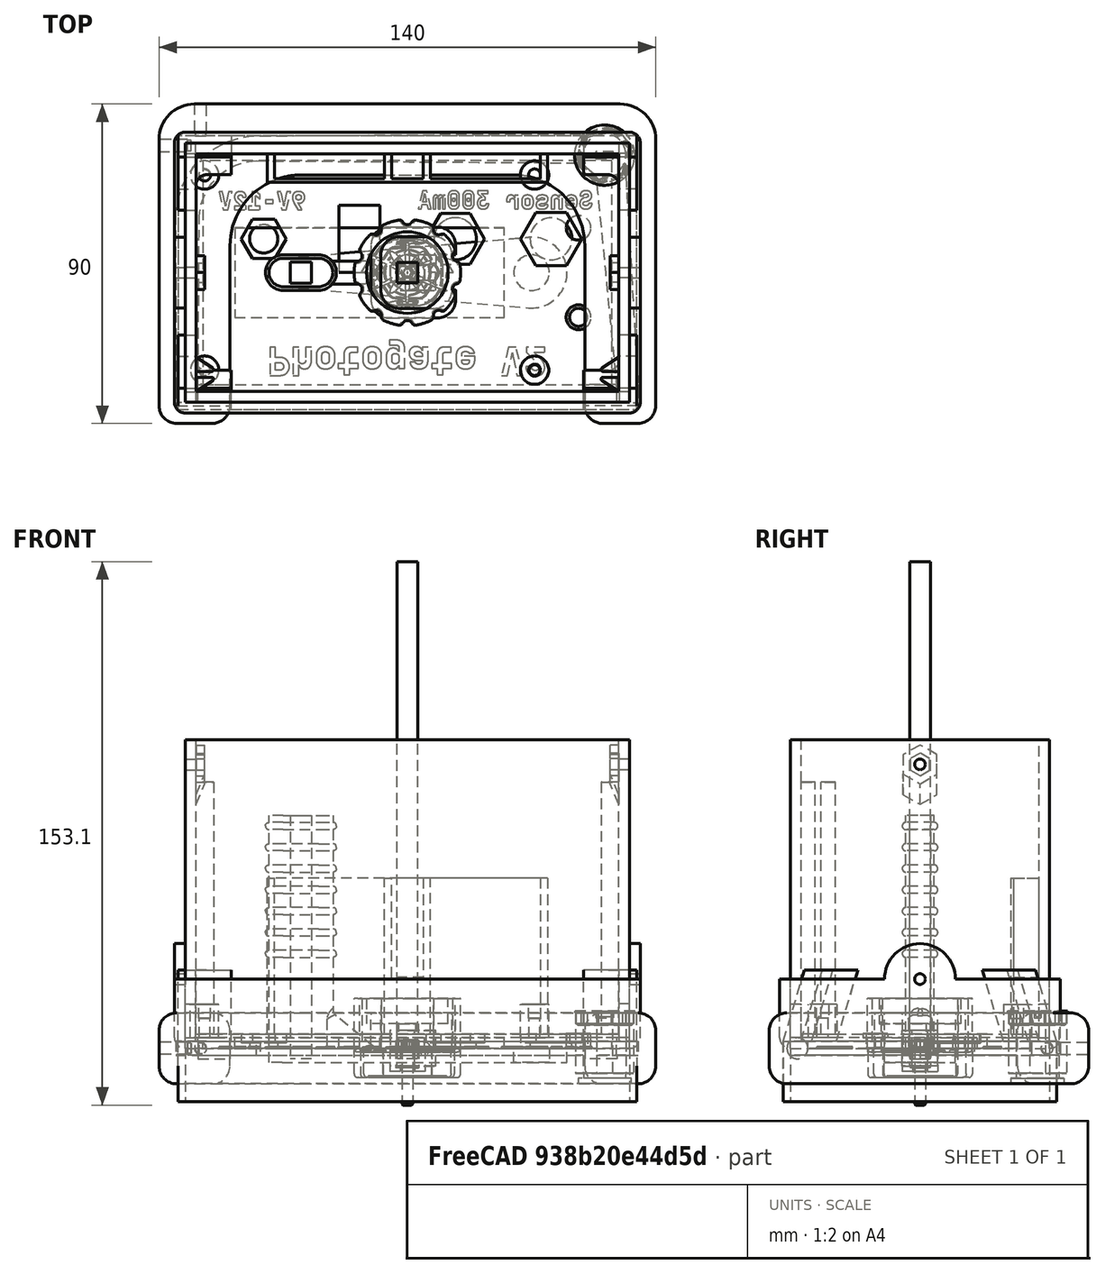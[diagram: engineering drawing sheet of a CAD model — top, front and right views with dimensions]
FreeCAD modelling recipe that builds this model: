
FCSTD DOCUMENT  (FreeCAD 1.1R44795 (Git))
Label: All_Models
License: All rights reserved
LicenseURL: https://en.wikipedia.org/wiki/All_rights_reserved
objects: Sketcher::SketchObject×46, PartDesign::Pad×32, PartDesign::Pocket×28, App::Link×21, App::FeaturePython×21, App::Point×14, PartDesign::Body×12, PartDesign::Mirrored×8, PartDesign::Fillet×7, Part::Part2DObjectPython×4, PartDesign::MultiTransform×3, PartDesign::Chamfer×2, PartDesign::PolarPattern×2, PartDesign::SubtractivePipe×2, PartDesign::SubShapeBinder×2, Assembly::JointGroup×2, Assembly::AssemblyObject×2, Part::FeaturePython×2, App::DocumentObjectGroup×2, PartDesign::LinearPattern×1, +1 more types
note: 354 computed .brp shape members not serialized (recipe doc carries the construction recipe); baked Part::Feature solids carry a one-line shape summary decoded from their .brp

FEATURE [Sketcher::SketchObject] Sketch
  ArcFitTolerance = 1e-06
  AttachmentSupport = -> [XY_Plane]
  ExternalTypes = [0]
  FullyConstrained = true
  MakeInternals = false
  MapMode = 5
  _ExternalGeoVersion = 0
  expr: Constraints[22] = Sketch001.Constraints.display_inner_width - 0.1 mm
  expr: Constraints[23] = Sketch001.Constraints.display_inner_length - 0.1 mm
  sketch-geometry (10):
    g0: LineSegment StartX=-59.6 StartY=-33.5 StartZ=0 EndX=59.6 EndY=-33.5 EndZ=0
    g1: LineSegment StartX=59.6 StartY=-33.5 StartZ=0 EndX=59.6 EndY=33.5 EndZ=0
    g2: LineSegment StartX=59.6 StartY=33.5 StartZ=0 EndX=-59.6 EndY=33.5 EndZ=0
    g3: LineSegment StartX=-59.6 StartY=33.5 StartZ=0 EndX=-59.6 EndY=-33.5 EndZ=0
    g4: GeomPoint [constr] X=0 Y=0 Z=0
    g5: LineSegment StartX=-62.6 StartY=-36.5 StartZ=0 EndX=62.6 EndY=-36.5 EndZ=0
    g6: LineSegment StartX=62.6 StartY=-36.5 StartZ=0 EndX=62.6 EndY=36.5 EndZ=0
    g7: LineSegment StartX=62.6 StartY=36.5 StartZ=0 EndX=-62.6 EndY=36.5 EndZ=0
    g8: LineSegment StartX=-62.6 StartY=36.5 StartZ=0 EndX=-62.6 EndY=-36.5 EndZ=0
    g9: GeomPoint [constr] X=0 Y=0 Z=0
  constraints (24):
    c: Coincident(g0,g1)
    c: Coincident(g1,g2)
    c: Coincident(g2,g3)
    c: Coincident(g3,g0)
    c: Horizontal(g0)
    c: Horizontal(g2)
    c: Vertical(g1)
    c: Vertical(g3)
    c: Symmetric(g2,g0,g4)
    c: Coincident(g4,g-1)
    c: Coincident(g5,g6)
    c: Coincident(g6,g7)
    c: Coincident(g7,g8)
    c: Coincident(g8,g5)
    c: Horizontal(g5)
    c: Horizontal(g7)
    c: Vertical(g6)
    c: Vertical(g8)
    c: Symmetric(g7,g5,g9)
    c: Coincident(g9,g4)
    c: DistanceY(g1,g6) = 3
    c: DistanceX(g1,g6) = 3
    c: DistanceY(g8,g8) = 73
    c: DistanceX(g5,g5) = 125.2
FEATURE [PartDesign::Pad] Pad005
  Direction = (0,0,1)
  Length = 4
  Length2 = 10
  Profile = -> Sketch [Edge6,Edge5,Edge7,Edge8]
  ReferenceAxis = -> Sketch [N_Axis]
  Refine = true
  SideType = 0
  Suppressed = false
  Type = 0
  Type2 = 0
FEATURE [PartDesign::Pad] Pad006
  BaseFeature = -> Pad005
  Direction = (0,0,1)
  Length = 87
  Length2 = 10
  Profile = -> Sketch
  ReferenceAxis = -> Sketch [N_Axis]
  Refine = true
  SideType = 0
  Suppressed = false
  Type = 0
  Type2 = 0
FEATURE [Sketcher::SketchObject] Sketch007
  ArcFitTolerance = 1e-06
  AttachmentSupport = -> [Pad006]
  ExternalGeometry = -> [Pad006]
  ExternalTypes = [0]
  FullyConstrained = true
  MakeInternals = false
  MapMode = 5
  Placement = pos=(-59.6,0,0) rot=(0.57735,0.57735,0.57735;2.0944rad)
  _ExternalGeoVersion = 0
  sketch-geometry (15):
    g0: LineSegment StartX=2.75 StartY=81.5877 StartZ=0 EndX=1.24e-14 EndY=83.1754 EndZ=0
    g1: LineSegment StartX=1.24e-14 StartY=83.1754 StartZ=0 EndX=-2.75 EndY=81.5877 EndZ=0
    g2: LineSegment StartX=-2.75 StartY=81.5877 StartZ=0 EndX=-2.75 EndY=78.4123 EndZ=0
    g3: LineSegment StartX=-2.75 StartY=78.4123 StartZ=0 EndX=-2.895e-13 EndY=76.8246 EndZ=0
    g4: LineSegment StartX=-2.895e-13 StartY=76.8246 StartZ=0 EndX=2.75 EndY=78.4123 EndZ=0
    g5: LineSegment StartX=2.75 StartY=78.4123 StartZ=0 EndX=2.75 EndY=81.5877 EndZ=0
    g6: Circle [constr] CenterX=0 CenterY=80 CenterZ=0 NormalX=0 NormalY=0 NormalZ=1 AngleXU=0 Radius=3.17543
    g7: Circle CenterX=0 CenterY=80 CenterZ=0 NormalX=0 NormalY=0 NormalZ=1 AngleXU=0 Radius=1.5
    g8: LineSegment StartX=4.75 StartY=82.7424 StartZ=0 EndX=-3.91e-14 EndY=85.4848 EndZ=0
    g9: LineSegment StartX=-3.91e-14 StartY=85.4848 StartZ=0 EndX=-4.75 EndY=82.7424 EndZ=0
    g10: LineSegment StartX=-4.75 StartY=82.7424 StartZ=0 EndX=-4.75 EndY=77.2576 EndZ=0
    g11: LineSegment StartX=-4.75 StartY=77.2576 StartZ=0 EndX=3.73e-14 EndY=74.5152 EndZ=0
    g12: LineSegment StartX=3.73e-14 StartY=74.5152 StartZ=0 EndX=4.75 EndY=77.2576 EndZ=0
    g13: LineSegment StartX=4.75 StartY=77.2576 StartZ=0 EndX=4.75 EndY=82.7424 EndZ=0
    g14: Circle [constr] CenterX=0 CenterY=80 CenterZ=0 NormalX=0 NormalY=0 NormalZ=1 AngleXU=0 Radius=5.48483
  constraints (35):
    c: Coincident(g0,g1)
    c: Coincident(g1,g2)
    c: Coincident(g2,g3)
    c: Coincident(g3,g4)
    c: Coincident(g4,g5)
    c: Coincident(g5,g0)
    c: Equal(g0, g1-g5) x5
    c: PointOnObject(g0,g6)
    c: PointOnObject(g1,g6)
    c: PointOnObject(g2,g6)
    c: PointOnObject(g3,g6)
    c: PointOnObject(g4,g6)
    c: PointOnObject(g5,g6)
    c: PointOnObject(g6,g-2)
    c: Coincident(g7,g6)
    c: Diameter(g7) = 3
    c: DistanceX(g1,g0) = 5.5
    c: Horizontal(g0,g1)
    c: DistanceY(g6,g-3) = 7  'gap_box_painel'
    c: Coincident(g8,g9)
    c: Coincident(g9,g10)
    c: Coincident(g10,g11)
    c: Coincident(g11,g12)
    c: Coincident(g12,g13)
    c: Coincident(g13,g8)
    c: Equal(g8, g9-g13) x5
    c: PointOnObject(g8,g14)
    c: PointOnObject(g9,g14)
    c: PointOnObject(g10,g14)
    c: PointOnObject(g11,g14)
    c: PointOnObject(g12,g14)
    c: PointOnObject(g13,g14)
    c: Coincident(g14,g6)
    c: Vertical(g13)
    c: DistanceX(g0,g8) = 2
FEATURE [PartDesign::Pocket] Pocket005
  BaseFeature = -> Pad006
  Direction = (-1,0,0)
  Length = 5
  Length2 = 5
  Profile = -> Sketch007 [Edge7]
  ReferenceAxis = -> Sketch007 [N_Axis]
  Refine = true
  SideType = 0
  Suppressed = false
  Type = 1
  Type2 = 0
FEATURE [PartDesign::Pad] Pad007
  BaseFeature = -> Pocket005
  Direction = (1,0,0)
  Length = 2.5
  Length2 = 10
  Profile = -> Sketch007 [Edge12,Edge5,Edge4,Edge11,Edge10,Edge3,Edge2,Edge1,Edge6,Edge13,Edge8,Edge9]
  ReferenceAxis = -> Sketch007 [N_Axis]
  Refine = true
  SideType = 0
  Suppressed = false
  Type = 0
  Type2 = 0
FEATURE [PartDesign::Chamfer] Chamfer
  Angle = 45
  Base = -> Pad007 [Edge26,Edge31]
  BaseFeature = -> Pad007
  ChamferType = 1
  FlipDirection = false
  Refine = true
  Size = 5
  Size2 = 2.4999
  SupportTransform = false
  Suppressed = false
  UseAllEdges = false
FEATURE [Sketcher::SketchObject] Sketch008
  ArcFitTolerance = 1e-06
  AttachmentSupport = -> [Chamfer]
  ExternalGeometry = -> [Chamfer]
  ExternalTypes = [0]
  FullyConstrained = true
  MakeInternals = false
  MapMode = 5
  Placement = pos=(0,0,4) rot=(0,0,1;0rad)
  _ExternalGeoVersion = 0
  sketch-geometry (10):
    g0: LineSegment StartX=-59.6 StartY=-33.5 StartZ=0 EndX=-59.6 EndY=-29.5 EndZ=0
    g1: LineSegment StartX=-59.6 StartY=-29.5 StartZ=0 EndX=-55.1 EndY=-29.5 EndZ=0
    g2: LineSegment StartX=-54.8288 StartY=-30.4201 StartZ=0 EndX=-59.6 EndY=-33.5 EndZ=0
    g3: ArcOfCircle CenterX=-55.1 CenterY=-30 CenterZ=0 NormalX=0 NormalY=0 NormalZ=1 AngleXU=0 Radius=0.5 StartAngle=5.28561 EndAngle=7.85398
    g4: GeomPoint [constr] X=-53.4035 Y=-29.5 Z=0
    g5: GeomPoint X=-54.6 Y=-30 Z=0
    g6: LineSegment StartX=-59.6 StartY=-23.85 StartZ=0 EndX=-59.6 EndY=-27.85 EndZ=0
    g7: LineSegment StartX=-59.6 StartY=-27.85 StartZ=0 EndX=-55.1 EndY=-27.85 EndZ=0
    g8: LineSegment StartX=-54.8288 StartY=-26.9299 StartZ=0 EndX=-59.6 EndY=-23.85 EndZ=0
    g9: ArcOfCircle CenterX=-55.1 CenterY=-27.35 CenterZ=0 NormalX=0 NormalY=0 NormalZ=1 AngleXU=0 Radius=0.5 StartAngle=4.71239 EndAngle=7.28076
  constraints (25):
    c: Vertical(g0)
    c: Coincident(g0,g1)
    c: Horizontal(g1)
    c: DistanceY(g0,g0) = 4
    c: PointOnObject(g4,g1)
    c: PointOnObject(g4,g2)
    c: Tangent(g1,g3) = 1.5708
    c: Tangent(g2,g3) = 1.5708
    c: Radius(g3) = 0.5
    c: PointOnObject(g5,g3)
    c: DistanceX(g0,g5) = 5
    c: Horizontal(g3,g5)
    c: Vertical(g6)
    c: Coincident(g6,g7)
    c: Coincident(g8,g6)
    c: Horizontal(g7)
    c: Tangent(g7,g9) = -1.5708
    c: Tangent(g8,g9) = -1.5708
    c: Radius(g9) = 0.5
    c: Vertical(g6,g0)
    c: Vertical(g7,g1)
    c: Equal(g0,g6)
    c: DistanceY(g1,g7) = 1.65
    c: Coincident(g2,g0)
    c: Coincident(g0,g-4)
FEATURE [PartDesign::Pad] Pad008
  BaseFeature = -> Chamfer
  Direction = (0,0,1)
  Length = 10
  Length2 = 10
  Offset = 12
  Profile = -> Sketch008
  ReferenceAxis = -> Sketch008 [N_Axis]
  Refine = true
  SideType = 0
  Suppressed = false
  Type = 3
  Type2 = 0
  UpToFace = -> Chamfer [Face11]
  expr: Offset = Sketch007.Constraints.gap_box_painel + 5 mm
FEATURE [PartDesign::Mirrored] Mirrored004
  BaseFeature = -> Pad008
  MirrorPlane = -> YZ_Plane
  Originals = -> [Chamfer,Pad007,Pad008,Pocket005]
  Refine = true
  Suppressed = false
  TransformMode = 0
FEATURE [Sketcher::SketchObject] Sketch009
  ArcFitTolerance = 1e-06
  AttachmentSupport = -> [XY_Plane]
  ExternalTypes = [0]
  FullyConstrained = true
  MakeInternals = false
  MapMode = 5
  _ExternalGeoVersion = 0
  sketch-geometry (11):
    g0: Circle CenterX=40.5 CenterY=9.5 CenterZ=0 NormalX=0 NormalY=0 NormalZ=1 AngleXU=0 Radius=5.9
    g1: Circle CenterX=-40.5 CenterY=9.5 CenterZ=0 NormalX=0 NormalY=0 NormalZ=1 AngleXU=0 Radius=4
    g2: LineSegment StartX=-19.25 StartY=19 StartZ=0 EndX=-19.25 EndY=0 EndZ=0
    g3: LineSegment StartX=-19.25 StartY=0 StartZ=0 EndX=-7.75 EndY=0 EndZ=0
    g4: LineSegment StartX=-7.75 StartY=0 StartZ=0 EndX=-7.75 EndY=19 EndZ=0
    g5: LineSegment StartX=-7.75 StartY=19 StartZ=0 EndX=-19.25 EndY=19 EndZ=0
    g6: GeomPoint [constr] X=-13.5 Y=9.5 Z=0
    g7: Circle CenterX=13.5 CenterY=9.5 CenterZ=0 NormalX=0 NormalY=0 NormalZ=1 AngleXU=0 Radius=5.95
    g8: LineSegment [constr] StartX=-40.5 StartY=9.5 StartZ=0 EndX=-13.5 EndY=9.5 EndZ=0
    g9: LineSegment [constr] StartX=-13.5 StartY=9.5 StartZ=0 EndX=13.5 EndY=9.5 EndZ=0
    g10: LineSegment [constr] StartX=13.5 StartY=9.5 StartZ=0 EndX=40.5 EndY=9.5 EndZ=0
  constraints (27):
    c: Diameter(g0) = 11.8
    c: Diameter(g1) = 8
    c: Coincident(g2,g3)
    c: Coincident(g3,g4)
    c: Coincident(g4,g5)
    c: Coincident(g5,g2)
    c: Vertical(g2)
    c: Vertical(g4)
    c: Horizontal(g3)
    c: Horizontal(g5)
    c: Symmetric(g4,g2,g6)
    c: Diameter(g7) = 11.9
    c: DistanceY(g4,g4) = 19
    c: Distance(g5,g5) = 11.5
    c: Coincident(g8,g1)
    c: Horizontal(g8)
    c: Coincident(g9,g8)
    c: Coincident(g9,g7)
    c: Coincident(g10,g7)
    c: Horizontal(g10)
    c: Coincident(g10,g0)
    c: Coincident(g8,g6)
    c: Equal(g8,g9)
    c: Equal(g9,g10)
    c: Horizontal(g-1,g3)
    c: DistanceX(g8,g8) = 27
    c: Symmetric(g6,g7,g-2)
FEATURE [PartDesign::Pocket] Pocket006
  BaseFeature = -> Mirrored004
  Direction = (0,0,-1)
  Length = 5
  Length2 = 5
  Profile = -> Sketch009
  ReferenceAxis = -> Sketch009 [N_Axis]
  Refine = true
  Reversed = true
  SideType = 0
  Suppressed = false
  Type = 2
  Type2 = 0
FEATURE [Part::Part2DObjectPython] ShapeString  # Draft 2D object (typed FeaturePython)
  FontFile = <userpath>/Documents/FreeCAD/Fonts/JetBrainsMonoNerdFont-ExtraBold.ttf
  Fuse = false
  Justification = 7
  JustificationReference = 0
  KeepLeftMargin = false
  MakeFace = true
  ObliqueAngle = 0
  Placement = pos=(-41.02,17.76,1e-15) rot=(0,-1,0;3.14159rad)
  ScaleToSize = true
  Size = 5
  String = 9V-12V
  Tracking = 0
FEATURE [Part::Part2DObjectPython] ShapeString001  # Draft 2D object (typed FeaturePython)
  FontFile = <userpath>/Documents/FreeCAD/Fonts/JetBrainsMonoNerdFont-Bold.ttf
  Fuse = false
  Justification = 7
  JustificationReference = 0
  KeepLeftMargin = false
  MakeFace = true
  ObliqueAngle = 0
  Placement = pos=(13,18,1.3e-15) rot=(0,-1,0;3.14159rad)
  ScaleToSize = true
  Size = 5
  String = 300mA
  Tracking = 0
FEATURE [Part::Part2DObjectPython] ShapeString002  # Draft 2D object (typed FeaturePython)
  FontFile = <userpath>/Documents/FreeCAD/Fonts/JetBrainsMonoNerdFont-ExtraBold.ttf
  Fuse = false
  Justification = 7
  JustificationReference = 0
  KeepLeftMargin = false
  MakeFace = true
  ObliqueAngle = 0
  Placement = pos=(40,18,-4.9e-15) rot=(0,-1,0;3.14159rad)
  ScaleToSize = true
  Size = 5
  String = Sensor
  Tracking = 0
FEATURE [PartDesign::Pocket] Pocket007
  BaseFeature = -> Pocket006
  Direction = (1e-16,0,1)
  Length = 0.4
  Length2 = 5
  Profile = -> ShapeString002
  ReferenceAxis = -> ShapeString002 [N_Axis]
  Refine = true
  SideType = 0
  Suppressed = false
  Type = 0
  Type2 = 0
FEATURE [PartDesign::Pocket] Pocket008
  BaseFeature = -> Pocket007
  Direction = (1e-16,0,1)
  Length = 0.4
  Length2 = 5
  Profile = -> ShapeString001
  ReferenceAxis = -> ShapeString001 [N_Axis]
  Refine = true
  SideType = 0
  Suppressed = false
  Type = 0
  Type2 = 0
FEATURE [PartDesign::Pocket] Pocket009
  BaseFeature = -> Pocket008
  Direction = (1e-16,0,1)
  Length = 0.4
  Length2 = 5
  Profile = -> ShapeString
  ReferenceAxis = -> ShapeString [N_Axis]
  Refine = true
  SideType = 0
  Suppressed = false
  Type = 0
  Type2 = 0
FEATURE [Sketcher::SketchObject] Sketch010
  ArcFitTolerance = 1e-06
  AttachmentSupport = -> [XY_Plane002]
  ExternalTypes = [0]
  FullyConstrained = true
  MakeInternals = false
  MapMode = 5
  _ExternalGeoVersion = 0
  sketch-geometry (9):
    g0: ArcOfCircle CenterX=-35 CenterY=0 CenterZ=0 NormalX=0 NormalY=0 NormalZ=1 AngleXU=0 Radius=4 StartAngle=1.65662 EndAngle=4.62657
    g1: ArcOfCircle CenterX=35 CenterY=0 CenterZ=0 NormalX=0 NormalY=0 NormalZ=1 AngleXU=0 Radius=10 StartAngle=4.62657 EndAngle=7.9398
    g2: LineSegment StartX=-35.3429 StartY=3.98528 StartZ=0 EndX=34.1429 EndY=9.9632 EndZ=0
    g3: LineSegment StartX=-35.3429 StartY=-3.98528 StartZ=0 EndX=34.1429 EndY=-9.9632 EndZ=0
    g4: ArcOfCircle CenterX=-35 CenterY=0 CenterZ=0 NormalX=0 NormalY=0 NormalZ=1 AngleXU=0 Radius=4 StartAngle=1.5708 EndAngle=4.71239
    g5: ArcOfCircle CenterX=-25 CenterY=-1e-16 CenterZ=0 NormalX=0 NormalY=0 NormalZ=1 AngleXU=0 Radius=4 StartAngle=4.71239 EndAngle=7.85398
    g6: LineSegment StartX=-35 StartY=4 StartZ=0 EndX=-25 EndY=4 EndZ=0
    g7: LineSegment StartX=-35 StartY=-4 StartZ=0 EndX=-25 EndY=-4 EndZ=0
    g8: Circle CenterX=35 CenterY=0 CenterZ=0 NormalX=0 NormalY=0 NormalZ=1 AngleXU=0 Radius=5
  constraints (20):
    c: Tangent(g0,g2) = 1.5708
    c: Tangent(g0,g3) = -1.5708
    c: Tangent(g1,g2) = 1.5708
    c: Tangent(g1,g3) = -1.5708
    c: Symmetric(g0,g1,g-1)
    c: DistanceX(g0,g1) = 70
    c: PointOnObject(g0,g-1)
    c: Radius(g0) = 4
    c: Radius(g1) = 10
    c: Tangent(g4,g6) = 1.5708
    c: Tangent(g4,g7) = -1.5708
    c: Tangent(g5,g6) = 1.5708
    c: Tangent(g5,g7) = -1.5708
    c: Equal(g4,g5)
    c: Horizontal(g7)
    c: Coincident(g4,g0)
    c: Tangent(g4,g0)
    c: DistanceX(g0,g5) = 10
    c: Diameter(g8) = 10
    c: Coincident(g8,g1)
FEATURE [PartDesign::Pad] Pad009
  Direction = (0,0,1)
  Length = 4
  Length2 = 10
  Profile = -> Sketch010 [Edge1,Edge2,Edge4,Edge9,Edge3]
  ReferenceAxis = -> Sketch010 [N_Axis]
  Refine = true
  Reversed = true
  SideType = 0
  Suppressed = false
  Type = 0
  Type2 = 0
FEATURE [PartDesign::Pad] Pad010
  BaseFeature = -> Pad009
  Direction = (0,0,1)
  Length = 65.65
  Length2 = 10
  Profile = -> Sketch010 [Edge7,Edge6,Vertex6,Edge5,Edge8]
  ReferenceAxis = -> Sketch010 [N_Axis]
  Refine = true
  SideType = 0
  Suppressed = false
  Type = 0
  Type2 = 0
  expr: Length = Sketch001.Constraints.display_inner_length / 2 + 3 mm
FEATURE [Sketcher::SketchObject] Sketch011
  ArcFitTolerance = 1e-06
  AttachmentOffset = pos=(0,0,-2) rot=(0,0,1;0rad)
  AttachmentSupport = -> [Pad010]
  ExternalTypes = [0]
  FullyConstrained = true
  MakeInternals = false
  MapMode = 5
  Placement = pos=(0,0,63.65) rot=(0,0,1;0rad)
  _ExternalGeoVersion = 0
  sketch-geometry (4):
    g0: ArcOfCircle CenterX=-35 CenterY=0 CenterZ=0 NormalX=0 NormalY=0 NormalZ=1 AngleXU=0 Radius=5 StartAngle=1.5708 EndAngle=4.71239
    g1: ArcOfCircle CenterX=-25 CenterY=-1e-16 CenterZ=0 NormalX=0 NormalY=0 NormalZ=1 AngleXU=0 Radius=5 StartAngle=4.71239 EndAngle=7.85398
    g2: LineSegment StartX=-35 StartY=5 StartZ=0 EndX=-25 EndY=5 EndZ=0
    g3: LineSegment StartX=-35 StartY=-5 StartZ=0 EndX=-25 EndY=-5 EndZ=0
  constraints (8):
    c: Tangent(g0,g2) = 1.5708
    c: Tangent(g0,g3) = -1.5708
    c: Tangent(g1,g2) = 1.5708
    c: Tangent(g1,g3) = -1.5708
    c: Equal(g0,g1)
    c: Radius(g1) = 5
    c: Coincident(g1,g-3)
    c: Coincident(g0,g-4)
FEATURE [PartDesign::Pad] Pad011
  BaseFeature = -> Pad010
  Direction = (0,0,1)
  Length = 2
  Length2 = 10
  Profile = -> Sketch011
  ReferenceAxis = -> Sketch011 [N_Axis]
  Refine = true
  Reversed = true
  SideType = 0
  Suppressed = false
  Type = 0
  Type2 = 0
FEATURE [PartDesign::Fillet] Fillet001
  Base = -> Pad011 [Face14]
  BaseFeature = -> Pad011
  Radius = 0.99
  Refine = true
  SupportTransform = false
  Suppressed = false
  UseAllEdges = false
FEATURE [PartDesign::LinearPattern] LinearPattern
  BaseFeature = -> Fillet001
  Direction = -> Z_Axis002
  Length = 36
  Length2 = 100
  Mode = 1
  Mode2 = 0
  Occurrences = 7
  Occurrences2 = 1
  Offset = 6
  Offset2 = 10
  Originals = -> [Pad011,Fillet001]
  Refine = true
  Reversed = true
  Reversed2 = false
  SpacingPattern = [0]
  SpacingPattern2 = [0]
  Spacings = [-1,-1,-1,-1,-1,-1]
  Suppressed = false
  TransformMode = 0
FEATURE [Sketcher::SketchObject] Sketch012
  ArcFitTolerance = 1e-06
  AttachmentSupport = -> [XY_Plane003]
  ExternalTypes = [0]
  FullyConstrained = true
  MakeInternals = false
  MapMode = 5
  _ExternalGeoVersion = 0
  sketch-geometry (1):
    g0: Circle CenterX=0 CenterY=0 CenterZ=0 NormalX=0 NormalY=0 NormalZ=1 AngleXU=0 Radius=15
  constraints (2):
    c: Diameter(g0) = 30
    c: Coincident(g0,g-1)
FEATURE [PartDesign::Pad] Pad012
  Direction = (0,0,1)
  Length = 8.2
  Length2 = 10
  Profile = -> Sketch012
  ReferenceAxis = -> Sketch012 [N_Axis]
  Refine = true
  Reversed = true
  SideType = 0
  Suppressed = false
  Type = 0
  Type2 = 0
FEATURE [Sketcher::SketchObject] Sketch013
  ArcFitTolerance = 1e-06
  AttachmentSupport = -> [XY_Plane003]
  ExternalGeometry = -> [Pad012]
  ExternalTypes = [0]
  FullyConstrained = true
  MakeInternals = false
  MapMode = 5
  _ExternalGeoVersion = 0
  sketch-geometry (4):
    g0: LineSegment [constr] StartX=0 StartY=0 StartZ=0 EndX=-1.95789 EndY=14.8717 EndZ=0
    g1: LineSegment [constr] StartX=0 StartY=0 StartZ=0 EndX=1.95789 EndY=14.8717 EndZ=0
    g2: ArcOfCircle CenterX=0 CenterY=0 CenterZ=0 NormalX=0 NormalY=0 NormalZ=1 AngleXU=0 Radius=15 StartAngle=1.4399 EndAngle=1.7017
    g3: ArcOfCircle CenterX=-4.3e-15 CenterY=15 CenterZ=0 NormalX=0 NormalY=0 NormalZ=1 AngleXU=0 Radius=1.96209 StartAngle=3.20704 EndAngle=6.21774
  constraints (12):
    c: PointOnObject(g0,g-3)
    c: PointOnObject(g1,g-3)
    c: Horizontal(g1,g0)
    c: Coincident(g1,g-1)
    c: Coincident(g0,g1)
    c: PointOnObject(g3,g2)
    c: Coincident(g3,g2)
    c: Coincident(g3,g2)
    c: Coincident(g2,g0)
    c: Horizontal(g0,g2)
    c: Coincident(g2,g0)
    c: Angle(g1,g0) = 0.261799
FEATURE [PartDesign::Pocket] Pocket011
  BaseFeature = -> Pad012
  Direction = (0,0,-1)
  Length = 5
  Length2 = 5
  Profile = -> Sketch013
  ReferenceAxis = -> Sketch013 [N_Axis]
  Refine = true
  SideType = 0
  Suppressed = false
  Type = 1
  Type2 = 0
FEATURE [PartDesign::PolarPattern] PolarPattern
  Angle = 360
  Axis = -> Sketch013 [N_Axis]
  BaseFeature = -> Pocket011
  Mode = 0
  Occurrences = 10
  Offset = 120
  Originals = -> [Pocket011]
  Refine = true
  SpacingPattern = [0]
  Spacings = [-1,-1,-1,-1,-1,-1,-1,-1,-1]
  Suppressed = false
  TransformMode = 0
FEATURE [Sketcher::SketchObject] Sketch016
  ArcFitTolerance = 1e-06
  AttachmentSupport = -> [XY_Plane005]
  ExternalTypes = [0]
  FullyConstrained = true
  MakeInternals = false
  MapMode = 5
  _ExternalGeoVersion = 0
  sketch-geometry (22):
    g0: LineSegment StartX=-70 StartY=-37.5 StartZ=0 EndX=-70 EndY=37.5 EndZ=0
    g1: LineSegment StartX=-60 StartY=47.5 StartZ=0 EndX=60 EndY=47.5 EndZ=0
    g2: LineSegment StartX=70 StartY=37.5 StartZ=0 EndX=70 EndY=-37.5 EndZ=0
    g3: LineSegment StartX=65 StartY=-42.5 StartZ=0 EndX=55 EndY=-42.5 EndZ=0
    g4: LineSegment StartX=50 StartY=-37.5 StartZ=0 EndX=50 EndY=7.5 EndZ=0
    g5: LineSegment StartX=30 StartY=27.5 StartZ=0 EndX=-30 EndY=27.5 EndZ=0
    g6: LineSegment StartX=-50 StartY=7.5 StartZ=0 EndX=-50 EndY=-37.5 EndZ=0
    g7: LineSegment StartX=-55 StartY=-42.5 StartZ=0 EndX=-65 EndY=-42.5 EndZ=0
    g8: ArcOfCircle CenterX=-65 CenterY=-37.5 CenterZ=0 NormalX=0 NormalY=0 NormalZ=1 AngleXU=0 Radius=5 StartAngle=3.14159 EndAngle=4.71239
    g9: ArcOfCircle CenterX=-55 CenterY=-37.5 CenterZ=0 NormalX=0 NormalY=0 NormalZ=1 AngleXU=0 Radius=5 StartAngle=4.71239 EndAngle=6.28319
    g10: ArcOfCircle CenterX=-30 CenterY=7.5 CenterZ=0 NormalX=0 NormalY=0 NormalZ=1 AngleXU=0 Radius=20 StartAngle=1.5708 EndAngle=3.14159
    g11: ArcOfCircle CenterX=30 CenterY=7.5 CenterZ=0 NormalX=0 NormalY=0 NormalZ=1 AngleXU=0 Radius=20 StartAngle=0 EndAngle=1.5708
    g12: ArcOfCircle CenterX=60 CenterY=37.5 CenterZ=0 NormalX=0 NormalY=0 NormalZ=1 AngleXU=0 Radius=10 StartAngle=0 EndAngle=1.5708
    g13: ArcOfCircle CenterX=65 CenterY=-37.5 CenterZ=0 NormalX=0 NormalY=0 NormalZ=1 AngleXU=0 Radius=5 StartAngle=4.71239 EndAngle=6.28319
    g14: ArcOfCircle CenterX=55 CenterY=-37.5 CenterZ=0 NormalX=0 NormalY=0 NormalZ=1 AngleXU=0 Radius=5 StartAngle=3.14159 EndAngle=4.71239
    g15: ArcOfCircle CenterX=-60 CenterY=37.5 CenterZ=0 NormalX=0 NormalY=0 NormalZ=1 AngleXU=0 Radius=10 StartAngle=1.5708 EndAngle=3.14159
    g16: LineSegment [constr] StartX=-30 StartY=27.5 StartZ=0 EndX=-30 EndY=47.5 EndZ=0
    g17: LineSegment [constr] StartX=-50 StartY=7.5 StartZ=0 EndX=-70 EndY=7.5 EndZ=0
    g18: Circle CenterX=55.6066 CenterY=33.1066 CenterZ=0 NormalX=0 NormalY=0 NormalZ=1 AngleXU=0 Radius=6
    g19: GeomPoint X=44.1421 Y=21.6421 Z=0
    g20: GeomPoint X=67.0711 Y=44.5711 Z=0
    g21: LineSegment [constr] StartX=44.1421 StartY=21.6421 StartZ=0 EndX=67.0711 EndY=44.5711 EndZ=0
  constraints (51):
    c: Vertical(g0)
    c: Horizontal(g1)
    c: Horizontal(g3)
    c: Vertical(g4)
    c: Horizontal(g5)
    c: Vertical(g6)
    c: Horizontal(g7)
    c: Tangent(g7,g8) = 1.5708
    c: Tangent(g0,g8) = 1.5708
    c: Tangent(g6,g9) = 1.5708
    c: Tangent(g7,g9) = 1.5708
    c: Tangent(g5,g10) = -1.5708
    c: Tangent(g6,g10) = -1.5708
    c: Tangent(g4,g11) = -1.5708
    c: Tangent(g5,g11) = -1.5708
    c: Tangent(g2,g12) = 1.5708
    c: Tangent(g1,g12) = 1.5708
    c: Tangent(g3,g13) = 1.5708
    c: Tangent(g2,g13) = 1.5708
    c: Tangent(g3,g14) = 1.5708
    c: Tangent(g4,g14) = 1.5708
    c: Tangent(g0,g15) = 1.5708
    c: Tangent(g1,g15) = 1.5708
    c: Radius(g15) = 10
    c: Radius(g10) = 20
    c: Radius(g8) = 5
    c: Equal(g15,g12)
    c: Symmetric(g6,g4,g-2)
    c: Coincident(g16,g5)
    c: PointOnObject(g16,g1)
    c: Coincident(g17,g6)
    c: PointOnObject(g17,g0)
    c: Horizontal(g17)
    c: Vertical(g16)
    c: Equal(g17,g16)
    c: DistanceY(g16,g16) = 20
    c: Symmetric(g0,g2,g-2)
    c: Equal(g8,g9)
    c: DistanceX(g6,g4) = 100
    c: DistanceY(g7,g5) = 70
    c: Symmetric(g2,g2,g-1)
    c: Equal(g14,g9)
    c: Equal(g13,g14)
    c: Diameter(g18) = 12
    c: PointOnObject(g19,g11)
    c: PointOnObject(g20,g12)
    c: Symmetric(g19,g20,g18)
    c: Coincident(g21,g19)
    c: Coincident(g21,g20)
    c: Perpendicular(g11,g21)
    c: Perpendicular(g12,g21)
FEATURE [PartDesign::Pad] Pad014
  Direction = (0,0,1)
  Length = 20
  Length2 = 10
  Profile = -> Sketch016
  ReferenceAxis = -> Sketch016 [N_Axis]
  Refine = true
  SideType = 2
  Suppressed = false
  Type = 0
  Type2 = 0
FEATURE [Sketcher::SketchObject] Sketch017
  ArcFitTolerance = 1e-06
  AttachmentSupport = -> [Pad014]
  ExternalGeometry = -> [Pad014]
  ExternalTypes = [0]
  FullyConstrained = true
  MakeInternals = false
  MapMode = 5
  Placement = pos=(-50,0,0) rot=(0.57735,0.57735,0.57735;2.0944rad)
  _ExternalGeoVersion = 0
  sketch-geometry (5):
    g0: Circle CenterX=-34.55 CenterY=0 CenterZ=0 NormalX=0 NormalY=0 NormalZ=1 AngleXU=0 Radius=2.95
    g1: ArcOfCircle CenterX=-34.55 CenterY=0 CenterZ=0 NormalX=0 NormalY=0 NormalZ=1 AngleXU=0 Radius=2.95 StartAngle=5.53819 EndAngle=7.02818
    g2: ArcOfCircle CenterX=-34.55 CenterY=0 CenterZ=0 NormalX=0 NormalY=0 NormalZ=1 AngleXU=0 Radius=2.95 StartAngle=2.3966 EndAngle=3.88658
    g3: LineSegment StartX=-32.3815 StartY=2 StartZ=0 EndX=-36.7185 EndY=2 EndZ=0
    g4: LineSegment StartX=-36.7185 StartY=-2 StartZ=0 EndX=-32.3815 EndY=-2 EndZ=0
  constraints (15):
    c: PointOnObject(g0,g-1)
    c: Tangent(g0,g-3)
    c: Diameter(g0) = 5.9  'led_diammeter'
    c: Coincident(g1,g0)
    c: PointOnObject(g1,g0)
    c: Coincident(g2,g0)
    c: PointOnObject(g2,g0)
    c: Coincident(g3,g2)
    c: Coincident(g4,g2)
    c: Coincident(g4,g1)
    c: Equal(g3,g4)
    c: Distance(g4,g3) = 4
    c: Coincident(g1,g3)
    c: Parallel(g4,g3)
    c: Horizontal(g4)
FEATURE [PartDesign::Pocket] Pocket015
  BaseFeature = -> Pad014
  Direction = (-1,0,0)
  Length = 5
  Length2 = 5
  Offset = -5
  Profile = -> Sketch017 [Edge2,Edge4,Edge3,Edge5]
  ReferenceAxis = -> Sketch017 [N_Axis]
  Refine = true
  SideType = 0
  Suppressed = false
  Type = 2
  Type2 = 0
FEATURE [PartDesign::Pocket] Pocket016
  BaseFeature = -> Pocket015
  Direction = (-1,0,0)
  Length = 9
  Length2 = 5
  Profile = -> Sketch017 [Edge1]
  ReferenceAxis = -> Sketch017 [N_Axis]
  Refine = true
  SideType = 0
  Suppressed = false
  Type = 0
  Type2 = 0
FEATURE [PartDesign::Mirrored] Mirrored006
  BaseFeature = -> Pocket016
  MirrorPlane = -> YZ_Plane005
  Originals = -> [Pocket016,Pocket015]
  Refine = true
  Suppressed = false
  TransformMode = 0
FEATURE [Sketcher::SketchObject] Sketch019
  ArcFitTolerance = 1e-06
  AttachmentSupport = -> [Mirrored006]
  ExternalGeometry = -> [Mirrored006]
  ExternalTypes = [0]
  FullyConstrained = true
  MakeInternals = false
  MapMode = 5
  Placement = pos=(0,0,10) rot=(0,0,1;0rad)
  _ExternalGeoVersion = 0
  sketch-geometry (8):
    g0: LineSegment StartX=63.817 StartY=35.3066 StartZ=0 EndX=57.8066 EndY=41.317 EndZ=0
    g1: LineSegment StartX=57.8066 StartY=41.317 StartZ=0 EndX=49.5962 EndY=39.117 EndZ=0
    g2: LineSegment StartX=49.5962 StartY=39.117 StartZ=0 EndX=47.3962 EndY=30.9066 EndZ=0
    g3: LineSegment StartX=47.3962 StartY=30.9066 StartZ=0 EndX=53.4066 EndY=24.8962 EndZ=0
    g4: LineSegment StartX=53.4066 StartY=24.8962 StartZ=0 EndX=61.617 EndY=27.0962 EndZ=0
    g5: LineSegment StartX=61.617 StartY=27.0962 StartZ=0 EndX=63.817 EndY=35.3066 EndZ=0
    g6: Circle [constr] CenterX=55.6066 CenterY=33.1066 CenterZ=0 NormalX=0 NormalY=0 NormalZ=1 AngleXU=0 Radius=8.5
    g7: LineSegment [constr] StartX=44.1421 StartY=21.6421 StartZ=0 EndX=67.0711 EndY=44.5711 EndZ=0
  constraints (20):
    c: Coincident(g0,g1)
    c: Coincident(g1,g2)
    c: Coincident(g2,g3)
    c: Coincident(g3,g4)
    c: Coincident(g4,g5)
    c: Coincident(g5,g0)
    c: Equal(g0, g1-g5) x5
    c: PointOnObject(g0,g6)
    c: PointOnObject(g1,g6)
    c: PointOnObject(g2,g6)
    c: PointOnObject(g3,g6)
    c: PointOnObject(g4,g6)
    c: PointOnObject(g5,g6)
    c: Coincident(g6,g-3)
    c: PointOnObject(g7,g-4)
    c: PointOnObject(g7,g-5)
    c: PointOnObject(g6,g7)
    c: Perpendicular(g-4,g7)
    c: Perpendicular(g3,g7)
    c: Diameter(g6) = 17
FEATURE [PartDesign::Pocket] Pocket017
  BaseFeature = -> Mirrored006
  Direction = (0,0,-1)
  Length = 17
  Length2 = 5
  Offset = 3
  Profile = -> Sketch019
  ReferenceAxis = -> Sketch019 [N_Axis]
  Refine = true
  SideType = 0
  Suppressed = false
  Type = 0
  Type2 = 0
FEATURE [Sketcher::SketchObject] Sketch020
  ArcFitTolerance = 1e-06
  AttachmentSupport = -> [Pocket017]
  ExternalGeometry = -> [Pocket017]
  ExternalTypes = [0]
  FullyConstrained = true
  MakeInternals = false
  MapMode = 5
  Placement = pos=(0,0,-10) rot=(1,0,0;3.14159rad)
  _ExternalGeoVersion = 0
  sketch-geometry (1):
    g0: Circle CenterX=55.6066 CenterY=-33.1066 CenterZ=0 NormalX=0 NormalY=0 NormalZ=1 AngleXU=0 Radius=7.5
  constraints (2):
    c: Diameter(g0) = 15
    c: Coincident(g0,g-3)
FEATURE [PartDesign::Pocket] Pocket018
  BaseFeature = -> Pocket017
  Direction = (0,0,1)
  Length = 1.55
  Length2 = 5
  Profile = -> Sketch020
  ReferenceAxis = -> Sketch020 [N_Axis]
  Refine = true
  SideType = 0
  Suppressed = false
  Type = 0
  Type2 = 0
FEATURE [Sketcher::SketchObject] Sketch029
  ArcFitTolerance = 1e-06
  AttachmentSupport = -> [XY_Plane006]
  ExternalTypes = [0]
  FullyConstrained = true
  MakeInternals = false
  MapMode = 5
  _ExternalGeoVersion = 0
  expr: Constraints[22] = Sketch001.Constraints.display_inner_length
  expr: Constraints[23] = Sketch001.Constraints.display_inner_width
  sketch-geometry (10):
    g0: LineSegment StartX=-62.65 StartY=-36.55 StartZ=0 EndX=62.65 EndY=-36.55 EndZ=0
    g1: LineSegment StartX=62.65 StartY=-36.55 StartZ=0 EndX=62.65 EndY=36.55 EndZ=0
    g2: LineSegment StartX=62.65 StartY=36.55 StartZ=0 EndX=-62.65 EndY=36.55 EndZ=0
    g3: LineSegment StartX=-62.65 StartY=36.55 StartZ=0 EndX=-62.65 EndY=-36.55 EndZ=0
    g4: GeomPoint [constr] X=0 Y=0 Z=0
    g5: LineSegment StartX=-64.65 StartY=-38.55 StartZ=0 EndX=64.65 EndY=-38.55 EndZ=0
    g6: LineSegment StartX=64.65 StartY=-38.55 StartZ=0 EndX=64.65 EndY=38.55 EndZ=0
    g7: LineSegment StartX=64.65 StartY=38.55 StartZ=0 EndX=-64.65 EndY=38.55 EndZ=0
    g8: LineSegment StartX=-64.65 StartY=38.55 StartZ=0 EndX=-64.65 EndY=-38.55 EndZ=0
    g9: GeomPoint [constr] X=0 Y=0 Z=0
  constraints (24):
    c: Coincident(g0,g1)
    c: Coincident(g1,g2)
    c: Coincident(g2,g3)
    c: Coincident(g3,g0)
    c: Horizontal(g0)
    c: Horizontal(g2)
    c: Vertical(g1)
    c: Vertical(g3)
    c: Symmetric(g2,g0,g4)
    c: Coincident(g4,g-1)
    c: Coincident(g5,g6)
    c: Coincident(g6,g7)
    c: Coincident(g7,g8)
    c: Coincident(g8,g5)
    c: Horizontal(g5)
    c: Horizontal(g7)
    c: Vertical(g6)
    c: Vertical(g8)
    c: Symmetric(g7,g5,g9)
    c: Coincident(g9,g4)
    c: DistanceY(g1,g6) = 2
    c: DistanceX(g1,g6) = 2
    c: DistanceX(g0,g0) = 125.3
    c: DistanceY(g1,g1) = 73.1
FEATURE [PartDesign::Pad] Pad015
  Direction = (0,0,1)
  Length = 15
  Length2 = 10
  Profile = -> Sketch029
  ReferenceAxis = -> Sketch029 [N_Axis]
  Refine = true
  Reversed = true
  SideType = 0
  Suppressed = false
  Type = 0
  Type2 = 0
FEATURE [Sketcher::SketchObject] Sketch030
  ArcFitTolerance = 1e-06
  AttachmentSupport = -> [XY_Plane006]
  ExternalGeometry = -> [Pad015]
  ExternalTypes = [0]
  FullyConstrained = true
  MakeInternals = false
  MapMode = 5
  _ExternalGeoVersion = 0
  sketch-geometry (10):
    g0: LineSegment StartX=-57.65 StartY=-31.55 StartZ=0 EndX=57.65 EndY=-31.55 EndZ=0
    g1: LineSegment StartX=57.65 StartY=-31.55 StartZ=0 EndX=57.65 EndY=31.55 EndZ=0
    g2: LineSegment StartX=57.65 StartY=31.55 StartZ=0 EndX=-57.65 EndY=31.55 EndZ=0
    g3: LineSegment StartX=-57.65 StartY=31.55 StartZ=0 EndX=-57.65 EndY=-31.55 EndZ=0
    g4: GeomPoint [constr] X=0 Y=0 Z=0
    g5: LineSegment StartX=-64.65 StartY=-38.55 StartZ=0 EndX=64.65 EndY=-38.55 EndZ=0
    g6: LineSegment StartX=64.65 StartY=-38.55 StartZ=0 EndX=64.65 EndY=38.55 EndZ=0
    g7: LineSegment StartX=64.65 StartY=38.55 StartZ=0 EndX=-64.65 EndY=38.55 EndZ=0
    g8: LineSegment StartX=-64.65 StartY=38.55 StartZ=0 EndX=-64.65 EndY=-38.55 EndZ=0
    g9: GeomPoint [constr] X=0 Y=0 Z=0
  constraints (23):
    c: Coincident(g0,g1)
    c: Coincident(g1,g2)
    c: Coincident(g2,g3)
    c: Coincident(g3,g0)
    c: Horizontal(g0)
    c: Horizontal(g2)
    c: Vertical(g1)
    c: Vertical(g3)
    c: Symmetric(g2,g0,g4)
    c: Coincident(g4,g-1)
    c: Coincident(g5,g6)
    c: Coincident(g7,g8)
    c: Coincident(g8,g5)
    c: Horizontal(g5)
    c: Horizontal(g7)
    c: Vertical(g6)
    c: Vertical(g8)
    c: Symmetric(g7,g5,g9)
    c: Coincident(g9,g4)
    c: DistanceX(g1,g6) = 7
    c: DistanceY(g1,g6) = 7
    c: Coincident(g7,g6)
    c: Coincident(g6,g-3)
FEATURE [PartDesign::Pad] Pad016
  BaseFeature = -> Pad015
  Direction = (0,0,1)
  Length = 2
  Length2 = 10
  Profile = -> Sketch030
  ReferenceAxis = -> Sketch030 [N_Axis]
  Refine = true
  SideType = 0
  Suppressed = false
  Type = 0
  Type2 = 0
FEATURE [Sketcher::SketchObject] Sketch031
  ArcFitTolerance = 1e-06
  AttachmentSupport = -> [Pad016]
  ExternalGeometry = -> [Pad016]
  ExternalTypes = [0]
  FullyConstrained = true
  MakeInternals = false
  MapMode = 5
  Placement = pos=(0,0,2) rot=(0,0,1;0rad)
  _ExternalGeoVersion = 0
  sketch-geometry (7):
    g0: LineSegment StartX=-64.65 StartY=38.55 StartZ=0 EndX=-64.65 EndY=23.55 EndZ=0
    g1: LineSegment StartX=-64.65 StartY=23.55 StartZ=0 EndX=-59.65 EndY=23.55 EndZ=0
    g2: LineSegment StartX=-64.65 StartY=38.55 StartZ=0 EndX=-49.65 EndY=38.55 EndZ=0
    g3: LineSegment StartX=-49.65 StartY=38.55 StartZ=0 EndX=-49.65 EndY=33.55 EndZ=0
    g4: LineSegment StartX=-59.65 StartY=23.55 StartZ=0 EndX=-59.65 EndY=30.55 EndZ=0
    g5: ArcOfCircle CenterX=-56.65 CenterY=30.55 CenterZ=0 NormalX=0 NormalY=0 NormalZ=1 AngleXU=0 Radius=3 StartAngle=1.5708 EndAngle=3.14159
    g6: LineSegment StartX=-56.65 StartY=33.55 StartZ=0 EndX=-49.65 EndY=33.55 EndZ=0
  constraints (19):
    c: Coincident(g0,g-3)
    c: Vertical(g0)
    c: Coincident(g1,g0)
    c: Horizontal(g1)
    c: Coincident(g2,g0)
    c: Horizontal(g2)
    c: Coincident(g3,g2)
    c: Vertical(g3)
    c: Equal(g2,g0)
    c: Coincident(g1,g4)
    c: Vertical(g4)
    c: Tangent(g4,g5) = 1.5708
    c: Tangent(g5,g6) = 1.5708
    c: Horizontal(g6)
    c: Coincident(g6,g3)
    c: Radius(g5) = 3
    c: DistanceY(g0,g0) = 15
    c: Equal(g3,g1)
    c: DistanceX(g1,g1) = 5
FEATURE [PartDesign::Pad] Pad017
  BaseFeature = -> Pad016
  Direction = (0,-0.3,1)
  Length = 20
  Length2 = 10
  Profile = -> Sketch031
  ReferenceAxis = -> Sketch031 [N_Axis]
  Refine = true
  SideType = 0
  Suppressed = false
  Type = 0
  Type2 = 0
  UseCustomVector = true
FEATURE [Sketcher::SketchObject] Sketch033
  ArcFitTolerance = 1e-06
  AttachmentSupport = -> [XY_Plane005]
  ExternalGeometry = -> [Pocket018]
  ExternalTypes = [0]
  FullyConstrained = true
  MakeInternals = false
  MapMode = 5
  _ExternalGeoVersion = 0
  sketch-geometry (3):
    g0: LineSegment StartX=-62 StartY=-32.5005 StartZ=0 EndX=-62 EndY=15.0118 EndZ=0
    g1: ArcOfCircle CenterX=-42 CenterY=15.0118 CenterZ=0 NormalX=0 NormalY=0 NormalZ=1 AngleXU=0 Radius=20 StartAngle=1.5708 EndAngle=3.14159
    g2: LineSegment StartX=-42 StartY=35.0118 StartZ=0 EndX=48.4962 EndY=35.0118 EndZ=0
  constraints (7):
    c: Vertical(g0)
    c: Tangent(g0,g1) = 1.5708
    c: Tangent(g1,g2) = 1.5708
    c: Horizontal(g2)
    c: Equal(g-5,g1)
    c: Symmetric(g-6,g-6,g2)
    c: Symmetric(g-4,g-3,g0)
FEATURE [Sketcher::SketchObject] Sketch034
  ArcFitTolerance = 1e-06
  AttachmentOffset = pos=(0,0,-10) rot=(0,0,1;0rad)
  AttachmentSupport = -> [Pocket018]
  ExternalGeometry = -> [Pocket018]
  ExternalTypes = [0]
  FullyConstrained = true
  MakeInternals = false
  MapMode = 5
  Placement = pos=(0,-32.5,-2.2e-15) rot=(1,0,0;1.5708rad)
  _ExternalGeoVersion = 0
  sketch-geometry (4):
    g0: LineSegment StartX=-65 StartY=-2 StartZ=0 EndX=-59 EndY=-2 EndZ=0
    g1: LineSegment StartX=-59 StartY=-2 StartZ=0 EndX=-59 EndY=2 EndZ=0
    g2: LineSegment StartX=-59 StartY=2 StartZ=0 EndX=-65 EndY=2 EndZ=0
    g3: LineSegment StartX=-65 StartY=2 StartZ=0 EndX=-65 EndY=-2 EndZ=0
  constraints (10):
    c: Coincident(g0,g1)
    c: Coincident(g1,g2)
    c: Coincident(g2,g3)
    c: Coincident(g3,g0)
    c: Horizontal(g0)
    c: Horizontal(g2)
    c: Vertical(g1)
    c: Vertical(g3)
    c: Coincident(g0,g-6)
    c: Coincident(g1,g-3)
FEATURE [Sketcher::SketchObject] Sketch035
  ArcFitTolerance = 1e-06
  AttachmentSupport = -> [Pocket018]
  ExternalGeometry = -> [Sketch034,Sketch033,Pocket018]
  ExternalTypes = [0]
  FullyConstrained = true
  MakeInternals = false
  MapMode = 5
  Placement = pos=(36.4946,-9.77871,0) rot=(0.677661,0.519988,0.519988;1.95044rad)
  _ExternalGeoVersion = 0
  sketch-geometry (5):
    g0: LineSegment StartX=42.1206 StartY=-2 StartZ=0 EndX=50.6206 EndY=-2 EndZ=0
    g1: LineSegment StartX=50.6206 StartY=-2 StartZ=0 EndX=50.6206 EndY=2 EndZ=0
    g2: LineSegment StartX=50.6206 StartY=2 StartZ=0 EndX=42.1206 EndY=2 EndZ=0
    g3: GeomPoint [constr] X=46.3706 Y=3.6e-15 Z=0
    g4: LineSegment StartX=42.1206 StartY=2 StartZ=0 EndX=42.1206 EndY=-2 EndZ=0
  constraints (12):
    c: Coincident(g0,g1)
    c: Coincident(g1,g2)
    c: Horizontal(g0)
    c: Horizontal(g2)
    c: Vertical(g1)
    c: Symmetric(g2,g0,g3)
    c: Coincident(g3,g-5)
    c: Horizontal(g-3,g0)
    c: Coincident(g4,g2)
    c: Coincident(g4,g0)
    c: Vertical(g4)
    c: PointOnObject(g2,g-6)
FEATURE [PartDesign::SubtractivePipe] SubtractivePipe
  AuxiliaryCurvilinear = true
  AuxiliarySpineTangent = false
  BaseFeature = -> Pocket018
  Binormal = (0,0,0)
  Mode = 0
  Profile = -> Sketch034
  Refine = true
  Sections = -> [Sketch035]
  Spine = -> Sketch033
  SpineTangent = false
  Suppressed = false
  Transformation = 1
  Transition = 0
FEATURE [Sketcher::SketchObject] Sketch036
  ArcFitTolerance = 1e-06
  AttachmentSupport = -> [XY_Plane005]
  ExternalGeometry = -> [SubtractivePipe]
  ExternalTypes = [0]
  FullyConstrained = true
  MakeInternals = false
  MapMode = 5
  _ExternalGeoVersion = 0
  sketch-geometry (1):
    g0: LineSegment StartX=57.5118 StartY=25.9962 StartZ=0 EndX=62 EndY=-32.3815 EndZ=0
  constraints (2):
    c: Symmetric(g-3,g-3,g0)
    c: Symmetric(g-4,g-4,g0)
FEATURE [Sketcher::SketchObject] Sketch037
  ArcFitTolerance = 1e-06
  AttachmentOffset = pos=(0,0,-10) rot=(0,0,1;0rad)
  AttachmentSupport = -> [SubtractivePipe]
  ExternalGeometry = -> [SubtractivePipe,Sketch036]
  ExternalTypes = [0]
  FullyConstrained = true
  MakeInternals = false
  MapMode = 5
  Placement = pos=(0,-32.5,-2.2e-15) rot=(1,0,0;1.5708rad)
  _ExternalGeoVersion = 0
  sketch-geometry (5):
    g0: LineSegment StartX=65 StartY=-2 StartZ=0 EndX=65 EndY=2 EndZ=0
    g1: LineSegment StartX=65 StartY=2 StartZ=0 EndX=59 EndY=2 EndZ=0
    g2: LineSegment StartX=59 StartY=2 StartZ=0 EndX=59 EndY=-2 EndZ=0
    g3: LineSegment StartX=59 StartY=-2 StartZ=0 EndX=65 EndY=-2 EndZ=0
    g4: GeomPoint [constr] X=62 Y=0 Z=0
  constraints (11):
    c: Coincident(g0,g1)
    c: Coincident(g1,g2)
    c: Coincident(g2,g3)
    c: Coincident(g3,g0)
    c: Vertical(g0)
    c: Vertical(g2)
    c: Horizontal(g1)
    c: Horizontal(g3)
    c: Symmetric(g2,g0,g4)
    c: Coincident(g4,g-5)
    c: Coincident(g1,g-3)
FEATURE [Sketcher::SketchObject] Sketch038
  ArcFitTolerance = 1e-06
  AttachmentSupport = -> [SubtractivePipe]
  ExternalGeometry = -> [Sketch036,SubtractivePipe]
  ExternalTypes = [0]
  FullyConstrained = true
  MakeInternals = false
  MapMode = 5
  Placement = pos=(-2.64649,9.87684,0) rot=(-0.092692,0.704063,0.704063;3.32645rad)
  _ExternalGeoVersion = 0
  sketch-geometry (5):
    g0: LineSegment StartX=-66.5305 StartY=-2 StartZ=0 EndX=-58.0305 EndY=-2 EndZ=0
    g1: LineSegment StartX=-58.0305 StartY=-2 StartZ=0 EndX=-58.0305 EndY=2 EndZ=0
    g2: LineSegment StartX=-58.0305 StartY=2 StartZ=0 EndX=-66.5305 EndY=2 EndZ=0
    g3: LineSegment StartX=-66.5305 StartY=2 StartZ=0 EndX=-66.5305 EndY=-2 EndZ=0
    g4: GeomPoint [constr] X=-62.2805 Y=0 Z=0
  constraints (12):
    c: Coincident(g0,g1)
    c: Coincident(g1,g2)
    c: Coincident(g2,g3)
    c: Coincident(g3,g0)
    c: Horizontal(g0)
    c: Horizontal(g2)
    c: Vertical(g1)
    c: Vertical(g3)
    c: Symmetric(g2,g0,g4)
    c: Coincident(g4,g-5)
    c: PointOnObject(g2,g-6)
    c: Horizontal(g1,g-3)
FEATURE [PartDesign::SubtractivePipe] SubtractivePipe001
  AuxiliaryCurvilinear = true
  AuxiliarySpineTangent = false
  BaseFeature = -> SubtractivePipe
  Binormal = (0,0,0)
  Mode = 0
  Profile = -> Sketch037
  Refine = true
  Sections = -> [Sketch038]
  Spine = -> Sketch036
  SpineTangent = false
  Suppressed = false
  Transformation = 1
  Transition = 0
FEATURE [Sketcher::SketchObject] Sketch039
  ArcFitTolerance = 1e-06
  AttachmentSupport = -> [SubtractivePipe001]
  ExternalGeometry = -> [SubtractivePipe001]
  ExternalTypes = [0]
  FullyConstrained = true
  MakeInternals = false
  MapMode = 5
  Placement = pos=(0,47.5,0) rot=(0,0.707107,0.707107;3.14159rad)
  _ExternalGeoVersion = 0
  sketch-geometry (2):
    g0: Circle CenterX=58.3 CenterY=0 CenterZ=0 NormalX=0 NormalY=0 NormalZ=1 AngleXU=0 Radius=1.7
    g1: Circle CenterX=58.3 CenterY=0 CenterZ=0 NormalX=0 NormalY=0 NormalZ=1 AngleXU=0 Radius=1.5
  constraints (5):
    c: PointOnObject(g0,g-1)
    c: Coincident(g1,g0)
    c: Diameter(g1) = 3
    c: Diameter(g0) = 3.4
    c: Tangent(g0,g-3)
FEATURE [Sketcher::SketchObject] Sketch040
  ArcFitTolerance = 1e-06
  AttachmentSupport = -> [SubtractivePipe001]
  ExternalGeometry = -> [SubtractivePipe001]
  ExternalTypes = [0]
  FullyConstrained = true
  MakeInternals = false
  MapMode = 5
  Placement = pos=(-70,0,0) rot=(0.57735,-0.57735,-0.57735;2.0944rad)
  _ExternalGeoVersion = 0
  sketch-geometry (2):
    g0: Circle CenterX=-35.8 CenterY=0 CenterZ=0 NormalX=0 NormalY=0 NormalZ=1 AngleXU=0 Radius=1.7
    g1: Circle CenterX=-35.8 CenterY=0 CenterZ=0 NormalX=0 NormalY=0 NormalZ=1 AngleXU=0 Radius=1.5
  constraints (5):
    c: PointOnObject(g0,g-1)
    c: Coincident(g1,g0)
    c: Diameter(g1) = 3
    c: Diameter(g0) = 3.4
    c: Tangent(g0,g-3)
FEATURE [PartDesign::Pocket] Pocket019
  BaseFeature = -> SubtractivePipe001
  Direction = (0,-1,2e-16)
  Length = 9
  Length2 = 5
  Profile = -> Sketch039 [Edge2]
  ReferenceAxis = -> Sketch039 [N_Axis]
  Refine = true
  SideType = 0
  Suppressed = false
  Type = 0
  Type2 = 0
FEATURE [PartDesign::Pocket] Pocket020
  BaseFeature = -> Pocket019
  Direction = (0,-1,2e-16)
  Length = 8
  Length2 = 5
  Profile = -> Sketch039 [Edge1]
  ReferenceAxis = -> Sketch039 [N_Axis]
  Refine = true
  SideType = 0
  Suppressed = false
  Type = 0
  Type2 = 0
FEATURE [PartDesign::Pocket] Pocket021
  BaseFeature = -> Pocket020
  Direction = (1,0,0)
  Length = 9
  Length2 = 5
  Profile = -> Sketch040 [Edge2]
  ReferenceAxis = -> Sketch040 [N_Axis]
  Refine = true
  SideType = 0
  Suppressed = false
  Type = 0
  Type2 = 0
FEATURE [PartDesign::Pocket] Pocket022
  BaseFeature = -> Pocket021
  Direction = (1,0,0)
  Length = 8
  Length2 = 5
  Profile = -> Sketch040 [Edge1]
  ReferenceAxis = -> Sketch040 [N_Axis]
  Refine = true
  SideType = 0
  Suppressed = false
  Type = 0
  Type2 = 0
FEATURE [PartDesign::Fillet] Fillet004
  Base = -> Pocket022 [Edge59,Edge80]
  BaseFeature = -> Pocket022
  Radius = 5
  Refine = true
  SupportTransform = false
  Suppressed = false
  UseAllEdges = false
FEATURE [PartDesign::Body] Body004  label="IrSensor"
  AllowCompound = false
  Group = -> [Sketch016,Pad014,Sketch017,Pocket015,Pocket016,Mirrored006,Sketch019,Pocket017,Sketch020,Pocket018,Sketch033,Sketch034,Sketch035,SubtractivePipe,Sketch036,Sketch037,Sketch038,SubtractivePipe001,Sketch039,Sketch040,Pocket019,Pocket020,Pocket021,Pocket022,Fillet004]
  Origin = -> Origin005
  Tip = -> Fillet004
FEATURE [Sketcher::SketchObject] Sketch041
  ArcFitTolerance = 1e-06
  AttachmentSupport = -> [Pocket009]
  ExternalGeometry = -> [Pocket009]
  ExternalTypes = [0]
  FullyConstrained = true
  MakeInternals = false
  MapMode = 5
  Placement = pos=(0,0,4) rot=(0,0,1;0rad)
  _ExternalGeoVersion = 0
  sketch-geometry (21):
    g0: LineSegment StartX=-34.1491 StartY=9.5 StartZ=0 EndX=-37.3246 EndY=15 EndZ=0
    g1: LineSegment StartX=-37.3246 StartY=15 StartZ=0 EndX=-43.6754 EndY=15 EndZ=0
    g2: LineSegment StartX=-43.6754 StartY=15 StartZ=0 EndX=-46.8509 EndY=9.5 EndZ=0
    g3: LineSegment StartX=-46.8509 StartY=9.5 StartZ=0 EndX=-43.6754 EndY=4 EndZ=0
    g4: LineSegment StartX=-43.6754 StartY=4 StartZ=0 EndX=-37.3246 EndY=4 EndZ=0
    g5: LineSegment StartX=-37.3246 StartY=4 StartZ=0 EndX=-34.1491 EndY=9.5 EndZ=0
    g6: Circle [constr] CenterX=-40.5 CenterY=9.5 CenterZ=0 NormalX=0 NormalY=0 NormalZ=1 AngleXU=0 Radius=6.35085
    g7: LineSegment StartX=21.7561 StartY=9.5 StartZ=0 EndX=17.6281 EndY=16.65 EndZ=0
    g8: LineSegment StartX=17.6281 StartY=16.65 StartZ=0 EndX=9.37195 EndY=16.65 EndZ=0
    g9: LineSegment StartX=9.37195 StartY=16.65 StartZ=0 EndX=5.24389 EndY=9.5 EndZ=0
    g10: LineSegment StartX=5.24389 StartY=9.5 StartZ=0 EndX=9.37195 EndY=2.35 EndZ=0
    g11: LineSegment StartX=9.37195 StartY=2.35 StartZ=0 EndX=17.6281 EndY=2.35 EndZ=0
    g12: LineSegment StartX=17.6281 StartY=2.35 StartZ=0 EndX=21.7561 EndY=9.5 EndZ=0
    g13: Circle [constr] CenterX=13.5 CenterY=9.5 CenterZ=0 NormalX=0 NormalY=0 NormalZ=1 AngleXU=0 Radius=8.25611
    g14: LineSegment StartX=49.1603 StartY=9.5 StartZ=0 EndX=44.8301 EndY=17 EndZ=0
    g15: LineSegment StartX=44.8301 StartY=17 StartZ=0 EndX=36.1699 EndY=17 EndZ=0
    g16: LineSegment StartX=36.1699 StartY=17 StartZ=0 EndX=31.8397 EndY=9.5 EndZ=0
    g17: LineSegment StartX=31.8397 StartY=9.5 StartZ=0 EndX=36.1699 EndY=2 EndZ=0
    g18: LineSegment StartX=36.1699 StartY=2 StartZ=0 EndX=44.8301 EndY=2 EndZ=0
    g19: LineSegment StartX=44.8301 StartY=2 StartZ=0 EndX=49.1603 EndY=9.5 EndZ=0
    g20: Circle [constr] CenterX=40.5 CenterY=9.5 CenterZ=0 NormalX=0 NormalY=0 NormalZ=1 AngleXU=0 Radius=8.66025
  constraints (48):
    c: Coincident(g0,g1)
    c: Coincident(g1,g2)
    c: Coincident(g2,g3)
    c: Coincident(g3,g4)
    c: Coincident(g4,g5)
    c: Coincident(g5,g0)
    c: Equal(g0, g1-g5) x5
    c: PointOnObject(g0,g6)
    c: PointOnObject(g1,g6)
    c: PointOnObject(g2,g6)
    c: PointOnObject(g3,g6)
    c: PointOnObject(g4,g6)
    c: PointOnObject(g5,g6)
    c: Coincident(g6,g-3)
    c: Coincident(g7,g8)
    c: Coincident(g8,g9)
    c: Coincident(g9,g10)
    c: Coincident(g10,g11)
    c: Coincident(g11,g12)
    c: Coincident(g12,g7)
    c: Equal(g7, g8-g12) x5
    c: PointOnObject(g7,g13)
    c: PointOnObject(g8,g13)
    c: PointOnObject(g9,g13)
    c: PointOnObject(g10,g13)
    c: PointOnObject(g11,g13)
    c: PointOnObject(g12,g13)
    c: Coincident(g13,g-4)
    c: Coincident(g14,g15)
    c: Coincident(g15,g16)
    c: Coincident(g16,g17)
    c: Coincident(g17,g18)
    c: Coincident(g18,g19)
    c: Coincident(g19,g14)
    c: Equal(g14, g15-g19) x5
    c: PointOnObject(g14,g20)
    c: PointOnObject(g15,g20)
    c: PointOnObject(g16,g20)
    c: PointOnObject(g17,g20)
    c: PointOnObject(g18,g20)
    c: PointOnObject(g19,g20)
    c: Coincident(g20,g-5)
    c: Horizontal(g4)
    c: Horizontal(g11)
    c: Horizontal(g18)
    c: DistanceY(g4,g0) = 11
    c: DistanceY(g11,g7) = 14.3
    c: DistanceY(g18,g14) = 15
FEATURE [PartDesign::Pocket] Pocket023
  BaseFeature = -> Pocket009
  Direction = (0,0,-1)
  Length = 2.5
  Length2 = 5
  Profile = -> Sketch041
  ReferenceAxis = -> Sketch041 [N_Axis]
  Refine = true
  SideType = 0
  Suppressed = false
  Type = 0
  Type2 = 0
FEATURE [PartDesign::Fillet] Fillet002
  Base = -> PolarPattern [Face22,Face11,Face9,Face7,Face5,Face3,Face21,Face19,Face17,Face15,Face13]
  BaseFeature = -> PolarPattern
  Radius = 1
  Refine = true
  SupportTransform = false
  Suppressed = false
  UseAllEdges = false
FEATURE [Sketcher::SketchObject] Sketch015
  ArcFitTolerance = 1e-06
  AttachmentSupport = -> [Fillet002]
  ExternalTypes = [0]
  FullyConstrained = true
  MakeInternals = false
  MapMode = 5
  _ExternalGeoVersion = 0
  sketch-geometry (9):
    g0: Circle CenterX=0 CenterY=0 CenterZ=0 NormalX=0 NormalY=0 NormalZ=1 AngleXU=0 Radius=4.85
    g1: Circle CenterX=0 CenterY=0 CenterZ=0 NormalX=0 NormalY=0 NormalZ=1 AngleXU=0 Radius=2.75
    g2: LineSegment StartX=2.6 StartY=1.50111 StartZ=0 EndX=4.237e-13 EndY=3.00222 EndZ=0
    g3: LineSegment StartX=4.237e-13 StartY=3.00222 StartZ=0 EndX=-2.6 EndY=1.50111 EndZ=0
    g4: LineSegment StartX=-2.6 StartY=1.50111 StartZ=0 EndX=-2.6 EndY=-1.50111 EndZ=0
    g5: LineSegment StartX=-2.6 StartY=-1.50111 StartZ=0 EndX=1.88329e-11 EndY=-3.00222 EndZ=0
    g6: LineSegment StartX=1.88329e-11 StartY=-3.00222 StartZ=0 EndX=2.6 EndY=-1.50111 EndZ=0
    g7: LineSegment StartX=2.6 StartY=-1.50111 StartZ=0 EndX=2.6 EndY=1.50111 EndZ=0
    g8: Circle [constr] CenterX=0 CenterY=0 CenterZ=0 NormalX=0 NormalY=0 NormalZ=1 AngleXU=0 Radius=3.00222
  constraints (20):
    c: Diameter(g0) = 9.7
    c: Coincident(g0,g-1)
    c: Diameter(g1) = 5.5
    c: Coincident(g1,g0)
    c: Coincident(g2,g3)
    c: Coincident(g3,g4)
    c: Coincident(g4,g5)
    c: Coincident(g5,g6)
    c: Coincident(g6,g7)
    c: Coincident(g7,g2)
    c: Equal(g2, g3-g7) x5
    c: PointOnObject(g2,g8)
    c: PointOnObject(g3,g8)
    c: PointOnObject(g4,g8)
    c: PointOnObject(g5,g8)
    c: PointOnObject(g6,g8)
    c: PointOnObject(g7,g8)
    c: Coincident(g8,g0)
    c: Horizontal(g3,g2)
    c: DistanceX(g3,g2) = 5.2
FEATURE [Sketcher::SketchObject] Sketch042
  ArcFitTolerance = 1e-06
  AttachmentOffset = pos=(0,0,7) rot=(0,0,1;0rad)
  AttachmentSupport = -> [Pocket023]
  ExternalGeometry = -> [Pocket023]
  ExternalTypes = [0]
  FullyConstrained = true
  MakeInternals = false
  MapMode = 5
  Placement = pos=(0,26.5,1.6e-15) rot=(1,0,0;1.5708rad)
  _ExternalGeoVersion = 0
  sketch-geometry (18):
    g0: LineSegment StartX=-37.5 StartY=48 StartZ=0 EndX=-37.5 EndY=4 EndZ=0
    g1: LineSegment [constr] StartX=-37.5 StartY=4 StartZ=0 EndX=-6.5 EndY=4 EndZ=0
    g2: LineSegment StartX=6.5 StartY=48 StartZ=0 EndX=6.5 EndY=4 EndZ=0
    g3: LineSegment [constr] StartX=6.5 StartY=4 StartZ=0 EndX=37.5 EndY=4 EndZ=0
    g4: LineSegment StartX=37.5 StartY=4 StartZ=0 EndX=37.5 EndY=48 EndZ=0
    g5: LineSegment StartX=-39.5 StartY=48 StartZ=0 EndX=-39.5 EndY=4 EndZ=0
    g6: LineSegment StartX=-6.5 StartY=48 StartZ=0 EndX=-6.5 EndY=4 EndZ=0
    g7: LineSegment StartX=39.5 StartY=4 StartZ=0 EndX=39.5 EndY=48 EndZ=0
    g8: LineSegment StartX=4.5 StartY=20 StartZ=0 EndX=4.5 EndY=48 EndZ=0
    g9: LineSegment StartX=-37.5 StartY=48 StartZ=0 EndX=-39.5 EndY=48 EndZ=0
    g10: LineSegment StartX=-4.5 StartY=48 StartZ=0 EndX=-6.5 EndY=48 EndZ=0
    g11: LineSegment StartX=4.5 StartY=48 StartZ=0 EndX=6.5 EndY=48 EndZ=0
    g12: LineSegment StartX=37.5 StartY=48 StartZ=0 EndX=39.5 EndY=48 EndZ=0
    g13: LineSegment StartX=-4.5 StartY=48 StartZ=0 EndX=-4.5 EndY=20 EndZ=0
    g14: LineSegment StartX=-4.5 StartY=20 StartZ=0 EndX=4.5 EndY=20 EndZ=0
    g15: LineSegment StartX=-39.5 StartY=4 StartZ=0 EndX=-37.5 EndY=4 EndZ=0
    g16: LineSegment StartX=-6.5 StartY=4 StartZ=0 EndX=6.5 EndY=4 EndZ=0
    g17: LineSegment StartX=37.5 StartY=4 StartZ=0 EndX=39.5 EndY=4 EndZ=0
  constraints (51):
    c: Coincident(g0,g1)
    c: Vertical(g0)
    c: Coincident(g2,g3)
    c: Coincident(g3,g4)
    c: Vertical(g4)
    c: Horizontal(g3)
    c: Vertical(g5)
    c: Vertical(g6)
    c: Vertical(g7)
    c: DistanceX(g4,g7) = 2
    c: Coincident(g1,g6)
    c: Vertical(g8)
    c: Horizontal(g-3,g5)
    c: Vertical(g2)
    c: Coincident(g9,g0)
    c: Horizontal(g9)
    c: Coincident(g5,g9)
    c: Coincident(g11,g8)
    c: Coincident(g11,g2)
    c: Horizontal(g11)
    c: Coincident(g12,g4)
    c: Coincident(g12,g7)
    c: Horizontal(g12)
    c: Horizontal(g2,g4)
    c: Equal(g12,g11)
    c: Equal(g10,g11)
    c: Equal(g10,g9)
    c: DistanceY(g0,g0) = 44
    c: Horizontal(g1)
    c: Coincident(g6,g10)
    c: Horizontal(g10)
    c: Horizontal(g0,g6)
    c: Equal(g1,g3)
    c: DistanceX(g1,g1) = 31
    c: Symmetric(g10,g8,g-2)
    c: Coincident(g13,g10)
    c: Vertical(g13)
    c: Horizontal(g1,g2)
    c: DistanceY(g8,g8) = 28
    c: Horizontal(g13,g8)
    c: Coincident(g14,g13)
    c: Coincident(g14,g8)
    c: Coincident(g15,g5)
    c: Coincident(g15,g0)
    c: Coincident(g16,g1)
    c: Coincident(g16,g2)
    c: Coincident(g17,g3)
    c: Coincident(g17,g7)
    c: Horizontal(g17)
    c: Horizontal(g15)
    c: DistanceX(g14,g14) = 9
FEATURE [PartDesign::Pad] Pad018
  BaseFeature = -> Pocket023
  Direction = (0,-1,2e-16)
  Length = 10
  Length2 = 10
  Profile = -> Sketch042
  ReferenceAxis = -> Sketch042 [N_Axis]
  Refine = true
  Reversed = true
  SideType = 0
  Suppressed = false
  Type = 2
  Type2 = 0
FEATURE [Sketcher::SketchObject] Sketch001
  ArcFitTolerance = 1e-06
  AttachmentSupport = -> [XY_Plane001]
  ExternalTypes = [0]
  FullyConstrained = true
  MakeInternals = false
  MapMode = 5
  _ExternalGeoVersion = 0
  sketch-geometry (15):
    g0: LineSegment StartX=-62.65 StartY=-36.55 StartZ=0 EndX=62.65 EndY=-36.55 EndZ=0
    g1: LineSegment StartX=62.65 StartY=-36.55 StartZ=0 EndX=62.65 EndY=36.55 EndZ=0
    g2: LineSegment StartX=62.65 StartY=36.55 StartZ=0 EndX=-62.65 EndY=36.55 EndZ=0
    g3: LineSegment StartX=-62.65 StartY=36.55 StartZ=0 EndX=-62.65 EndY=-36.55 EndZ=0
    g4: GeomPoint [constr] X=0 Y=0 Z=0
    g5: LineSegment StartX=-62.65 StartY=-39.55 StartZ=0 EndX=62.65 EndY=-39.55 EndZ=0
    g6: LineSegment StartX=65.65 StartY=-36.55 StartZ=0 EndX=65.65 EndY=36.55 EndZ=0
    g7: LineSegment StartX=62.65 StartY=39.55 StartZ=0 EndX=-62.65 EndY=39.55 EndZ=0
    g8: LineSegment StartX=-65.65 StartY=36.55 StartZ=0 EndX=-65.65 EndY=-36.55 EndZ=0
    g9: ArcOfCircle CenterX=-62.65 CenterY=-36.55 CenterZ=0 NormalX=0 NormalY=0 NormalZ=1 AngleXU=0 Radius=3 StartAngle=3.14159 EndAngle=4.71239
    g10: ArcOfCircle CenterX=62.65 CenterY=-36.55 CenterZ=0 NormalX=0 NormalY=0 NormalZ=1 AngleXU=0 Radius=3 StartAngle=4.71239 EndAngle=6.28319
    g11: ArcOfCircle CenterX=62.65 CenterY=36.55 CenterZ=0 NormalX=0 NormalY=0 NormalZ=1 AngleXU=0 Radius=3 StartAngle=0 EndAngle=1.5708
    g12: ArcOfCircle CenterX=-62.65 CenterY=36.55 CenterZ=0 NormalX=0 NormalY=0 NormalZ=1 AngleXU=0 Radius=3 StartAngle=1.5708 EndAngle=3.14159
    g13: GeomPoint [constr] X=-65.65 Y=-39.55 Z=0
    g14: GeomPoint [constr] X=65.65 Y=39.55 Z=0
  constraints (35):
    c: Coincident(g0,g1)
    c: Coincident(g1,g2)
    c: Coincident(g2,g3)
    c: Coincident(g3,g0)
    c: Horizontal(g0)
    c: Horizontal(g2)
    c: Vertical(g1)
    c: Vertical(g3)
    c: Symmetric(g2,g0,g4)
    c: Distance(g1,g3) = 125.3  'display_inner_length'
    c: Coincident(g4,g-1)
    c: DistanceY(g3,g3) = 73.1  'display_inner_width'
    c: Tangent(g5,g9) = -1.5708
    c: Tangent(g5,g10) = -1.5708
    c: Tangent(g6,g10) = -1.5708
    c: Tangent(g6,g11) = -1.5708
    c: Tangent(g7,g11) = -1.5708
    c: Tangent(g7,g12) = -1.5708
    c: Tangent(g8,g12) = -1.5708
    c: Tangent(g8,g9) = -1.5708
    c: Horizontal(g5)
    c: Horizontal(g7)
    c: Vertical(g6)
    c: Vertical(g8)
    c: Equal(g9,g10)
    c: Equal(g10,g11)
    c: Equal(g11,g12)
    c: PointOnObject(g13,g5)
    c: PointOnObject(g13,g8)
    c: PointOnObject(g14,g6)
    c: PointOnObject(g14,g7)
    c: Symmetric(g13,g14,g4)
    c: Radius(g11) = 3
    c: Distance(g1,g7) = 3
    c: DistanceX(g1,g6) = 3
FEATURE [PartDesign::Pad] Pad
  Direction = (0,0,1)
  Length = 3
  Length2 = 10
  Profile = -> Sketch001 [Edge11,Edge12,Edge5,Edge9,Edge10,Edge7,Edge8,Edge6]
  ReferenceAxis = -> Sketch001 [N_Axis]
  Refine = true
  SideType = 0
  Suppressed = false
  Type = 0
  Type2 = 0
FEATURE [PartDesign::Pad] Pad001
  BaseFeature = -> Pad
  Direction = (0,0,1)
  Length = 30
  Length2 = 10
  Profile = -> Sketch001
  ReferenceAxis = -> Sketch001 [N_Axis]
  Refine = true
  SideType = 0
  Suppressed = false
  Type = 0
  Type2 = 0
FEATURE [Sketcher::SketchObject] Sketch002
  ArcFitTolerance = 1e-06
  AttachmentSupport = -> [Pad001]
  ExternalGeometry = -> [Pad001]
  ExternalTypes = [0]
  FullyConstrained = true
  MakeInternals = false
  MapMode = 5
  Placement = pos=(0,0,0) rot=(1,0,0;3.14159rad)
  _ExternalGeoVersion = 0
  sketch-geometry (19):
    g0: LineSegment [constr] StartX=-59.65 StartY=30 StartZ=0 EndX=38.35 EndY=30 EndZ=0
    g1: LineSegment [constr] StartX=38.35 StartY=30 StartZ=0 EndX=38.35 EndY=-30 EndZ=0
    g2: LineSegment [constr] StartX=38.35 StartY=-30 StartZ=0 EndX=-59.65 EndY=-30 EndZ=0
    g3: LineSegment [constr] StartX=-59.65 StartY=-30 StartZ=0 EndX=-59.65 EndY=30 EndZ=0
    g4: LineSegment [constr] StartX=40.45 StartY=-1.85 StartZ=0 EndX=59.65 EndY=-1.85 EndZ=0
    g5: LineSegment [constr] StartX=59.65 StartY=-1.85 StartZ=0 EndX=59.65 EndY=-23.25 EndZ=0
    g6: LineSegment [constr] StartX=59.65 StartY=-23.25 StartZ=0 EndX=40.45 EndY=-23.25 EndZ=0
    g7: LineSegment [constr] StartX=40.45 StartY=-23.25 StartZ=0 EndX=40.45 EndY=-1.85 EndZ=0
    g8: LineSegment [constr] StartX=42.3 StartY=-6.65 StartZ=0 EndX=54.2 EndY=-6.65 EndZ=0
    g9: LineSegment [constr] StartX=54.2 StartY=-6.65 StartZ=0 EndX=54.2 EndY=-18.55 EndZ=0
    g10: LineSegment [constr] StartX=54.2 StartY=-18.55 StartZ=0 EndX=42.3 EndY=-18.55 EndZ=0
    g11: LineSegment [constr] StartX=42.3 StartY=-18.55 StartZ=0 EndX=42.3 EndY=-6.65 EndZ=0
    g12: Circle CenterX=48.25 CenterY=-12.6 CenterZ=0 NormalX=0 NormalY=0 NormalZ=1 AngleXU=0 Radius=3.475
    g13: LineSegment StartX=-48.65 StartY=12.6 StartZ=0 EndX=27.35 EndY=12.6 EndZ=0
    g14: LineSegment StartX=27.35 StartY=12.6 StartZ=0 EndX=27.35 EndY=-12.6 EndZ=0
    g15: LineSegment StartX=27.35 StartY=-12.6 StartZ=0 EndX=-48.65 EndY=-12.6 EndZ=0
    g16: LineSegment StartX=-48.65 StartY=-12.6 StartZ=0 EndX=-48.65 EndY=12.6 EndZ=0
    g17: GeomPoint [constr] X=-10.65 Y=0 Z=0
    g18: GeomPoint [constr] X=48.25 Y=-9.125 Z=0
  constraints (52):
    c: Coincident(g0,g1)
    c: Coincident(g1,g2)
    c: Coincident(g2,g3)
    c: Coincident(g3,g0)
    c: Horizontal(g0)
    c: Horizontal(g2)
    c: Vertical(g1)
    c: Vertical(g3)
    c: Coincident(g4,g5)
    c: Coincident(g5,g6)
    c: Coincident(g6,g7)
    c: Coincident(g7,g4)
    c: Horizontal(g4)
    c: Horizontal(g6)
    c: Vertical(g5)
    c: Vertical(g7)
    c: Coincident(g8,g9)
    c: Coincident(g9,g10)
    c: Coincident(g10,g11)
    c: Coincident(g11,g8)
    c: Horizontal(g8)
    c: Horizontal(g10)
    c: Vertical(g9)
    c: Vertical(g11)
    c: Coincident(g13,g14)
    c: Coincident(g14,g15)
    c: Coincident(g15,g16)
    c: Coincident(g16,g13)
    c: Horizontal(g13)
    c: Horizontal(g15)
    c: Vertical(g14)
    c: Vertical(g16)
    c: Distance(g2) = 98
    c: Distance(g1) = 60
    c: Distance(g15) = 76
    c: Distance(g14) = 25.2
    c: Symmetric(g0,g1,g17)
    c: Symmetric(g13,g14,g17)
    c: Distance(g6) = 19.2
    c: Distance(g5) = 21.4
    c: Distance(g10) = 11.9
    c: Distance(g9) = 11.9
    c: Diameter(g12) = 6.95
    c: Symmetric(g8,g9,g12)
    c: DistanceY(g5,g9) = 4.7
    c: DistanceX(g9,g5) = 5.45
    c: PointOnObject(g18,g12)
    c: Vertical(g12,g18)
    c: Horizontal(g17,g-1)
    c: Horizontal(g12,g14)
    c: DistanceX(g-3,g2) = 6
    c: DistanceX(g4,g-4) = 6
FEATURE [PartDesign::Pocket] Pocket
  BaseFeature = -> Pad001
  Direction = (0,0,1)
  Length = 5
  Length2 = 5
  Profile = -> Sketch002
  ReferenceAxis = -> Sketch002 [N_Axis]
  Refine = true
  SideType = 0
  Suppressed = false
  Type = 1
  Type2 = 0
FEATURE [PartDesign::Plane] DatumPlane
  AttachmentSupport = -> [Pocket]
  Length = 99.4822
  MapMode = 45
  Placement = pos=(-10.65,1.8e-15,3) rot=(0,0,1;1.5708rad)
  ResizeMode = 0
  Width = 151.682
FEATURE [Sketcher::SketchObject] Sketch003
  ArcFitTolerance = 1e-06
  AttachmentOffset = pos=(0,0,9.4) rot=(0,0,1;0rad)
  AttachmentSupport = -> [DatumPlane]
  ExternalTypes = [0]
  FullyConstrained = true
  MakeInternals = false
  MapMode = 5
  Placement = pos=(-10.65,1.8e-15,12.4) rot=(0,0,1;1.5708rad)
  _ExternalGeoVersion = 0
  sketch-geometry (3):
    g0: Circle CenterX=-27.5 CenterY=46.5 CenterZ=0 NormalX=0 NormalY=0 NormalZ=1 AngleXU=0 Radius=4
    g1: Circle CenterX=-27.5 CenterY=46.5 CenterZ=0 NormalX=0 NormalY=0 NormalZ=1 AngleXU=0 Radius=1.7
    g2: Circle CenterX=-27.5 CenterY=46.5 CenterZ=0 NormalX=0 NormalY=0 NormalZ=1 AngleXU=0 Radius=1.5
  constraints (7):
    c: Coincident(g1,g0)
    c: DistanceX(g0,g-1) = 27.5
    c: DistanceY(g-1,g0) = 46.5
    c: Diameter(g0) = 8
    c: Diameter(g1) = 3.4
    c: Coincident(g2,g0)
    c: Diameter(g2) = 3
FEATURE [PartDesign::Pad] Pad002
  BaseFeature = -> Pocket
  Direction = (0,0,1)
  Length = 10
  Length2 = 10
  Profile = -> Sketch003 [Edge1]
  ReferenceAxis = -> Sketch003 [N_Axis]
  Refine = true
  Reversed = true
  SideType = 0
  Suppressed = false
  Type = 2
  Type2 = 0
FEATURE [PartDesign::Pocket] Pocket001
  BaseFeature = -> Pad002
  Direction = (0,0,-1)
  Length = 0
  Length2 = 5
  Profile = -> Sketch003 [Edge3]
  ReferenceAxis = -> Sketch003 [N_Axis]
  Refine = true
  SideType = 0
  Suppressed = false
  Type = 3
  Type2 = 0
  UpToFace = -> Pad002 [Face15]
FEATURE [PartDesign::Pocket] Pocket002
  BaseFeature = -> Pocket001
  Direction = (0,0,-1)
  Length = 4
  Length2 = 5
  Profile = -> Sketch003 [Edge2]
  ReferenceAxis = -> Sketch003 [N_Axis]
  Refine = true
  SideType = 0
  Suppressed = false
  Type = 0
  Type2 = 0
FEATURE [PartDesign::Mirrored] Mirrored
  MirrorPlane = -> Sketch003 [V_Axis]
  Refine = true
  Suppressed = false
  TransformMode = 0
FEATURE [PartDesign::Mirrored] Mirrored001
  MirrorPlane = -> Sketch003 [H_Axis]
  Refine = true
  Suppressed = false
  TransformMode = 0
FEATURE [PartDesign::MultiTransform] MultiTransform
  BaseFeature = -> Pocket002
  Originals = -> [Pad002,Pocket002,Pocket001]
  Refine = true
  Suppressed = false
  TransformMode = 0
  Transformations = -> [Mirrored,Mirrored001]
FEATURE [Sketcher::SketchObject] Sketch004
  ArcFitTolerance = 1e-06
  AttachmentSupport = -> [MultiTransform]
  ExternalGeometry = -> [MultiTransform]
  ExternalTypes = [0]
  FullyConstrained = true
  MakeInternals = false
  MapMode = 5
  Placement = pos=(0,0,3) rot=(0,0,1;0rad)
  _ExternalGeoVersion = 0
  sketch-geometry (2):
    g0: Circle CenterX=48.25 CenterY=-12.6 CenterZ=0 NormalX=0 NormalY=0 NormalZ=1 AngleXU=0 Radius=2.55
    g1: Circle CenterX=48.25 CenterY=-12.6 CenterZ=0 NormalX=0 NormalY=0 NormalZ=1 AngleXU=0 Radius=3.5
  constraints (5):
    c: Coincident(g1,g0)
    c: Horizontal(g-4,g0)
    c: Vertical(g0,g-3)
    c: Diameter(g0) = 5.1
    c: Diameter(g1) = 7
FEATURE [PartDesign::Pocket] Pocket003
  BaseFeature = -> MultiTransform
  Direction = (0,0,-1)
  Length = 5
  Length2 = 5
  Offset = -0.2
  Profile = -> Sketch004 [Edge1]
  ReferenceAxis = -> Sketch004 [N_Axis]
  Refine = true
  SideType = 0
  Suppressed = false
  Type = 2
  Type2 = 0
FEATURE [PartDesign::Pad] Pad003
  BaseFeature = -> Pocket003
  Direction = (0,0,1)
  Length = 1.2
  Length2 = 10
  Profile = -> Sketch004 [Edge2,Edge1]
  ReferenceAxis = -> Sketch004 [N_Axis]
  Refine = true
  SideType = 0
  Suppressed = false
  Type = 0
  Type2 = 0
FEATURE [Sketcher::SketchObject] Sketch005
  ArcFitTolerance = 1e-06
  AttachmentSupport = -> [YZ_Plane001]
  ExternalGeometry = -> [Pad003]
  ExternalTypes = [0]
  FullyConstrained = true
  MakeInternals = false
  MapMode = 5
  Placement = pos=(0,0,0) rot=(0.57735,0.57735,0.57735;2.0944rad)
  _ExternalGeoVersion = 0
  sketch-geometry (7):
    g0: LineSegment StartX=-39.55 StartY=19.5 StartZ=0 EndX=-10 EndY=19.5 EndZ=0
    g1: ArcOfCircle CenterX=0 CenterY=19.5 CenterZ=0 NormalX=0 NormalY=0 NormalZ=1 AngleXU=0 Radius=10 StartAngle=0 EndAngle=3.14159
    g2: LineSegment StartX=10 StartY=19.5 StartZ=0 EndX=39.55 EndY=19.5 EndZ=0
    g3: LineSegment StartX=39.55 StartY=19.5 StartZ=0 EndX=39.55 EndY=30 EndZ=0
    g4: LineSegment StartX=39.55 StartY=30 StartZ=0 EndX=-39.55 EndY=30 EndZ=0
    g5: LineSegment StartX=-39.55 StartY=30 StartZ=0 EndX=-39.55 EndY=19.5 EndZ=0
    g6: Circle CenterX=0 CenterY=19.5 CenterZ=0 NormalX=0 NormalY=0 NormalZ=1 AngleXU=0 Radius=1.5
  constraints (16):
    c: Horizontal(g0)
    c: Perpendicular(g0,g1) = 4.71239
    c: Perpendicular(g1,g2) = 4.71239
    c: Coincident(g2,g3)
    c: Vertical(g3)
    c: Coincident(g3,g4)
    c: Coincident(g4,g5)
    c: Coincident(g5,g0)
    c: Vertical(g5)
    c: Radius(g1) = 10
    c: Coincident(g4,g-3)
    c: Symmetric(g4,g3,g-2)
    c: Symmetric(g0,g2,g1)
    c: DistanceY(g5,g5) = 10.5
    c: Coincident(g6,g1)
    c: Diameter(g6) = 3
FEATURE [PartDesign::Pocket] Pocket004
  BaseFeature = -> Pad003
  Direction = (-1,0,0)
  Length = 5
  Length2 = 5
  Profile = -> Sketch005
  ReferenceAxis = -> Sketch005 [N_Axis]
  Refine = true
  SideType = 2
  Suppressed = false
  Type = 1
  Type2 = 0
FEATURE [PartDesign::Fillet] Fillet
  Base = -> Pocket004 [Edge77]
  BaseFeature = -> Pocket004
  Radius = 3
  Refine = true
  SupportTransform = false
  Suppressed = false
  UseAllEdges = false
FEATURE [Sketcher::SketchObject] Sketch006
  ArcFitTolerance = 1e-06
  AttachmentSupport = -> [Fillet]
  ExternalGeometry = -> [Fillet]
  ExternalTypes = [0]
  FullyConstrained = true
  MakeInternals = false
  MapMode = 5
  Placement = pos=(0,0,3) rot=(0,0,1;0rad)
  _ExternalGeoVersion = 0
  sketch-geometry (4):
    g0: LineSegment StartX=62.65 StartY=-36.55 StartZ=0 EndX=62.65 EndY=-33.55 EndZ=0
    g1: LineSegment StartX=62.65 StartY=-33.55 StartZ=0 EndX=59.65 EndY=-33.55 EndZ=0
    g2: LineSegment StartX=59.65 StartY=-33.55 StartZ=0 EndX=59.65 EndY=-36.55 EndZ=0
    g3: LineSegment StartX=59.65 StartY=-36.55 StartZ=0 EndX=62.65 EndY=-36.55 EndZ=0
  constraints (11):
    c: Coincident(g0,g1)
    c: Coincident(g1,g2)
    c: Coincident(g2,g3)
    c: Coincident(g3,g0)
    c: Vertical(g0)
    c: Vertical(g2)
    c: Horizontal(g1)
    c: Horizontal(g3)
    c: Distance(g0,g2) = 3
    c: Distance(g1,g3) = 3
    c: Coincident(g0,g-3)
FEATURE [PartDesign::Pad] Pad004
  BaseFeature = -> Fillet
  Direction = (0,0,1)
  Length = 10
  Length2 = 10
  Offset = 7
  Profile = -> Sketch006
  ReferenceAxis = -> Sketch006 [N_Axis]
  Refine = true
  SideType = 0
  Suppressed = false
  Type = 3
  Type2 = 0
  UpToFace = -> Fillet [Face24]
  expr: Offset = Sketch007.Constraints.gap_box_painel
FEATURE [PartDesign::Mirrored] Mirrored002
  MirrorPlane = -> Sketch006 [V_Axis]
  Refine = true
  Suppressed = false
  TransformMode = 0
FEATURE [PartDesign::Mirrored] Mirrored003
  MirrorPlane = -> Sketch006 [H_Axis]
  Refine = true
  Suppressed = false
  TransformMode = 0
FEATURE [PartDesign::MultiTransform] MultiTransform001
  BaseFeature = -> Pad004
  Originals = -> [Pad004]
  Refine = true
  Suppressed = false
  TransformMode = 0
  Transformations = -> [Mirrored002,Mirrored003]
FEATURE [Part::Part2DObjectPython] ShapeString003  # Draft 2D object (typed FeaturePython)
  FontFile = <userpath>/Documents/FreeCAD/Fonts/JetBrainsMonoNerdFont-ExtraBold.ttf
  Fuse = false
  Justification = 4
  JustificationReference = 0
  KeepLeftMargin = false
  MakeFace = true
  ObliqueAngle = 0
  Placement = pos=(3.1e-15,-25,0) rot=(1,0,0;3.14159rad)
  ScaleToSize = true
  Size = 8
  String = Photogate V2
  Tracking = 0
FEATURE [PartDesign::Pocket] Pocket010
  BaseFeature = -> MultiTransform001
  Direction = (0,1e-16,1)
  Length = 0.4
  Length2 = 5
  Profile = -> ShapeString003
  ReferenceAxis = -> ShapeString003 [N_Axis]
  Refine = true
  SideType = 0
  Suppressed = false
  Type = 0
  Type2 = 0
FEATURE [PartDesign::Body] Body001  label="Painel"
  AllowCompound = false
  Group = -> [Sketch001,Pad,Pad001,Sketch002,Pocket,DatumPlane,Sketch003,Pad002,Pocket001,Pocket002,MultiTransform,Mirrored,Mirrored001,Sketch004,Pocket003,Pad003,Sketch005,Pocket004,Fillet,Sketch006,Pad004,MultiTransform001,Mirrored002,Mirrored003,ShapeString003,Pocket010]
  Origin = -> Origin001
  Tip = -> Pocket010
FEATURE [Sketcher::SketchObject] Sketch043
  ArcFitTolerance = 1e-06
  AttachmentSupport = -> [Pad018]
  ExternalGeometry = -> [Pad018]
  ExternalTypes = [0]
  FullyConstrained = true
  MakeInternals = false
  MapMode = 5
  Placement = pos=(0,26.5,-6.4e-15) rot=(1,0,0;1.5708rad)
  _ExternalGeoVersion = 0
  sketch-geometry (4):
    g0: LineSegment StartX=-39.5 StartY=48 StartZ=0 EndX=-39.5 EndY=4 EndZ=0
    g1: LineSegment StartX=-39.5 StartY=4 StartZ=0 EndX=39.5 EndY=4 EndZ=0
    g2: LineSegment StartX=39.5 StartY=4 StartZ=0 EndX=39.5 EndY=48 EndZ=0
    g3: LineSegment StartX=39.5 StartY=48 StartZ=0 EndX=-39.5 EndY=48 EndZ=0
  constraints (10):
    c: Coincident(g0,g1)
    c: Coincident(g1,g2)
    c: Coincident(g2,g3)
    c: Coincident(g3,g0)
    c: Vertical(g0)
    c: Vertical(g2)
    c: Horizontal(g1)
    c: Horizontal(g3)
    c: Coincident(g0,g-3)
    c: Coincident(g1,g-4)
FEATURE [PartDesign::Pad] Pad019
  BaseFeature = -> Pad018
  Direction = (0,-1,2e-16)
  Length = 1
  Length2 = 10
  Profile = -> Sketch043
  ReferenceAxis = -> Sketch043 [N_Axis]
  Refine = true
  SideType = 0
  Suppressed = false
  Type = 0
  Type2 = 0
FEATURE [PartDesign::Body] Body  label="Box"
  AllowCompound = false
  Group = -> [Sketch,Pad005,Pad006,Sketch007,Pocket005,Pad007,Chamfer,Sketch008,Pad008,Mirrored004,Sketch009,Pocket006,ShapeString,ShapeString001,ShapeString002,Pocket007,Pocket008,Pocket009,Sketch041,Pocket023,Sketch042,Pad018,Sketch043,Pad019]
  Origin = -> Origin
  Tip = -> Pad019
FEATURE [PartDesign::Mirrored] Mirrored007
  MirrorPlane = -> Sketch031 [V_Axis]
  Refine = true
  Suppressed = false
  TransformMode = 0
FEATURE [PartDesign::Mirrored] Mirrored008
  MirrorPlane = -> Sketch031 [H_Axis]
  Refine = true
  Suppressed = false
  TransformMode = 0
FEATURE [PartDesign::MultiTransform] MultiTransform002
  BaseFeature = -> Pad017
  Originals = -> [Pad017]
  Refine = true
  Suppressed = false
  TransformMode = 0
  Transformations = -> [Mirrored007,Mirrored008]
FEATURE [PartDesign::Body] Body005  label="stand"
  AllowCompound = false
  Group = -> [Sketch029,Pad015,Sketch030,Pad016,Sketch031,Pad017,MultiTransform002,Mirrored007,Mirrored008]
  Origin = -> Origin006
  Tip = -> MultiTransform002
FEATURE [PartDesign::SubShapeBinder] Binder
  BindCopyOnChange = 0
  BindMode = 0
  ClaimChildren = false
  Context = -> Body006 [Binder.]
  Fuse = false
  MakeFace = true
  OffsetFill = false
  OffsetIntersection = false
  OffsetJoinType = 0
  OffsetOpenResult = false
  PartialLoad = false
  Refine = true
  Relative = true
  Support = -> [Body004[Fillet004.Face12]]
  _Version = 2
FEATURE [Sketcher::SketchObject] Sketch044
  ArcFitTolerance = 1e-06
  AttachmentSupport = -> [Binder]
  ExternalGeometry = -> [Binder]
  ExternalTypes = [0]
  FullyConstrained = true
  MakeInternals = false
  MapMode = 5
  Placement = pos=(0,0,10) rot=(0,0,1;0rad)
  _ExternalGeoVersion = 0
  sketch-geometry (26):
    g0: ArcOfCircle CenterX=54.1066 CenterY=33.1066 CenterZ=0 NormalX=0 NormalY=0 NormalZ=1 AngleXU=0 Radius=0.4 StartAngle=1.5708 EndAngle=4.71239
    g1: ArcOfCircle CenterX=57.1066 CenterY=33.1066 CenterZ=0 NormalX=0 NormalY=0 NormalZ=1 AngleXU=0 Radius=0.4 StartAngle=4.71239 EndAngle=7.85398
    g2: LineSegment StartX=54.1066 StartY=33.5066 StartZ=0 EndX=57.1066 EndY=33.5066 EndZ=0
    g3: LineSegment StartX=54.1066 StartY=32.7066 StartZ=0 EndX=57.1066 EndY=32.7066 EndZ=0
    g4: LineSegment StartX=53.1066 StartY=32.1066 StartZ=0 EndX=58.1066 EndY=32.1066 EndZ=0
    g5: LineSegment StartX=58.1066 StartY=32.1066 StartZ=0 EndX=58.1066 EndY=34.1066 EndZ=0
    g6: LineSegment StartX=58.1066 StartY=34.1066 StartZ=0 EndX=53.1066 EndY=34.1066 EndZ=0
    g7: LineSegment StartX=53.1066 StartY=34.1066 StartZ=0 EndX=53.1066 EndY=32.1066 EndZ=0
    g8: GeomPoint [constr] X=55.6066 Y=33.1066 Z=0
    g9: Circle CenterX=55.6066 CenterY=33.1066 CenterZ=0 NormalX=0 NormalY=0 NormalZ=1 AngleXU=0 Radius=8.5
    g10: LineSegment StartX=57.7677 StartY=41.1721 StartZ=0 EndX=49.7023 EndY=39.0109 EndZ=0
    g11: LineSegment StartX=49.7023 StartY=39.0109 StartZ=0 EndX=47.5411 EndY=30.9455 EndZ=0
    g12: LineSegment StartX=47.5411 StartY=30.9455 StartZ=0 EndX=53.4455 EndY=25.0411 EndZ=0
    g13: LineSegment StartX=53.4455 StartY=25.0411 StartZ=0 EndX=61.5109 EndY=27.2023 EndZ=0
    g14: LineSegment StartX=61.5109 StartY=27.2023 StartZ=0 EndX=63.6721 EndY=35.2677 EndZ=0
    g15: LineSegment StartX=63.6721 StartY=35.2677 StartZ=0 EndX=57.7677 EndY=41.1721 EndZ=0
    g16: Circle [constr] CenterX=55.6066 CenterY=33.1066 CenterZ=0 NormalX=0 NormalY=0 NormalZ=1 AngleXU=0 Radius=8.35
    g17: LineSegment StartX=57.4183 StartY=39.8681 StartZ=0 EndX=50.6569 EndY=38.0563 EndZ=0
    g18: LineSegment StartX=50.6569 StartY=38.0563 StartZ=0 EndX=48.8451 EndY=31.2949 EndZ=0
    g19: LineSegment StartX=48.8451 StartY=31.2949 StartZ=0 EndX=53.7949 EndY=26.3451 EndZ=0
    g20: LineSegment StartX=53.7949 StartY=26.3451 StartZ=0 EndX=60.5563 EndY=28.1569 EndZ=0
    g21: LineSegment StartX=60.5563 StartY=28.1569 StartZ=0 EndX=62.3681 EndY=34.9183 EndZ=0
    g22: LineSegment StartX=62.3681 StartY=34.9183 StartZ=0 EndX=57.4183 EndY=39.8681 EndZ=0
    g23: Circle [constr] CenterX=55.6066 CenterY=33.1066 CenterZ=0 NormalX=0 NormalY=0 NormalZ=1 AngleXU=0 Radius=7
    g24: LineSegment [constr] StartX=57.8066 StartY=41.317 StartZ=0 EndX=57.7677 EndY=41.1721 EndZ=0
    g25: LineSegment [constr] StartX=57.7677 StartY=41.1721 StartZ=0 EndX=57.4183 EndY=39.8681 EndZ=0
  constraints (60):
    c: Tangent(g0,g2) = 1.5708
    c: Tangent(g0,g3) = -1.5708
    c: Tangent(g1,g2) = 1.5708
    c: Tangent(g1,g3) = -1.5708
    c: Equal(g0,g1)
    c: Horizontal(g2)
    c: Radius(g0) = 0.4
    c: DistanceX(g2,g2) = 3
    c: Coincident(g4,g5)
    c: Coincident(g5,g6)
    c: Coincident(g6,g7)
    c: Coincident(g7,g4)
    c: Horizontal(g4)
    c: Horizontal(g6)
    c: Vertical(g5)
    c: Vertical(g7)
    c: Symmetric(g6,g4,g8)
    c: DistanceX(g6,g6) = 5
    c: DistanceY(g5,g5) = 2
    c: PointOnObject(g-4,g9)
    c: PointOnObject(g-5,g9)
    c: PointOnObject(g-3,g9)
    c: Coincident(g8,g9)
    c: Symmetric(g0,g1,g8)
    c: Coincident(g10,g11)
    c: Coincident(g11,g12)
    c: Coincident(g12,g13)
    c: Coincident(g13,g14)
    c: Coincident(g14,g15)
    c: Coincident(g15,g10)
    c: Equal(g10, g11-g15) x5
    c: PointOnObject(g10,g16)
    c: PointOnObject(g11,g16)
    c: PointOnObject(g12,g16)
    c: PointOnObject(g13,g16)
    c: PointOnObject(g14,g16)
    c: PointOnObject(g15,g16)
    c: Coincident(g16,g8)
    c: Coincident(g17,g18)
    c: Coincident(g18,g19)
    c: Coincident(g19,g20)
    c: Coincident(g20,g21)
    c: Coincident(g21,g22)
    c: Coincident(g22,g17)
    c: Equal(g17, g18-g22) x5
    c: PointOnObject(g17,g23)
    c: PointOnObject(g18,g23)
    c: PointOnObject(g19,g23)
    c: PointOnObject(g20,g23)
    c: PointOnObject(g21,g23)
    c: PointOnObject(g22,g23)
    c: Coincident(g23,g8)
    c: Diameter(g16) = 16.7
    c: Diameter(g23) = 14
    c: Coincident(g24,g-3)
    c: Coincident(g24,g10)
    c: Coincident(g25,g10)
    c: Coincident(g25,g17)
    c: Parallel(g25,g24)
    c: Perpendicular(g9,g24)
FEATURE [PartDesign::Pad] Pad020
  Direction = (0,0,1)
  Length = 0.5
  Length2 = 10
  Profile = -> Sketch044 [Edge9,Edge2,Edge3,Edge4,Edge1]
  ReferenceAxis = -> Sketch044 [N_Axis]
  Refine = true
  SideType = 0
  Suppressed = false
  Type = 0
  Type2 = 0
FEATURE [Sketcher::SketchObject] Sketch046
  ArcFitTolerance = 1e-06
  AttachmentSupport = -> [XY_Plane008]
  ExternalTypes = [0]
  FullyConstrained = true
  MakeInternals = false
  MapMode = 5
  _ExternalGeoVersion = 0
  expr: Constraints[11] = Sketch045.Constraints.reforce_arm_width - 0.2 mm
  sketch-geometry (5):
    g0: LineSegment StartX=-2.89999 StartY=-2.89999 StartZ=0 EndX=2.89999 EndY=-2.89999 EndZ=0
    g1: LineSegment StartX=2.89999 StartY=-2.89999 StartZ=0 EndX=2.89999 EndY=2.89999 EndZ=0
    g2: LineSegment StartX=2.89999 StartY=2.89999 StartZ=0 EndX=-2.89999 EndY=2.89999 EndZ=0
    g3: LineSegment StartX=-2.89999 StartY=2.89999 StartZ=0 EndX=-2.89999 EndY=-2.89999 EndZ=0
    g4: GeomPoint [constr] X=0 Y=0 Z=0
  constraints (12):
    c: Coincident(g0,g1)
    c: Coincident(g1,g2)
    c: Coincident(g2,g3)
    c: Coincident(g3,g0)
    c: Horizontal(g0)
    c: Horizontal(g2)
    c: Vertical(g1)
    c: Vertical(g3)
    c: Symmetric(g2,g0,g4)
    c: Coincident(g4,g-1)
    c: Equal(g0,g1)
    c: DistanceY(g1,g1) = 5.79999
FEATURE [PartDesign::Pad] Pad022
  Direction = (0,0,1)
  Length = 137.1
  Length2 = 10
  Profile = -> Sketch046
  ReferenceAxis = -> Sketch046 [N_Axis]
  Refine = true
  SideType = 0
  Suppressed = false
  Type = 0
  Type2 = 0
  expr: Length = Sketch001.Constraints.display_inner_length + 2 * 6 mm - 0.2 mm
FEATURE [PartDesign::Body] Body007  label="Reforce2Arm"
  AllowCompound = false
  Group = -> [Sketch046,Pad022]
  Origin = -> Origin008
  Tip = -> Pad022
FEATURE [Sketcher::SketchObject] Sketch052
  ArcFitTolerance = 1e-06
  AttachmentSupport = -> [XY_Plane009]
  ExternalTypes = [0]
  FullyConstrained = true
  MakeInternals = false
  MapMode = 5
  _ExternalGeoVersion = 0
  sketch-geometry (5):
    g0: ArcOfCircle CenterX=0 CenterY=0 CenterZ=0 NormalX=0 NormalY=0 NormalZ=1 AngleXU=0 Radius=3 StartAngle=2.49809 EndAngle=6.92669
    g1: LineSegment StartX=-2.4 StartY=1.8 StartZ=0 EndX=2.4 EndY=1.8 EndZ=0
    g2: GeomPoint X=0 Y=-3 Z=0
    g3: Circle CenterX=0 CenterY=0 CenterZ=0 NormalX=0 NormalY=0 NormalZ=1 AngleXU=0 Radius=15
    g4: Circle CenterX=0 CenterY=0 CenterZ=0 NormalX=0 NormalY=0 NormalZ=1 AngleXU=0 Radius=11.5
  constraints (12):
    c: Diameter(g0) = 6
    c: Coincident(g0,g-1)
    c: Horizontal(g1)
    c: PointOnObject(g2,g0)
    c: PointOnObject(g2,g-2)
    c: DistanceY(g2,g1) = 4.8
    c: Coincident(g0,g1)
    c: Coincident(g0,g1)
    c: Diameter(g3) = 30
    c: Coincident(g3,g0)
    c: Coincident(g4,g0)
    c: Diameter(g4) = 23
FEATURE [PartDesign::Pad] Pad025
  BaseFeature = -> Pad020
  Direction = (0,0,1)
  Length = 1
  Length2 = 10
  Profile = -> Sketch044 [Edge6,Edge3,Edge4,Edge7,Edge2,Edge5,Edge8,Edge1]
  ReferenceAxis = -> Sketch044 [N_Axis]
  Refine = true
  Reversed = true
  SideType = 0
  Suppressed = false
  Type = 0
  Type2 = 0
FEATURE [PartDesign::SubShapeBinder] Binder001
  BindCopyOnChange = 0
  BindMode = 0
  ClaimChildren = false
  Context = -> Body006 [Binder001.]
  Fuse = false
  MakeFace = true
  OffsetFill = false
  OffsetIntersection = false
  OffsetJoinType = 0
  OffsetOpenResult = false
  PartialLoad = false
  Refine = true
  Relative = true
  Support = -> [Pad025[Edge18,Edge16,Edge14,Edge19]]
  _Version = 2
FEATURE [PartDesign::Pad] Pad026
  BaseFeature = -> Pad025
  Direction = (0,0,1)
  Length = 0.4
  Length2 = 10
  Profile = -> Pad025 [Edge18,Edge16,Edge14,Edge19]
  Refine = true
  Reversed = true
  SideType = 0
  Suppressed = false
  Type = 0
  Type2 = 0
FEATURE [PartDesign::Pad] Pad027
  BaseFeature = -> Pad026
  Direction = (0,0,1)
  Length = 3.5
  Length2 = 10
  Profile = -> Sketch044 [Edge12,Edge18,Edge11,Edge17,Edge10,Edge16,Edge15,Edge21,Edge14,Edge20,Edge13,Edge19]
  ReferenceAxis = -> Sketch044 [N_Axis]
  Refine = true
  Reversed = true
  SideType = 0
  Suppressed = false
  Type = 0
  Type2 = 0
FEATURE [PartDesign::Chamfer] Chamfer001
  Angle = 45
  Base = -> Pad027 [Face13]
  BaseFeature = -> Pad027
  ChamferType = 0
  FlipDirection = false
  Refine = true
  Size = 0.4
  Size2 = 1
  SupportTransform = false
  Suppressed = false
  UseAllEdges = false
FEATURE [PartDesign::Body] Body006  label="IrCap"
  AllowCompound = false
  Group = -> [Binder,Sketch044,Pad020,Pad025,Binder001,Pad026,Pad027,Chamfer001]
  Origin = -> Origin007
  Tip = -> Chamfer001
FEATURE [PartDesign::Pad] Pad028
  Direction = (0,0,1)
  Length = 1
  Length2 = 10
  Profile = -> Sketch052 [Edge3]
  ReferenceAxis = -> Sketch052 [N_Axis]
  Refine = true
  Reversed = true
  SideType = 0
  Suppressed = false
  Type = 0
  Type2 = 0
FEATURE [PartDesign::Pad] Pad029
  BaseFeature = -> Pad028
  Direction = (0,0,1)
  Length = 7
  Length2 = 10
  Profile = -> Sketch052 [Edge3,Edge1,Edge2]
  ReferenceAxis = -> Sketch052 [N_Axis]
  Refine = true
  SideType = 0
  Suppressed = false
  Type = 0
  Type2 = 0
FEATURE [PartDesign::Pad] Pad030
  BaseFeature = -> Pad029
  Direction = (0,0,1)
  Length = 14
  Length2 = 10
  Profile = -> Sketch052 [Edge4,Edge3]
  ReferenceAxis = -> Sketch052 [N_Axis]
  Refine = true
  SideType = 0
  Suppressed = false
  Type = 0
  Type2 = 0
FEATURE [Sketcher::SketchObject] Sketch053
  ArcFitTolerance = 1e-06
  AttachmentSupport = -> [Pad030]
  ExternalGeometry = -> [Sketch052]
  ExternalTypes = [0]
  FullyConstrained = true
  MakeInternals = false
  MapMode = 5
  Placement = pos=(0,0,-1) rot=(1,0,0;3.14159rad)
  _ExternalGeoVersion = 0
  sketch-geometry (2):
    g0: ArcOfCircle CenterX=0 CenterY=15 CenterZ=0 NormalX=0 NormalY=0 NormalZ=1 AngleXU=0 Radius=1.5 StartAngle=3.19161 EndAngle=6.23316
    g1: ArcOfCircle CenterX=0 CenterY=0 CenterZ=0 NormalX=0 NormalY=0 NormalZ=1 AngleXU=0 Radius=15 StartAngle=1.47075 EndAngle=1.67084
  constraints (7):
    c: PointOnObject(g0,g-2)
    c: PointOnObject(g0,g-3)
    c: PointOnObject(g0,g-3)
    c: Coincident(g1,g-1)
    c: Coincident(g1,g0)
    c: Coincident(g1,g0)
    c: Radius(g0) = 1.5
FEATURE [PartDesign::Pocket] Pocket026
  BaseFeature = -> Pad030
  Direction = (0,0,1)
  Length = 5
  Length2 = 5
  Profile = -> Sketch053
  ReferenceAxis = -> Sketch053 [N_Axis]
  Refine = true
  SideType = 0
  Suppressed = false
  Type = 1
  Type2 = 0
FEATURE [PartDesign::Fillet] Fillet005
  Base = -> Pocket026 [Edge4,Edge2,Edge6,Edge1]
  BaseFeature = -> Pocket026
  Radius = 1
  Refine = true
  SupportTransform = false
  Suppressed = false
  UseAllEdges = false
FEATURE [PartDesign::PolarPattern] PolarPattern001
  Angle = 360
  Axis = -> Sketch053 [N_Axis]
  BaseFeature = -> Fillet005
  Mode = 0
  Occurrences = 10
  Offset = 120
  Originals = -> [Pocket026,Fillet005]
  Refine = true
  SpacingPattern = [0]
  Spacings = [-1,-1,-1,-1,-1,-1,-1,-1,-1]
  Suppressed = false
  TransformMode = 0
FEATURE [Sketcher::SketchObject] Sketch054
  ArcFitTolerance = 1e-06
  AttachmentSupport = -> [PolarPattern001]
  ExternalGeometry = -> [Sketch052]
  ExternalTypes = [0]
  FullyConstrained = true
  MakeInternals = false
  MapMode = 5
  Placement = pos=(0,0,-1) rot=(1,0,0;3.14159rad)
  _ExternalGeoVersion = 0
  sketch-geometry (25):
    g0: ArcOfCircle CenterX=0 CenterY=0 CenterZ=0 NormalX=0 NormalY=0 NormalZ=1 AngleXU=0 Radius=11 StartAngle=1.74533 EndAngle=3.14159
    g1: ArcOfCircle CenterX=0 CenterY=0 CenterZ=0 NormalX=0 NormalY=0 NormalZ=1 AngleXU=0 Radius=8 StartAngle=1.74533 EndAngle=3.14159
    g2: LineSegment StartX=-11 StartY=-2.7e-15 StartZ=0 EndX=-13 EndY=-3.2e-15 EndZ=0
    g3: LineSegment StartX=-8 StartY=0 StartZ=0 EndX=-6 EndY=-1.5e-15 EndZ=0
    g4: LineSegment StartX=-6 StartY=-1.5e-15 StartZ=0 EndX=-9.5 EndY=-5.48483 EndZ=0
    g5: LineSegment StartX=-13 StartY=-3.2e-15 StartZ=0 EndX=-9.5 EndY=-5.48483 EndZ=0
    g6: LineSegment StartX=-1.38919 StartY=7.87846 StartZ=0 EndX=-1.91013 EndY=10.8329 EndZ=0
    g7: LineSegment [constr] StartX=-8 StartY=0 StartZ=0 EndX=-11 EndY=-2.7e-15 EndZ=0
    g8: LineSegment [constr] StartX=-10.799 StartY=-6.23483 StartZ=0 EndX=-8.20096 EndY=-4.73483 EndZ=0
    g9: ArcOfCircle CenterX=0 CenterY=0 CenterZ=0 NormalX=0 NormalY=0 NormalZ=1 AngleXU=0 Radius=11 StartAngle=0 EndAngle=1.39626
    g10: ArcOfCircle CenterX=0 CenterY=0 CenterZ=0 NormalX=0 NormalY=0 NormalZ=1 AngleXU=0 Radius=8 StartAngle=0 EndAngle=1.39626
    g11: LineSegment StartX=11 StartY=0 StartZ=0 EndX=13 EndY=-3.2e-15 EndZ=0
    g12: LineSegment StartX=8 StartY=0 StartZ=0 EndX=6 EndY=-1.5e-15 EndZ=0
    g13: LineSegment StartX=6 StartY=-1.5e-15 StartZ=0 EndX=9.5 EndY=-5.48483 EndZ=0
    g14: LineSegment StartX=13 StartY=-3.2e-15 StartZ=0 EndX=9.5 EndY=-5.48483 EndZ=0
    g15: LineSegment StartX=1.38919 StartY=7.87846 StartZ=0 EndX=1.91013 EndY=10.8329 EndZ=0
    g16: LineSegment [constr] StartX=8 StartY=0 StartZ=0 EndX=11 EndY=0 EndZ=0
    g17: LineSegment [constr] StartX=10.799 StartY=-6.23483 StartZ=0 EndX=8.20096 EndY=-4.73483 EndZ=0
    g18: LineSegment StartX=4 StartY=-2 StartZ=0 EndX=-4 EndY=-2 EndZ=0
    g19: LineSegment StartX=-4 StartY=-2 StartZ=0 EndX=0 EndY=-6.47214 EndZ=0
    g20: LineSegment StartX=0 StartY=-6.47214 StartZ=0 EndX=4 EndY=-2 EndZ=0
    g21: LineSegment StartX=-4.5 StartY=-8.47214 StartZ=0 EndX=-4.5 EndY=-10.4721 EndZ=0
    g22: LineSegment StartX=-4.5 StartY=-10.4721 StartZ=0 EndX=4.5 EndY=-10.4721 EndZ=0
    g23: LineSegment StartX=4.5 StartY=-10.4721 StartZ=0 EndX=4.5 EndY=-8.47214 EndZ=0
    g24: LineSegment StartX=4.5 StartY=-8.47214 StartZ=0 EndX=-4.5 EndY=-8.47214 EndZ=0
  constraints (71):
    c: Coincident(g0,g-1)
    c: Coincident(g1,g0)
    c: Coincident(g2,g0)
    c: Coincident(g3,g1)
    c: Coincident(g4,g3)
    c: Coincident(g5,g2)
    c: Coincident(g5,g4)
    c: Perpendicular(g-3,g2)
    c: Perpendicular(g-3,g3)
    c: Equal(g4,g5)
    c: Coincident(g6,g1)
    c: Coincident(g6,g0)
    c: Perpendicular(g0,g6)
    c: Equal(g2,g3)
    c: Coincident(g7,g1)
    c: Coincident(g7,g0)
    c: Perpendicular(g-3,g7)
    c: Equal(g8,g6)
    c: Perpendicular(g-3,g8)
    c: Symmetric(g8,g8,g4)
    c: Angle(g6,g8) = 1.91986
    c: Angle(g7,g8) = 0.523599
    c: Angle(g-2,g6) = 0.174533
    c: Coincident(g10,g9)
    c: Coincident(g11,g9)
    c: Coincident(g12,g10)
    c: Coincident(g13,g12)
    c: Coincident(g14,g11)
    c: Coincident(g14,g13)
    c: Equal(g13,g14)
    c: Coincident(g15,g10)
    c: Coincident(g15,g9)
    c: Perpendicular(g9,g15)
    c: Equal(g11,g12)
    c: Coincident(g16,g10)
    c: Coincident(g16,g9)
    c: Equal(g17,g15)
    c: Symmetric(g17,g17,g13)
    c: Perpendicular(g-3,g11)
    c: Perpendicular(g-3,g12)
    c: Perpendicular(g-3,g17)
    c: Coincident(g9,g0)
    c: Perpendicular(g-3,g16)
    c: Horizontal(g0,g9)
    c: Horizontal(g18)
    c: Coincident(g18,g19)
    c: Coincident(g19,g20)
    c: Coincident(g20,g18)
    c: Equal(g20,g19)
    c: Coincident(g21,g22)
    c: Coincident(g22,g23)
    c: Coincident(g23,g24)
    c: Coincident(g24,g21)
    c: Vertical(g21)
    c: Vertical(g23)
    c: Horizontal(g24)
    c: Symmetric(g21,g22,g-2)
    c: DistanceY(g23,g19) = 2
    c: DistanceX(g21,g18) = 0.5
    c: Equal(g2,g11)
    c: Distance(g6,g6) = 3
    c: Horizontal(g1,g10)
    c: Horizontal(g13,g4)
    c: Symmetric(g1,g10,g-2)
    c: DistanceY(g23,g23) = 2
    c: DistanceX(g11,g11) = 2
    c: DistanceX(g18,g18) = 8
    c: Distance(g20,g20) = 6
    c: Radius(g1) = 8
    c: PointOnObject(g19,g-2)
    c: DistanceY(g18,g-1) = 2
FEATURE [PartDesign::Pocket] Pocket027
  BaseFeature = -> PolarPattern001
  Direction = (0,0,1)
  Length = 0.4
  Length2 = 5
  Profile = -> Sketch054
  ReferenceAxis = -> Sketch054 [N_Axis]
  Refine = true
  SideType = 0
  Suppressed = false
  Type = 0
  Type2 = 0
FEATURE [PartDesign::Body] Body008  label="Knob"
  AllowCompound = false
  Group = -> [Sketch052,Sketch053,Sketch054,Pad028,Pad029,Pad030,Pocket026,Fillet005,PolarPattern001,Pocket027]
  Origin = -> Origin009
  Tip = -> Pocket027
FEATURE [Sketcher::SketchObject] Sketch055
  ArcFitTolerance = 1e-06
  AttachmentSupport = -> [XY_Plane011]
  ExternalTypes = [0]
  FullyConstrained = true
  MakeInternals = false
  MapMode = 5
  _ExternalGeoVersion = 0
  sketch-geometry (9):
    g0: ArcOfCircle CenterX=0 CenterY=0 CenterZ=0 NormalX=0 NormalY=0 NormalZ=1 AngleXU=0 Radius=3 StartAngle=0.848062 EndAngle=5.43512
    g1: ArcOfCircle CenterX=0 CenterY=0 CenterZ=0 NormalX=0 NormalY=0 NormalZ=1 AngleXU=0 Radius=5 StartAngle=1.5708 EndAngle=4.71239
    g2: LineSegment StartX=3e-16 StartY=5 StartZ=0 EndX=8 EndY=5 EndZ=0
    g3: LineSegment StartX=8 StartY=5 StartZ=0 EndX=8 EndY=2.25 EndZ=0
    g4: LineSegment StartX=8 StartY=2.25 StartZ=0 EndX=1.98431 EndY=2.25 EndZ=0
    g5: LineSegment StartX=-6.17132e-06 StartY=-5 StartZ=0 EndX=8 EndY=-5 EndZ=0
    g6: LineSegment StartX=8 StartY=-5 StartZ=0 EndX=8 EndY=-2.25 EndZ=0
    g7: LineSegment StartX=8 StartY=-2.25 StartZ=0 EndX=1.98431 EndY=-2.25 EndZ=0
    g8: Circle [constr] CenterX=0 CenterY=0 CenterZ=0 NormalX=0 NormalY=0 NormalZ=1 AngleXU=0 Radius=3
  constraints (25):
    c: Coincident(g0,g-1)
    c: Coincident(g1,g0)
    c: Coincident(g2,g3)
    c: Coincident(g3,g4)
    c: Vertical(g3)
    c: Horizontal(g2)
    c: Horizontal(g4)
    c: Coincident(g5,g6)
    c: Coincident(g6,g7)
    c: Vertical(g6)
    c: Horizontal(g5)
    c: Horizontal(g7)
    c: Diameter(g0) = 6
    c: Vertical(g6,g3)
    c: Vertical(g4,g7)
    c: Distance(g3,g6) = 4.5
    c: DistanceX(g2,g2) = 8
    c: Coincident(g4,g0)
    c: Coincident(g0,g7)
    c: Coincident(g1,g5)
    c: Equal(g6,g3)
    c: Tangent(g2,g1) = 1.5708
    c: Diameter(g1) = 10
    c: Coincident(g8,g0)
    c: PointOnObject(g0,g8)
FEATURE [PartDesign::Pad] Pad031
  Direction = (0,0,1)
  Length = 10
  Length2 = 10
  Profile = -> Sketch055
  ReferenceAxis = -> Sketch055 [N_Axis]
  Refine = true
  SideType = 2
  Suppressed = false
  Type = 0
  Type2 = 0
FEATURE [Sketcher::SketchObject] Sketch056
  ArcFitTolerance = 1e-06
  AttachmentSupport = -> [XZ_Plane011]
  ExternalGeometry = -> [Pad031]
  ExternalTypes = [0]
  FullyConstrained = true
  MakeInternals = false
  MapMode = 5
  Placement = pos=(0,0,0) rot=(1,0,0;1.5708rad)
  _ExternalGeoVersion = 0
  sketch-geometry (2):
    g0: Circle CenterX=4.75 CenterY=0 CenterZ=0 NormalX=0 NormalY=0 NormalZ=1 AngleXU=0 Radius=1.75
    g1: LineSegment [constr] StartX=3 StartY=5 StartZ=0 EndX=3 EndY=-5 EndZ=0
  constraints (6):
    c: Diameter(g0) = 3.5
    c: Coincident(g1,g-3)
    c: Vertical(g1)
    c: Tangent(g0,g1)
    c: Horizontal(g-4,g1)
    c: PointOnObject(g0,g-1)
FEATURE [PartDesign::Pocket] Pocket028
  BaseFeature = -> Pad031
  Direction = (0,1,-2e-16)
  Length = 5
  Length2 = 5
  Profile = -> Sketch056
  ReferenceAxis = -> Sketch056 [N_Axis]
  Refine = true
  SideType = 2
  Suppressed = false
  Type = 1
  Type2 = 0
FEATURE [PartDesign::Body] Body009  label="SensorHolder"
  AllowCompound = false
  Group = -> [Sketch055,Pad031,Sketch056,Pocket028]
  Origin = -> Origin011
  Tip = -> Pocket028
FEATURE [PartDesign::Pocket] Pocket012
  BaseFeature = -> Fillet002
  Direction = (0,0,-1)
  Length = 3
  Length2 = 5
  Profile = -> Sketch015 [Edge2]
  ReferenceAxis = -> Sketch015 [N_Axis]
  Refine = true
  SideType = 0
  Suppressed = false
  Type = 0
  Type2 = 0
FEATURE [PartDesign::Pad] Pad032
  BaseFeature = -> Pocket012
  Direction = (0,0,1)
  Length = 4
  Length2 = 10
  Profile = -> Sketch015 [Edge1,Edge6,Edge5,Edge7,Edge8,Edge3,Edge4]
  ReferenceAxis = -> Sketch015 [N_Axis]
  Refine = true
  SideType = 0
  Suppressed = false
  Type = 0
  Type2 = 0
FEATURE [Sketcher::SketchObject] Sketch050  label="LorxiSymbol"
  ArcFitTolerance = 1e-06
  AttachmentOffset = pos=(11,-9.424,0) rot=(0,0,1;0rad)
  AttachmentSupport = -> [Pad032]
  ExternalTypes = [0]
  FullyConstrained = false
  MakeInternals = false
  MapMode = 5
  Placement = pos=(11,9.424,-8.2) rot=(1,0,0;3.14159rad)
  _ExternalGeoVersion = 0
  sketch-geometry (292):
    g0: BSplineCurve PolesCount=4 KnotsCount=2 Degree=3 IsPeriodic=0
    g1: BSplineCurve PolesCount=2 KnotsCount=2 Degree=1 IsPeriodic=0
    g2: BSplineCurve PolesCount=2 KnotsCount=2 Degree=1 IsPeriodic=0
    g3: BSplineCurve PolesCount=2 KnotsCount=2 Degree=1 IsPeriodic=0
    g4: BSplineCurve PolesCount=4 KnotsCount=2 Degree=3 IsPeriodic=0
    g5: BSplineCurve PolesCount=4 KnotsCount=2 Degree=3 IsPeriodic=0
    g6: BSplineCurve PolesCount=2 KnotsCount=2 Degree=1 IsPeriodic=0
    g7: BSplineCurve PolesCount=2 KnotsCount=2 Degree=1 IsPeriodic=0
    g8: BSplineCurve PolesCount=2 KnotsCount=2 Degree=1 IsPeriodic=0
    g9: BSplineCurve PolesCount=4 KnotsCount=2 Degree=3 IsPeriodic=0
    g10: BSplineCurve PolesCount=2 KnotsCount=2 Degree=1 IsPeriodic=0
    g11: BSplineCurve PolesCount=2 KnotsCount=2 Degree=1 IsPeriodic=0
    g12: BSplineCurve PolesCount=4 KnotsCount=2 Degree=3 IsPeriodic=0
    g13: BSplineCurve PolesCount=4 KnotsCount=2 Degree=3 IsPeriodic=0
    g14: BSplineCurve PolesCount=2 KnotsCount=2 Degree=1 IsPeriodic=0
    g15: BSplineCurve PolesCount=2 KnotsCount=2 Degree=1 IsPeriodic=0
    g16: BSplineCurve PolesCount=2 KnotsCount=2 Degree=1 IsPeriodic=0
    g17: BSplineCurve PolesCount=4 KnotsCount=2 Degree=3 IsPeriodic=0
    g18: BSplineCurve PolesCount=2 KnotsCount=2 Degree=1 IsPeriodic=0
    g19: BSplineCurve PolesCount=4 KnotsCount=2 Degree=3 IsPeriodic=0
    g20: BSplineCurve PolesCount=4 KnotsCount=2 Degree=3 IsPeriodic=0
    g21: BSplineCurve PolesCount=2 KnotsCount=2 Degree=1 IsPeriodic=0
    g22: BSplineCurve PolesCount=4 KnotsCount=2 Degree=3 IsPeriodic=0
    g23: BSplineCurve PolesCount=4 KnotsCount=2 Degree=3 IsPeriodic=0
    g24: BSplineCurve PolesCount=2 KnotsCount=2 Degree=1 IsPeriodic=0
    g25: BSplineCurve PolesCount=4 KnotsCount=2 Degree=3 IsPeriodic=0
    g26: BSplineCurve PolesCount=4 KnotsCount=2 Degree=3 IsPeriodic=0
    g27: BSplineCurve PolesCount=2 KnotsCount=2 Degree=1 IsPeriodic=0
    g28: BSplineCurve PolesCount=4 KnotsCount=2 Degree=3 IsPeriodic=0
    g29: BSplineCurve PolesCount=4 KnotsCount=2 Degree=3 IsPeriodic=0
    g30: BSplineCurve PolesCount=2 KnotsCount=2 Degree=1 IsPeriodic=0
    g31: BSplineCurve PolesCount=4 KnotsCount=2 Degree=3 IsPeriodic=0
    g32: BSplineCurve PolesCount=4 KnotsCount=2 Degree=3 IsPeriodic=0
    g33: BSplineCurve PolesCount=2 KnotsCount=2 Degree=1 IsPeriodic=0
    g34: BSplineCurve PolesCount=4 KnotsCount=2 Degree=3 IsPeriodic=0
    g35: BSplineCurve PolesCount=4 KnotsCount=2 Degree=3 IsPeriodic=0
    g36: BSplineCurve PolesCount=2 KnotsCount=2 Degree=1 IsPeriodic=0
    g37: BSplineCurve PolesCount=4 KnotsCount=2 Degree=3 IsPeriodic=0
    g38: BSplineCurve PolesCount=4 KnotsCount=2 Degree=3 IsPeriodic=0
    g39: BSplineCurve PolesCount=4 KnotsCount=2 Degree=3 IsPeriodic=0
    g40: BSplineCurve PolesCount=4 KnotsCount=2 Degree=3 IsPeriodic=0
    g41: BSplineCurve PolesCount=2 KnotsCount=2 Degree=1 IsPeriodic=0
    g42: BSplineCurve PolesCount=4 KnotsCount=2 Degree=3 IsPeriodic=0
    g43: BSplineCurve PolesCount=4 KnotsCount=2 Degree=3 IsPeriodic=0
    g44: BSplineCurve PolesCount=4 KnotsCount=2 Degree=3 IsPeriodic=0
    g45: BSplineCurve PolesCount=4 KnotsCount=2 Degree=3 IsPeriodic=0
    g46: BSplineCurve PolesCount=2 KnotsCount=2 Degree=1 IsPeriodic=0
    g47: BSplineCurve PolesCount=4 KnotsCount=2 Degree=3 IsPeriodic=0
    g48: BSplineCurve PolesCount=4 KnotsCount=2 Degree=3 IsPeriodic=0
    g49: BSplineCurve PolesCount=4 KnotsCount=2 Degree=3 IsPeriodic=0
    g50: BSplineCurve PolesCount=2 KnotsCount=2 Degree=1 IsPeriodic=0
    g51: BSplineCurve PolesCount=2 KnotsCount=2 Degree=1 IsPeriodic=0
    g52: BSplineCurve PolesCount=4 KnotsCount=2 Degree=3 IsPeriodic=0
    g53: BSplineCurve PolesCount=2 KnotsCount=2 Degree=1 IsPeriodic=0
    g54: BSplineCurve PolesCount=2 KnotsCount=2 Degree=1 IsPeriodic=0
    g55: BSplineCurve PolesCount=2 KnotsCount=2 Degree=1 IsPeriodic=0
    g56: BSplineCurve PolesCount=4 KnotsCount=2 Degree=3 IsPeriodic=0
    g57: BSplineCurve PolesCount=2 KnotsCount=2 Degree=1 IsPeriodic=0
    g58: BSplineCurve PolesCount=2 KnotsCount=2 Degree=1 IsPeriodic=0
    g59: BSplineCurve PolesCount=4 KnotsCount=2 Degree=3 IsPeriodic=0
    g60: BSplineCurve PolesCount=4 KnotsCount=2 Degree=3 IsPeriodic=0
    g61: BSplineCurve PolesCount=4 KnotsCount=2 Degree=3 IsPeriodic=0
    g62: BSplineCurve PolesCount=4 KnotsCount=2 Degree=3 IsPeriodic=0
    g63: BSplineCurve PolesCount=4 KnotsCount=2 Degree=3 IsPeriodic=0
    g64: BSplineCurve PolesCount=4 KnotsCount=2 Degree=3 IsPeriodic=0
    g65: BSplineCurve PolesCount=2 KnotsCount=2 Degree=1 IsPeriodic=0
    g66: BSplineCurve PolesCount=4 KnotsCount=2 Degree=3 IsPeriodic=0
    g67: BSplineCurve PolesCount=4 KnotsCount=2 Degree=3 IsPeriodic=0
    g68: BSplineCurve PolesCount=2 KnotsCount=2 Degree=1 IsPeriodic=0
    g69: BSplineCurve PolesCount=4 KnotsCount=2 Degree=3 IsPeriodic=0
    g70: BSplineCurve PolesCount=4 KnotsCount=2 Degree=3 IsPeriodic=0
    g71: BSplineCurve PolesCount=4 KnotsCount=2 Degree=3 IsPeriodic=0
    g72: BSplineCurve PolesCount=4 KnotsCount=2 Degree=3 IsPeriodic=0
    g73: BSplineCurve PolesCount=4 KnotsCount=2 Degree=3 IsPeriodic=0
    g74: BSplineCurve PolesCount=2 KnotsCount=2 Degree=1 IsPeriodic=0
    g75: BSplineCurve PolesCount=2 KnotsCount=2 Degree=1 IsPeriodic=0
    g76: BSplineCurve PolesCount=4 KnotsCount=2 Degree=3 IsPeriodic=0
    g77: BSplineCurve PolesCount=4 KnotsCount=2 Degree=3 IsPeriodic=0
    g78: BSplineCurve PolesCount=4 KnotsCount=2 Degree=3 IsPeriodic=0
    g79: BSplineCurve PolesCount=4 KnotsCount=2 Degree=3 IsPeriodic=0
    g80: BSplineCurve PolesCount=4 KnotsCount=2 Degree=3 IsPeriodic=0
    g81: BSplineCurve PolesCount=2 KnotsCount=2 Degree=1 IsPeriodic=0
    g82: BSplineCurve PolesCount=4 KnotsCount=2 Degree=3 IsPeriodic=0
    g83: BSplineCurve PolesCount=4 KnotsCount=2 Degree=3 IsPeriodic=0
    g84: BSplineCurve PolesCount=2 KnotsCount=2 Degree=1 IsPeriodic=0
    g85: BSplineCurve PolesCount=4 KnotsCount=2 Degree=3 IsPeriodic=0
    g86: BSplineCurve PolesCount=4 KnotsCount=2 Degree=3 IsPeriodic=0
    g87: BSplineCurve PolesCount=4 KnotsCount=2 Degree=3 IsPeriodic=0
    g88: BSplineCurve PolesCount=4 KnotsCount=2 Degree=3 IsPeriodic=0
    g89: BSplineCurve PolesCount=4 KnotsCount=2 Degree=3 IsPeriodic=0
    g90: BSplineCurve PolesCount=4 KnotsCount=2 Degree=3 IsPeriodic=0
    g91: BSplineCurve PolesCount=2 KnotsCount=2 Degree=1 IsPeriodic=0
    g92: BSplineCurve PolesCount=2 KnotsCount=2 Degree=1 IsPeriodic=0
    g93: BSplineCurve PolesCount=4 KnotsCount=2 Degree=3 IsPeriodic=0
    g94: BSplineCurve PolesCount=2 KnotsCount=2 Degree=1 IsPeriodic=0
    g95: BSplineCurve PolesCount=2 KnotsCount=2 Degree=1 IsPeriodic=0
    g96: BSplineCurve PolesCount=2 KnotsCount=2 Degree=1 IsPeriodic=0
    g97: BSplineCurve PolesCount=4 KnotsCount=2 Degree=3 IsPeriodic=0
    g98: BSplineCurve PolesCount=2 KnotsCount=2 Degree=1 IsPeriodic=0
    g99: BSplineCurve PolesCount=2 KnotsCount=2 Degree=1 IsPeriodic=0
    g100: BSplineCurve PolesCount=4 KnotsCount=2 Degree=3 IsPeriodic=0
    g101: BSplineCurve PolesCount=4 KnotsCount=2 Degree=3 IsPeriodic=0
    g102: BSplineCurve PolesCount=4 KnotsCount=2 Degree=3 IsPeriodic=0
    g103: BSplineCurve PolesCount=4 KnotsCount=2 Degree=3 IsPeriodic=0
    g104: BSplineCurve PolesCount=2 KnotsCount=2 Degree=1 IsPeriodic=0
    g105: BSplineCurve PolesCount=4 KnotsCount=2 Degree=3 IsPeriodic=0
    g106: BSplineCurve PolesCount=4 KnotsCount=2 Degree=3 IsPeriodic=0
    g107: BSplineCurve PolesCount=4 KnotsCount=2 Degree=3 IsPeriodic=0
    g108: BSplineCurve PolesCount=2 KnotsCount=2 Degree=1 IsPeriodic=0
    g109: BSplineCurve PolesCount=4 KnotsCount=2 Degree=3 IsPeriodic=0
    g110: BSplineCurve PolesCount=4 KnotsCount=2 Degree=3 IsPeriodic=0
    g111: BSplineCurve PolesCount=2 KnotsCount=2 Degree=1 IsPeriodic=0
    g112: BSplineCurve PolesCount=4 KnotsCount=2 Degree=3 IsPeriodic=0
    g113: BSplineCurve PolesCount=4 KnotsCount=2 Degree=3 IsPeriodic=0
    g114: BSplineCurve PolesCount=4 KnotsCount=2 Degree=3 IsPeriodic=0
    g115: BSplineCurve PolesCount=2 KnotsCount=2 Degree=1 IsPeriodic=0
    g116: BSplineCurve PolesCount=4 KnotsCount=2 Degree=3 IsPeriodic=0
    g117: BSplineCurve PolesCount=2 KnotsCount=2 Degree=1 IsPeriodic=0
    g118: BSplineCurve PolesCount=4 KnotsCount=2 Degree=3 IsPeriodic=0
    g119: BSplineCurve PolesCount=2 KnotsCount=2 Degree=1 IsPeriodic=0
    g120: BSplineCurve PolesCount=4 KnotsCount=2 Degree=3 IsPeriodic=0
    g121: BSplineCurve PolesCount=2 KnotsCount=2 Degree=1 IsPeriodic=0
    g122: BSplineCurve PolesCount=4 KnotsCount=2 Degree=3 IsPeriodic=0
    g123: BSplineCurve PolesCount=2 KnotsCount=2 Degree=1 IsPeriodic=0
    g124: BSplineCurve PolesCount=4 KnotsCount=2 Degree=3 IsPeriodic=0
    g125: BSplineCurve PolesCount=4 KnotsCount=2 Degree=3 IsPeriodic=0
    g126: BSplineCurve PolesCount=4 KnotsCount=2 Degree=3 IsPeriodic=0
    g127: BSplineCurve PolesCount=2 KnotsCount=2 Degree=1 IsPeriodic=0
    g128: BSplineCurve PolesCount=4 KnotsCount=2 Degree=3 IsPeriodic=0
    g129: BSplineCurve PolesCount=4 KnotsCount=2 Degree=3 IsPeriodic=0
    g130: BSplineCurve PolesCount=2 KnotsCount=2 Degree=1 IsPeriodic=0
    g131: BSplineCurve PolesCount=4 KnotsCount=2 Degree=3 IsPeriodic=0
    g132: BSplineCurve PolesCount=4 KnotsCount=2 Degree=3 IsPeriodic=0
    g133: BSplineCurve PolesCount=4 KnotsCount=2 Degree=3 IsPeriodic=0
    g134: BSplineCurve PolesCount=4 KnotsCount=2 Degree=3 IsPeriodic=0
    g135: BSplineCurve PolesCount=2 KnotsCount=2 Degree=1 IsPeriodic=0
    g136: BSplineCurve PolesCount=4 KnotsCount=2 Degree=3 IsPeriodic=0
    g137: BSplineCurve PolesCount=4 KnotsCount=2 Degree=3 IsPeriodic=0
    g138: BSplineCurve PolesCount=4 KnotsCount=2 Degree=3 IsPeriodic=0
    g139: BSplineCurve PolesCount=4 KnotsCount=2 Degree=3 IsPeriodic=0
    g140: BSplineCurve PolesCount=2 KnotsCount=2 Degree=1 IsPeriodic=0
    g141: BSplineCurve PolesCount=4 KnotsCount=2 Degree=3 IsPeriodic=0
    g142: BSplineCurve PolesCount=4 KnotsCount=2 Degree=3 IsPeriodic=0
    g143: BSplineCurve PolesCount=4 KnotsCount=2 Degree=3 IsPeriodic=0
    g144: BSplineCurve PolesCount=2 KnotsCount=2 Degree=1 IsPeriodic=0
    g145: BSplineCurve PolesCount=2 KnotsCount=2 Degree=1 IsPeriodic=0
    g146: BSplineCurve PolesCount=4 KnotsCount=2 Degree=3 IsPeriodic=0
    g147: BSplineCurve PolesCount=2 KnotsCount=2 Degree=1 IsPeriodic=0
    g148: BSplineCurve PolesCount=2 KnotsCount=2 Degree=1 IsPeriodic=0
    g149: BSplineCurve PolesCount=2 KnotsCount=2 Degree=1 IsPeriodic=0
    g150: BSplineCurve PolesCount=4 KnotsCount=2 Degree=3 IsPeriodic=0
    g151: BSplineCurve PolesCount=2 KnotsCount=2 Degree=1 IsPeriodic=0
    g152: BSplineCurve PolesCount=2 KnotsCount=2 Degree=1 IsPeriodic=0
    g153: BSplineCurve PolesCount=4 KnotsCount=2 Degree=3 IsPeriodic=0
    g154: BSplineCurve PolesCount=4 KnotsCount=2 Degree=3 IsPeriodic=0
    g155: BSplineCurve PolesCount=4 KnotsCount=2 Degree=3 IsPeriodic=0
    g156: BSplineCurve PolesCount=4 KnotsCount=2 Degree=3 IsPeriodic=0
    g157: BSplineCurve PolesCount=4 KnotsCount=2 Degree=3 IsPeriodic=0
    g158: BSplineCurve PolesCount=2 KnotsCount=2 Degree=1 IsPeriodic=0
    g159: BSplineCurve PolesCount=4 KnotsCount=2 Degree=3 IsPeriodic=0
    g160: BSplineCurve PolesCount=4 KnotsCount=2 Degree=3 IsPeriodic=0
    g161: BSplineCurve PolesCount=2 KnotsCount=2 Degree=1 IsPeriodic=0
    g162: BSplineCurve PolesCount=4 KnotsCount=2 Degree=3 IsPeriodic=0
    g163: BSplineCurve PolesCount=4 KnotsCount=2 Degree=3 IsPeriodic=0
    g164: BSplineCurve PolesCount=4 KnotsCount=2 Degree=3 IsPeriodic=0
    g165: BSplineCurve PolesCount=4 KnotsCount=2 Degree=3 IsPeriodic=0
    g166: BSplineCurve PolesCount=4 KnotsCount=2 Degree=3 IsPeriodic=0
    g167: BSplineCurve PolesCount=2 KnotsCount=2 Degree=1 IsPeriodic=0
    g168: BSplineCurve PolesCount=2 KnotsCount=2 Degree=1 IsPeriodic=0
    g169: BSplineCurve PolesCount=4 KnotsCount=2 Degree=3 IsPeriodic=0
    g170: BSplineCurve PolesCount=4 KnotsCount=2 Degree=3 IsPeriodic=0
    g171: BSplineCurve PolesCount=4 KnotsCount=2 Degree=3 IsPeriodic=0
    g172: BSplineCurve PolesCount=4 KnotsCount=2 Degree=3 IsPeriodic=0
    g173: BSplineCurve PolesCount=4 KnotsCount=2 Degree=3 IsPeriodic=0
    g174: BSplineCurve PolesCount=2 KnotsCount=2 Degree=1 IsPeriodic=0
    g175: BSplineCurve PolesCount=4 KnotsCount=2 Degree=3 IsPeriodic=0
    g176: BSplineCurve PolesCount=4 KnotsCount=2 Degree=3 IsPeriodic=0
    g177: BSplineCurve PolesCount=2 KnotsCount=2 Degree=1 IsPeriodic=0
    g178: BSplineCurve PolesCount=4 KnotsCount=2 Degree=3 IsPeriodic=0
    g179: BSplineCurve PolesCount=4 KnotsCount=2 Degree=3 IsPeriodic=0
    g180: BSplineCurve PolesCount=4 KnotsCount=2 Degree=3 IsPeriodic=0
    g181: BSplineCurve PolesCount=4 KnotsCount=2 Degree=3 IsPeriodic=0
    g182: BSplineCurve PolesCount=4 KnotsCount=2 Degree=3 IsPeriodic=0
    g183: BSplineCurve PolesCount=2 KnotsCount=2 Degree=1 IsPeriodic=0
    g184: BSplineCurve PolesCount=2 KnotsCount=2 Degree=1 IsPeriodic=0
    g185: BSplineCurve PolesCount=4 KnotsCount=2 Degree=3 IsPeriodic=0
    g186: BSplineCurve PolesCount=2 KnotsCount=2 Degree=1 IsPeriodic=0
    g187: BSplineCurve PolesCount=2 KnotsCount=2 Degree=1 IsPeriodic=0
    g188: BSplineCurve PolesCount=2 KnotsCount=2 Degree=1 IsPeriodic=0
    g189: BSplineCurve PolesCount=4 KnotsCount=2 Degree=3 IsPeriodic=0
    g190: BSplineCurve PolesCount=2 KnotsCount=2 Degree=1 IsPeriodic=0
    g191: BSplineCurve PolesCount=2 KnotsCount=2 Degree=1 IsPeriodic=0
    g192: BSplineCurve PolesCount=4 KnotsCount=2 Degree=3 IsPeriodic=0
    g193: BSplineCurve PolesCount=4 KnotsCount=2 Degree=3 IsPeriodic=0
    g194: BSplineCurve PolesCount=4 KnotsCount=2 Degree=3 IsPeriodic=0
    g195: BSplineCurve PolesCount=4 KnotsCount=2 Degree=3 IsPeriodic=0
    g196: BSplineCurve PolesCount=2 KnotsCount=2 Degree=1 IsPeriodic=0
    g197: BSplineCurve PolesCount=4 KnotsCount=2 Degree=3 IsPeriodic=0
    g198: BSplineCurve PolesCount=4 KnotsCount=2 Degree=3 IsPeriodic=0
    g199: BSplineCurve PolesCount=4 KnotsCount=2 Degree=3 IsPeriodic=0
    g200: BSplineCurve PolesCount=2 KnotsCount=2 Degree=1 IsPeriodic=0
    g201: BSplineCurve PolesCount=4 KnotsCount=2 Degree=3 IsPeriodic=0
    g202: BSplineCurve PolesCount=4 KnotsCount=2 Degree=3 IsPeriodic=0
    g203: BSplineCurve PolesCount=2 KnotsCount=2 Degree=1 IsPeriodic=0
    g204: BSplineCurve PolesCount=4 KnotsCount=2 Degree=3 IsPeriodic=0
    g205: BSplineCurve PolesCount=4 KnotsCount=2 Degree=3 IsPeriodic=0
    g206: BSplineCurve PolesCount=4 KnotsCount=2 Degree=3 IsPeriodic=0
    g207: BSplineCurve PolesCount=2 KnotsCount=2 Degree=1 IsPeriodic=0
    g208: BSplineCurve PolesCount=4 KnotsCount=2 Degree=3 IsPeriodic=0
    g209: BSplineCurve PolesCount=2 KnotsCount=2 Degree=1 IsPeriodic=0
    g210: BSplineCurve PolesCount=4 KnotsCount=2 Degree=3 IsPeriodic=0
    g211: BSplineCurve PolesCount=2 KnotsCount=2 Degree=1 IsPeriodic=0
    g212: BSplineCurve PolesCount=4 KnotsCount=2 Degree=3 IsPeriodic=0
    g213: BSplineCurve PolesCount=2 KnotsCount=2 Degree=1 IsPeriodic=0
    g214: BSplineCurve PolesCount=4 KnotsCount=2 Degree=3 IsPeriodic=0
    g215: BSplineCurve PolesCount=2 KnotsCount=2 Degree=1 IsPeriodic=0
    g216: BSplineCurve PolesCount=4 KnotsCount=2 Degree=3 IsPeriodic=0
    g217: BSplineCurve PolesCount=4 KnotsCount=2 Degree=3 IsPeriodic=0
    g218: BSplineCurve PolesCount=4 KnotsCount=2 Degree=3 IsPeriodic=0
    g219: BSplineCurve PolesCount=2 KnotsCount=2 Degree=1 IsPeriodic=0
    g220: BSplineCurve PolesCount=2 KnotsCount=2 Degree=1 IsPeriodic=0
    g221: BSplineCurve PolesCount=4 KnotsCount=2 Degree=3 IsPeriodic=0
    g222: BSplineCurve PolesCount=4 KnotsCount=2 Degree=3 IsPeriodic=0
    g223: BSplineCurve PolesCount=4 KnotsCount=2 Degree=3 IsPeriodic=0
    g224: BSplineCurve PolesCount=4 KnotsCount=2 Degree=3 IsPeriodic=0
    g225: BSplineCurve PolesCount=4 KnotsCount=2 Degree=3 IsPeriodic=0
    g226: BSplineCurve PolesCount=4 KnotsCount=2 Degree=3 IsPeriodic=0
    g227: BSplineCurve PolesCount=2 KnotsCount=2 Degree=1 IsPeriodic=0
    g228: BSplineCurve PolesCount=2 KnotsCount=2 Degree=1 IsPeriodic=0
    g229: BSplineCurve PolesCount=4 KnotsCount=2 Degree=3 IsPeriodic=0
    g230: BSplineCurve PolesCount=4 KnotsCount=2 Degree=3 IsPeriodic=0
    g231: BSplineCurve PolesCount=4 KnotsCount=2 Degree=3 IsPeriodic=0
    g232: BSplineCurve PolesCount=2 KnotsCount=2 Degree=1 IsPeriodic=0
    g233: BSplineCurve PolesCount=2 KnotsCount=2 Degree=1 IsPeriodic=0
    g234: BSplineCurve PolesCount=2 KnotsCount=2 Degree=1 IsPeriodic=0
    g235: BSplineCurve PolesCount=2 KnotsCount=2 Degree=1 IsPeriodic=0
    g236: BSplineCurve PolesCount=2 KnotsCount=2 Degree=1 IsPeriodic=0
    g237: BSplineCurve PolesCount=4 KnotsCount=2 Degree=3 IsPeriodic=0
    g238: BSplineCurve PolesCount=4 KnotsCount=2 Degree=3 IsPeriodic=0
    g239: BSplineCurve PolesCount=4 KnotsCount=2 Degree=3 IsPeriodic=0
    g240: BSplineCurve PolesCount=4 KnotsCount=2 Degree=3 IsPeriodic=0
    g241: BSplineCurve PolesCount=4 KnotsCount=2 Degree=3 IsPeriodic=0
    g242: BSplineCurve PolesCount=4 KnotsCount=2 Degree=3 IsPeriodic=0
    g243: BSplineCurve PolesCount=4 KnotsCount=2 Degree=3 IsPeriodic=0
    g244: BSplineCurve PolesCount=4 KnotsCount=2 Degree=3 IsPeriodic=0
    g245: BSplineCurve PolesCount=2 KnotsCount=2 Degree=1 IsPeriodic=0
    g246: BSplineCurve PolesCount=2 KnotsCount=2 Degree=1 IsPeriodic=0
    g247: BSplineCurve PolesCount=4 KnotsCount=2 Degree=3 IsPeriodic=0
    g248: BSplineCurve PolesCount=4 KnotsCount=2 Degree=3 IsPeriodic=0
    g249: BSplineCurve PolesCount=4 KnotsCount=2 Degree=3 IsPeriodic=0
    g250: BSplineCurve PolesCount=4 KnotsCount=2 Degree=3 IsPeriodic=0
    g251: BSplineCurve PolesCount=4 KnotsCount=2 Degree=3 IsPeriodic=0
    g252: BSplineCurve PolesCount=4 KnotsCount=2 Degree=3 IsPeriodic=0
    g253: BSplineCurve PolesCount=2 KnotsCount=2 Degree=1 IsPeriodic=0
    g254: BSplineCurve PolesCount=4 KnotsCount=2 Degree=3 IsPeriodic=0
    g255: BSplineCurve PolesCount=2 KnotsCount=2 Degree=1 IsPeriodic=0
    g256: BSplineCurve PolesCount=4 KnotsCount=2 Degree=3 IsPeriodic=0
    g257: BSplineCurve PolesCount=2 KnotsCount=2 Degree=1 IsPeriodic=0
    g258: BSplineCurve PolesCount=4 KnotsCount=2 Degree=3 IsPeriodic=0
    g259: BSplineCurve PolesCount=2 KnotsCount=2 Degree=1 IsPeriodic=0
    g260: BSplineCurve PolesCount=4 KnotsCount=2 Degree=3 IsPeriodic=0
    g261: BSplineCurve PolesCount=2 KnotsCount=2 Degree=1 IsPeriodic=0
    g262: BSplineCurve PolesCount=4 KnotsCount=2 Degree=3 IsPeriodic=0
    g263: BSplineCurve PolesCount=2 KnotsCount=2 Degree=1 IsPeriodic=0
    g264: BSplineCurve PolesCount=2 KnotsCount=2 Degree=1 IsPeriodic=0
    g265: BSplineCurve PolesCount=4 KnotsCount=2 Degree=3 IsPeriodic=0
    g266: BSplineCurve PolesCount=2 KnotsCount=2 Degree=1 IsPeriodic=0
    g267: BSplineCurve PolesCount=2 KnotsCount=2 Degree=1 IsPeriodic=0
    g268: BSplineCurve PolesCount=4 KnotsCount=2 Degree=3 IsPeriodic=0
    g269: BSplineCurve PolesCount=2 KnotsCount=2 Degree=1 IsPeriodic=0
    g270: BSplineCurve PolesCount=4 KnotsCount=2 Degree=3 IsPeriodic=0
    g271: BSplineCurve PolesCount=2 KnotsCount=2 Degree=1 IsPeriodic=0
    g272: BSplineCurve PolesCount=4 KnotsCount=2 Degree=3 IsPeriodic=0
    g273: BSplineCurve PolesCount=2 KnotsCount=2 Degree=1 IsPeriodic=0
    g274: BSplineCurve PolesCount=4 KnotsCount=2 Degree=3 IsPeriodic=0
    g275: BSplineCurve PolesCount=2 KnotsCount=2 Degree=1 IsPeriodic=0
    g276: BSplineCurve PolesCount=4 KnotsCount=2 Degree=3 IsPeriodic=0
    g277: BSplineCurve PolesCount=2 KnotsCount=2 Degree=1 IsPeriodic=0
    g278: BSplineCurve PolesCount=2 KnotsCount=2 Degree=1 IsPeriodic=0
    g279: BSplineCurve PolesCount=2 KnotsCount=2 Degree=1 IsPeriodic=0
    g280: BSplineCurve PolesCount=2 KnotsCount=2 Degree=1 IsPeriodic=0
    g281: BSplineCurve PolesCount=2 KnotsCount=2 Degree=1 IsPeriodic=0
    g282: BSplineCurve PolesCount=2 KnotsCount=2 Degree=1 IsPeriodic=0
    g283: BSplineCurve PolesCount=2 KnotsCount=2 Degree=1 IsPeriodic=0
    g284: BSplineCurve PolesCount=4 KnotsCount=2 Degree=3 IsPeriodic=0
    g285: BSplineCurve PolesCount=4 KnotsCount=2 Degree=3 IsPeriodic=0
    g286: BSplineCurve PolesCount=4 KnotsCount=2 Degree=3 IsPeriodic=0
    g287: BSplineCurve PolesCount=4 KnotsCount=2 Degree=3 IsPeriodic=0
    g288: BSplineCurve PolesCount=4 KnotsCount=2 Degree=3 IsPeriodic=0
    g289: BSplineCurve PolesCount=4 KnotsCount=2 Degree=3 IsPeriodic=0
    g290: BSplineCurve PolesCount=4 KnotsCount=2 Degree=3 IsPeriodic=0
    g291: BSplineCurve PolesCount=4 KnotsCount=2 Degree=3 IsPeriodic=0
  constraints (292):
    c: Coincident(g0,g1)
    c: Coincident(g1,g2)
    c: Coincident(g2,g3)
    c: Coincident(g3,g4)
    c: Coincident(g4,g5)
    c: Coincident(g5,g6)
    c: Coincident(g6,g7)
    c: Coincident(g7,g8)
    c: Coincident(g8,g9)
    c: Coincident(g9,g0)
    c: Coincident(g10,g11)
    c: Coincident(g11,g12)
    c: Coincident(g12,g13)
    c: Coincident(g13,g14)
    c: Coincident(g14,g15)
    c: Coincident(g15,g16)
    c: Coincident(g16,g17)
    c: Coincident(g17,g18)
    c: Coincident(g18,g10)
    c: Coincident(g19,g20)
    c: Coincident(g20,g21)
    c: Coincident(g21,g22)
    c: Coincident(g22,g23)
    c: Coincident(g23,g24)
    c: Coincident(g24,g19)
    c: Coincident(g25,g26)
    c: Coincident(g26,g27)
    c: Coincident(g27,g28)
    c: Coincident(g28,g29)
    c: Coincident(g29,g30)
    c: Coincident(g30,g25)
    c: Coincident(g31,g32)
    c: Coincident(g32,g33)
    c: Coincident(g33,g34)
    c: Coincident(g34,g35)
    c: Coincident(g35,g36)
    c: Coincident(g36,g37)
    c: Coincident(g37,g38)
    c: Coincident(g38,g31)
    c: Coincident(g39,g40)
    c: Coincident(g40,g41)
    c: Coincident(g41,g42)
    c: Coincident(g42,g39)
    c: Coincident(g43,g44)
    c: Coincident(g44,g45)
    c: Coincident(g45,g46)
    c: Coincident(g46,g43)
    c: Coincident(g47,g48)
    c: Coincident(g48,g49)
    c: Coincident(g49,g50)
    c: Coincident(g50,g51)
    c: Coincident(g51,g52)
    c: Coincident(g52,g53)
    c: Coincident(g53,g54)
    c: Coincident(g54,g55)
    c: Coincident(g55,g56)
    c: Coincident(g56,g57)
    c: Coincident(g57,g58)
    c: Coincident(g58,g59)
    c: Coincident(g59,g60)
    c: Coincident(g60,g61)
    c: Coincident(g61,g62)
    c: Coincident(g62,g63)
    c: Coincident(g63,g64)
    c: Coincident(g64,g65)
    c: Coincident(g65,g66)
    c: Coincident(g66,g67)
    c: Coincident(g67,g68)
    c: Coincident(g68,g69)
    c: Coincident(g69,g70)
    c: Coincident(g70,g71)
    c: Coincident(g71,g72)
    c: Coincident(g72,g73)
    c: Coincident(g73,g74)
    c: Coincident(g74,g75)
    c: Coincident(g75,g76)
    c: Coincident(g76,g77)
    c: Coincident(g77,g78)
    c: Coincident(g78,g79)
    c: Coincident(g79,g80)
    c: Coincident(g80,g81)
    c: Coincident(g81,g82)
    c: Coincident(g82,g83)
    c: Coincident(g83,g84)
    c: Coincident(g84,g85)
    c: Coincident(g85,g86)
    c: Coincident(g86,g87)
    c: Coincident(g87,g88)
    c: Coincident(g88,g89)
    c: Coincident(g89,g90)
    c: Coincident(g90,g91)
    c: Coincident(g91,g92)
    c: Coincident(g92,g93)
    c: Coincident(g93,g94)
    c: Coincident(g94,g95)
    c: Coincident(g95,g96)
    c: Coincident(g96,g97)
    c: Coincident(g97,g98)
    c: Coincident(g98,g99)
    c: Coincident(g99,g100)
    c: Coincident(g100,g101)
    c: Coincident(g101,g102)
    c: Coincident(g102,g103)
    c: Coincident(g103,g104)
    c: Coincident(g104,g105)
    c: Coincident(g105,g106)
    c: Coincident(g106,g107)
    c: Coincident(g107,g108)
    c: Coincident(g108,g109)
    c: Coincident(g109,g110)
    c: Coincident(g110,g111)
    c: Coincident(g111,g112)
    c: Coincident(g112,g113)
    c: Coincident(g113,g114)
    c: Coincident(g114,g115)
    c: Coincident(g115,g116)
    c: Coincident(g116,g47)
    c: Coincident(g117,g118)
    c: Coincident(g118,g119)
    c: Coincident(g119,g120)
    c: Coincident(g120,g121)
    c: Coincident(g121,g122)
    c: Coincident(g122,g123)
    c: Coincident(g123,g124)
    c: Coincident(g124,g117)
    c: Coincident(g125,g126)
    c: Coincident(g126,g127)
    c: Coincident(g127,g128)
    c: Coincident(g128,g129)
    c: Coincident(g129,g130)
    c: Coincident(g130,g131)
    c: Coincident(g131,g132)
    c: Coincident(g132,g125)
    c: Coincident(g133,g134)
    c: Coincident(g134,g135)
    c: Coincident(g135,g136)
    c: Coincident(g136,g133)
    c: Coincident(g137,g138)
    c: Coincident(g138,g139)
    c: Coincident(g139,g140)
    c: Coincident(g140,g137)
    c: Coincident(g141,g142)
    c: Coincident(g142,g143)
    c: Coincident(g143,g144)
    c: Coincident(g144,g145)
    c: Coincident(g145,g146)
    c: Coincident(g146,g147)
    c: Coincident(g147,g148)
    c: Coincident(g148,g149)
    c: Coincident(g149,g150)
    c: Coincident(g150,g151)
    c: Coincident(g151,g152)
    c: Coincident(g152,g153)
    c: Coincident(g153,g154)
    c: Coincident(g154,g155)
    c: Coincident(g155,g156)
    c: Coincident(g156,g157)
    c: Coincident(g157,g158)
    c: Coincident(g158,g159)
    c: Coincident(g159,g160)
    c: Coincident(g160,g161)
    c: Coincident(g161,g162)
    c: Coincident(g162,g163)
    c: Coincident(g163,g164)
    c: Coincident(g164,g165)
    c: Coincident(g165,g166)
    c: Coincident(g166,g167)
    c: Coincident(g167,g168)
    c: Coincident(g168,g169)
    c: Coincident(g169,g170)
    c: Coincident(g170,g171)
    c: Coincident(g171,g172)
    c: Coincident(g172,g173)
    c: Coincident(g173,g174)
    c: Coincident(g174,g175)
    c: Coincident(g175,g176)
    c: Coincident(g176,g177)
    c: Coincident(g177,g178)
    c: Coincident(g178,g179)
    c: Coincident(g179,g180)
    c: Coincident(g180,g181)
    c: Coincident(g181,g182)
    c: Coincident(g182,g183)
    c: Coincident(g183,g184)
    c: Coincident(g184,g185)
    c: Coincident(g185,g186)
    c: Coincident(g186,g187)
    c: Coincident(g187,g188)
    c: Coincident(g188,g189)
    c: Coincident(g189,g190)
    c: Coincident(g190,g191)
    c: Coincident(g191,g192)
    c: Coincident(g192,g193)
    c: Coincident(g193,g194)
    c: Coincident(g194,g195)
    c: Coincident(g195,g196)
    c: Coincident(g196,g197)
    c: Coincident(g197,g198)
    c: Coincident(g198,g199)
    c: Coincident(g199,g200)
    c: Coincident(g200,g201)
    c: Coincident(g201,g202)
    c: Coincident(g202,g203)
    c: Coincident(g203,g204)
    c: Coincident(g204,g205)
    c: Coincident(g205,g206)
    c: Coincident(g206,g207)
    c: Coincident(g207,g208)
    c: Coincident(g208,g141)
    c: Coincident(g209,g210)
    c: Coincident(g210,g211)
    c: Coincident(g211,g212)
    c: Coincident(g212,g213)
    c: Coincident(g213,g214)
    c: Coincident(g214,g215)
    c: Coincident(g215,g216)
    c: Coincident(g216,g209)
    c: Coincident(g217,g218)
    c: Coincident(g218,g219)
    c: Coincident(g219,g220)
    c: Coincident(g220,g221)
    c: Coincident(g221,g222)
    c: Coincident(g222,g223)
    c: Coincident(g223,g224)
    c: Coincident(g224,g225)
    c: Coincident(g225,g226)
    c: Coincident(g226,g227)
    c: Coincident(g227,g228)
    c: Coincident(g228,g229)
    c: Coincident(g229,g230)
    c: Coincident(g230,g231)
    c: Coincident(g231,g232)
    c: Coincident(g232,g233)
    c: Coincident(g233,g234)
    c: Coincident(g234,g235)
    c: Coincident(g235,g236)
    c: Coincident(g236,g237)
    c: Coincident(g237,g238)
    c: Coincident(g238,g239)
    c: Coincident(g239,g240)
    c: Coincident(g240,g241)
    c: Coincident(g241,g242)
    c: Coincident(g242,g243)
    c: Coincident(g243,g244)
    c: Coincident(g244,g245)
    c: Coincident(g245,g246)
    c: Coincident(g246,g247)
    c: Coincident(g247,g248)
    c: Coincident(g248,g249)
    c: Coincident(g249,g250)
    c: Coincident(g250,g251)
    c: Coincident(g251,g252)
    c: Coincident(g252,g253)
    c: Coincident(g253,g254)
    c: Coincident(g254,g255)
    c: Coincident(g255,g256)
    c: Coincident(g256,g257)
    c: Coincident(g257,g258)
    c: Coincident(g258,g259)
    c: Coincident(g259,g260)
    c: Coincident(g260,g261)
    c: Coincident(g261,g262)
    c: Coincident(g262,g263)
    c: Coincident(g263,g264)
    c: Coincident(g264,g265)
    c: Coincident(g265,g266)
    c: Coincident(g266,g267)
    c: Coincident(g267,g268)
    c: Coincident(g268,g269)
    c: Coincident(g269,g270)
    c: Coincident(g270,g271)
    c: Coincident(g271,g272)
    c: Coincident(g272,g273)
    c: Coincident(g273,g274)
    c: Coincident(g274,g275)
    c: Coincident(g275,g276)
    c: Coincident(g276,g277)
    c: Coincident(g277,g278)
    c: Coincident(g278,g279)
    c: Coincident(g279,g280)
    c: Coincident(g280,g281)
    c: Coincident(g281,g282)
    c: Coincident(g282,g283)
    c: Coincident(g283,g284)
    c: Coincident(g284,g285)
    c: Coincident(g285,g286)
    c: Coincident(g286,g287)
    c: Coincident(g287,g288)
    c: Coincident(g288,g289)
    c: Coincident(g289,g290)
    c: Coincident(g290,g291)
    c: Coincident(g291,g217)
FEATURE [PartDesign::Pocket] Pocket029
  BaseFeature = -> Pad032
  Direction = (0,0,1)
  Length = 0.4
  Length2 = 5
  Profile = -> Sketch050
  ReferenceAxis = -> Sketch050 [N_Axis]
  Refine = true
  SideType = 0
  Suppressed = false
  Type = 0
  Type2 = 0
FEATURE [PartDesign::Body] Body003  label="ThumbScrew"
  AllowCompound = false
  Group = -> [Sketch012,Pad012,Sketch013,Pocket011,PolarPattern,Fillet002,Sketch015,Pocket012,Sketch050,Pad032,Pocket029]
  Origin = -> Origin003
  Tip = -> Pocket029
FEATURE [Sketcher::SketchObject] Sketch057
  ArcFitTolerance = 1e-06
  ExternalTypes = [0]
  FullyConstrained = true
  MakeInternals = false
  MapMode = 5
  _ExternalGeoVersion = 0
  sketch-geometry (5):
    g0: ArcOfCircle CenterX=-25 CenterY=0 CenterZ=0 NormalX=0 NormalY=0 NormalZ=1 AngleXU=0 Radius=3.99999 StartAngle=5.32325 EndAngle=7.24312
    g1: LineSegment StartX=-22.7057 StartY=-3.2766 StartZ=0 EndX=-9.00001 EndY=-3.2766 EndZ=0
    g2: LineSegment StartX=-22.7057 StartY=3.2766 StartZ=0 EndX=-9.00001 EndY=3.2766 EndZ=0
    g3: LineSegment StartX=-9.00001 StartY=3.2766 StartZ=0 EndX=-9.00001 EndY=-3.2766 EndZ=0
    g4: GeomPoint X=-21 Y=0 Z=0
  constraints (14):
    c: Coincident(g0,g-3)
    c: PointOnObject(g0,g-3)
    c: Coincident(g1,g0)
    c: Horizontal(g1)
    c: Coincident(g2,g0)
    c: Horizontal(g2)
    c: Coincident(g3,g2)
    c: Coincident(g3,g1)
    c: Vertical(g3)
    c: Angle(g0) = 1.91986
    c: Vertical(g0,g0)
    c: PointOnObject(g4,g-1)
    c: PointOnObject(g4,g0)
    c: DistanceX(g4,g2) = 12
FEATURE [PartDesign::Pad] Pad033
  BaseFeature = -> LinearPattern
  Direction = (-1.2,0,1)
  Length = 12
  Length2 = 10
  Profile = -> Sketch057
  ReferenceAxis = -> Sketch057 [N_Axis]
  Refine = true
  SideType = 0
  Suppressed = false
  Type = 0
  Type2 = 0
  UseCustomVector = true
FEATURE [PartDesign::Fillet] Fillet006
  Base = -> Pad033 [Face137]
  BaseFeature = -> Pad033
  Radius = 2.5
  Refine = true
  SupportTransform = false
  Suppressed = false
  UseAllEdges = false
FEATURE [Sketcher::SketchObject] Sketch045
  ArcFitTolerance = 1e-06
  AttachmentSupport = -> [Fillet006]
  ExternalTypes = [0]
  FullyConstrained = true
  MakeInternals = false
  MapMode = 5
  Placement = pos=(0,0,65.65) rot=(0,0,1;0rad)
  _ExternalGeoVersion = 0
  sketch-geometry (5):
    g0: LineSegment StartX=-33 StartY=-2.99999 StartZ=0 EndX=-27 EndY=-2.99999 EndZ=0
    g1: LineSegment StartX=-27 StartY=-2.99999 StartZ=0 EndX=-27 EndY=2.99999 EndZ=0
    g2: LineSegment StartX=-27 StartY=2.99999 StartZ=0 EndX=-33 EndY=2.99999 EndZ=0
    g3: LineSegment StartX=-33 StartY=2.99999 StartZ=0 EndX=-33 EndY=-2.99999 EndZ=0
    g4: GeomPoint [constr] X=-30 Y=0 Z=0
  constraints (13):
    c: Coincident(g0,g1)
    c: Coincident(g1,g2)
    c: Coincident(g2,g3)
    c: Coincident(g3,g0)
    c: Horizontal(g0)
    c: Horizontal(g2)
    c: Vertical(g1)
    c: Vertical(g3)
    c: Symmetric(g2,g0,g4)
    c: Symmetric(g-3,g-4,g4)
    c: DistanceY(g-4,g0) = 1
    c: Equal(g0,g1)
    c: DistanceY(g1,g1) = 5.99999  'reforce_arm_width'
FEATURE [App::Link] Box  label="Box001"
  LinkPlacement = pos=(0,0,0) rot=(1,0,0;1.0472rad)
  LinkedObject = -> Body
  Placement = pos=(0,0,0) rot=(1,0,0;1.0472rad)
FEATURE [App::FeaturePython] GroundedJoint  # Assembly grounded joint (typed FeaturePython)
  ObjectToGround = -> Box
  Placement = pos=(0,0,0) rot=(1,0,0;1.0472rad)
FEATURE [App::Link] Painel  label="Painel001"
  LinkPlacement = pos=(1.3e-15,-86.1695,49.75) rot=(1,0,0;4.18879rad)
  LinkedObject = -> Body001
  Placement = pos=(1.3e-15,-86.1695,49.75) rot=(1,0,0;4.18879rad)
FEATURE [App::Link] stand  label="stand001"
  LinkPlacement = pos=(-0.212959,-0.466403,-0.807834) rot=(0,0.866025,0.5;3.14159rad)
  LinkedObject = -> Body005
  Placement = pos=(-0.212959,-0.466403,-0.807834) rot=(0,0.866025,0.5;3.14159rad)
FEATURE [App::Link] Arm  label="Arm001"
  LinkPlacement = pos=(65.65,-86.782,9.68911) rot=(0.250563,0.935113,-0.250563;4.64535rad)
  LinkedObject = -> Body002
  Placement = pos=(65.65,-86.782,9.68911) rot=(0.250563,0.935113,-0.250563;4.64535rad)
FEATURE [App::Link] Arm001  label="Arm002"
  LinkPlacement = pos=(-65.65,-86.782,9.68911) rot=(0.694747,0.186157,0.694747;2.77349rad)
  LinkedObject = -> Body002
  Placement = pos=(-65.65,-86.782,9.68911) rot=(0.694747,0.186157,0.694747;2.77349rad)
FEATURE [App::Link] Reforce2Arm  label="Reforce2Arm001"
  LinkPlacement = pos=(-68.55,-101.782,-16.2917) rot=(0.694747,0.186157,0.694747;2.77349rad)
  LinkedObject = -> Body007
  Placement = pos=(-68.55,-101.782,-16.2917) rot=(0.694747,0.186157,0.694747;2.77349rad)
FEATURE [App::Link] Knob  label="Knob001"
  LinkPlacement = pos=(48.25,-106.326,46.8381) rot=(0.999885,-0.013133,-0.007582;4.18869rad)
  LinkedObject = -> Body008
  Placement = pos=(48.25,-106.326,46.8381) rot=(0.999885,-0.013133,-0.007582;4.18869rad)
FEATURE [App::Link] ThumbScrew  label="ThumbScrew001"
  LinkPlacement = pos=(-69.65,-69.282,40) rot=(0.447214,0.774597,0.447214;1.82348rad)
  LinkedObject = -> Body003
  Placement = pos=(-69.65,-69.282,40) rot=(0.447214,0.774597,0.447214;1.82348rad)
FEATURE [App::Link] ThumbScrew001  label="ThumbScrew002"
  LinkPlacement = pos=(69.65,-69.282,40) rot=(-0.654654,-0.377964,0.654654;2.41886rad)
  LinkedObject = -> Body003
  Placement = pos=(69.65,-69.282,40) rot=(-0.654654,-0.377964,0.654654;2.41886rad)
FEATURE [App::FeaturePython] Joint  label="Fixed"  # Assembly joint (typed FeaturePython)
  Angle = 0
  AngleMax = 0
  AngleMin = 0
  Detach1 = false
  Detach2 = false
  Distance = 0
  Distance2 = 0
  EnableAngleMax = false
  EnableAngleMin = false
  EnableLengthMax = false
  EnableLengthMin = false
  JointType = 0 (Fixed)
  LengthMax = 0
  LengthMin = 0
  Offset1 = pos=(-0.05,0.05,0) rot=(0,0,1;0rad)
  Placement1 = pos=(-62.65,36.55,87) rot=(0,0,1;0rad)
  Placement2 = pos=(-62.65,-36.55,12.5) rot=(0,0,1;0rad)
  Reference1 = -> Box [Vertex27,Vertex27]
  Reference2 = -> Painel [Vertex537,Vertex537]
  Suppressed = false
FEATURE [App::FeaturePython] Joint001  label="Fixed001"  # Assembly joint (typed FeaturePython)
  Angle = 0
  AngleMax = 0
  AngleMin = 0
  Detach1 = false
  Detach2 = false
  Distance = 0
  Distance2 = 0
  EnableAngleMax = false
  EnableAngleMin = false
  EnableLengthMax = false
  EnableLengthMin = false
  JointType = 0 (Fixed)
  LengthMax = 0
  LengthMin = 0
  Placement1 = pos=(-0.212959,-0.932806,-5.3e-15) rot=(0,1,0;3.14159rad)
  Placement2 = pos=(-5.4e-15,-7.8e-15,8.8e-15) rot=(0,0,1;0rad)
  Reference1 = -> Box [Face74,Face74]
  Reference2 = -> stand [Face15,Face15]
  Suppressed = false
FEATURE [App::FeaturePython] Joint002  label="Revolute"  # Assembly joint (typed FeaturePython)
  Angle = 0
  AngleMax = 180
  AngleMin = -45
  Detach1 = false
  Detach2 = false
  Distance = 0
  Distance2 = 0
  EnableAngleMax = true
  EnableAngleMin = true
  EnableLengthMax = false
  EnableLengthMin = false
  JointType = 1 (Revolute)
  LengthMax = 0
  LengthMin = 0
  Placement1 = pos=(35,0,0) rot=(0,0,1;0rad)
  Placement2 = pos=(65.65,7.1e-15,19.5) rot=(-0.57735,-0.57735,-0.57735;4.18879rad)
  Reference1 = -> Arm [Edge27,Edge27]
  Reference2 = -> Painel [Edge598,Edge598]
  Suppressed = false
FEATURE [PartDesign::Pocket] Pocket030
  BaseFeature = -> Fillet006
  Direction = (0,0,-1)
  Length = 5
  Length2 = 5
  Offset = -1
  Profile = -> Sketch045
  ReferenceAxis = -> Sketch045 [N_Axis]
  Refine = true
  SideType = 0
  Suppressed = false
  Type = 2
  Type2 = 0
FEATURE [PartDesign::Body] Body002  label="Arm"
  AllowCompound = false
  Group = -> [Sketch010,Pad009,Pad010,Sketch011,Pad011,Fillet001,LinearPattern,Sketch045,Sketch057,Pad033,Fillet006,Pocket030]
  Origin = -> Origin002
  Tip = -> Pocket030
FEATURE [App::FeaturePython] Joint003  label="Fixed002"  # Assembly joint (typed FeaturePython)
  Angle = 0
  AngleMax = 0
  AngleMin = 0
  Detach1 = false
  Detach2 = false
  Distance = 0
  Distance2 = 0
  EnableAngleMax = false
  EnableAngleMin = false
  EnableLengthMax = false
  EnableLengthMin = false
  JointType = 0 (Fixed)
  LengthMax = 0
  LengthMin = 0
  Offset2 = pos=(0,0,0.1) rot=(0,0,1;0rad)
  Placement1 = pos=(4.26e-14,-1.42e-14,137.1) rot=(0,0,1;0rad)
  Placement2 = pos=(-30,0,-2.9) rot=(0,0,1;0rad)
  Reference1 = -> Reforce2Arm [Face6,Face6]
  Reference2 = -> Arm [Face153,Face153]
  Suppressed = false
FEATURE [App::FeaturePython] Joint004  label="Fixed003"  # Assembly joint (typed FeaturePython)
  Angle = 0
  AngleMax = 0
  AngleMin = 0
  Detach1 = false
  Detach2 = false
  Distance = 0
  Distance2 = 0
  EnableAngleMax = false
  EnableAngleMin = false
  EnableLengthMax = false
  EnableLengthMin = false
  JointType = 0 (Fixed)
  LengthMax = 0
  LengthMin = 0
  Offset2 = pos=(0,0,-0.1) rot=(0,0,1;0rad)
  Placement1 = pos=(-30,0,-3) rot=(0,0,1;0rad)
  Placement2 = pos=(0,0,-0.1) rot=(0,0,1;0rad)
  Reference1 = -> Arm001 [Face153,Face153]
  Reference2 = -> Reforce2Arm [Face5,Face5]
  Suppressed = false
FEATURE [App::FeaturePython] Joint005  label="Fixed004"  # Assembly joint (typed FeaturePython)
  Angle = 0
  AngleMax = 0
  AngleMin = 0
  Detach1 = false
  Detach2 = false
  Distance = 0
  Distance2 = 0
  EnableAngleMax = false
  EnableAngleMin = false
  EnableLengthMax = false
  EnableLengthMin = false
  JointType = 0 (Fixed)
  LengthMax = 0
  LengthMin = 0
  Offset2 = pos=(0,0,0) rot=(0,0,1;1.5708rad)
  Placement1 = pos=(0,0,4) rot=(0,0,1;0rad)
  Placement2 = pos=(65.65,7.1e-15,19.5) rot=(-0.707107,0,-0.707107;3.14159rad)
  Reference1 = -> ThumbScrew001 [Edge106,Edge106]
  Reference2 = -> Painel [Edge598,Edge598]
  Suppressed = false
FEATURE [App::FeaturePython] Joint006  label="Fixed005"  # Assembly joint (typed FeaturePython)
  Angle = 0
  AngleMax = 0
  AngleMin = 0
  Detach1 = false
  Detach2 = false
  Distance = 0
  Distance2 = 0
  EnableAngleMax = false
  EnableAngleMin = false
  EnableLengthMax = false
  EnableLengthMin = false
  JointType = 0 (Fixed)
  LengthMax = 0
  LengthMin = 0
  Offset2 = pos=(0,0,0) rot=(0,0,1;1.5708rad)
  Placement1 = pos=(0,0,4) rot=(0,0,1;0rad)
  Placement2 = pos=(-65.65,7.1e-15,19.5) rot=(-0.707107,0,-0.707107;3.14159rad)
  Reference1 = -> ThumbScrew [Edge106,Edge106]
  Reference2 = -> Painel [Edge604,Edge604]
  Suppressed = false
FEATURE [App::FeaturePython] Joint007  label="Revolute001"  # Assembly joint (typed FeaturePython)
  Angle = 0
  AngleMax = 0
  AngleMin = 0
  Detach1 = false
  Detach2 = false
  Distance = 0
  Distance2 = 0
  EnableAngleMax = false
  EnableAngleMin = false
  EnableLengthMax = false
  EnableLengthMin = false
  JointType = 1 (Revolute)
  LengthMax = 0
  LengthMin = 0
  Offset2 = pos=(0,0,2) rot=(0,0,1;0rad)
  Placement1 = pos=(7.1e-15,0,14) rot=(0,0,1;0rad)
  Placement2 = pos=(48.25,12.6,-2) rot=(-1,0,0;3.14159rad)
  Reference1 = -> Knob [Edge295,Edge295]
  Reference2 = -> Painel [Edge189,Edge189]
  Suppressed = false
FEATURE [Assembly::JointGroup] Joints
  Group = -> [GroundedJoint,Joint,Joint001,Joint002,Joint003,Joint004,Joint005,Joint006,Joint007]
FEATURE [Assembly::AssemblyObject] Assembly  label="Case"
  Group = -> [Joints,Box,GroundedJoint,Painel,stand,Arm,Arm001,Reforce2Arm,Knob,ThumbScrew,ThumbScrew001,Joint,Joint001,Joint002,Joint003,Joint004,Joint005,Joint006,Joint007]
  Origin = -> Origin012
  Type = Assembly
FEATURE [Sketcher::SketchObject] Sketch058
  ArcFitTolerance = 1e-06
  AttachmentSupport = -> [XY_Plane013]
  ExternalTypes = [0]
  FullyConstrained = true
  MakeInternals = false
  MapMode = 5
  _ExternalGeoVersion = 0
  sketch-geometry (10):
    g0: Circle CenterX=0 CenterY=0 CenterZ=0 NormalX=0 NormalY=0 NormalZ=1 AngleXU=0 Radius=1.55
    g1: LineSegment StartX=5 StartY=2.07107 StartZ=0 EndX=2.07107 EndY=5 EndZ=0
    g2: LineSegment StartX=2.07107 StartY=5 StartZ=0 EndX=-2.07107 EndY=5 EndZ=0
    g3: LineSegment StartX=-2.07107 StartY=5 StartZ=0 EndX=-5 EndY=2.07107 EndZ=0
    g4: LineSegment StartX=-5 StartY=2.07107 StartZ=0 EndX=-5 EndY=-2.07107 EndZ=0
    g5: LineSegment StartX=-5 StartY=-2.07107 StartZ=0 EndX=-2.07107 EndY=-5 EndZ=0
    g6: LineSegment StartX=-2.07107 StartY=-5 StartZ=0 EndX=2.07107 EndY=-5 EndZ=0
    g7: LineSegment StartX=2.07107 StartY=-5 StartZ=0 EndX=5 EndY=-2.07107 EndZ=0
    g8: LineSegment StartX=5 StartY=-2.07107 StartZ=0 EndX=5 EndY=2.07107 EndZ=0
    g9: Circle [constr] CenterX=0 CenterY=0 CenterZ=0 NormalX=0 NormalY=0 NormalZ=1 AngleXU=0 Radius=5.41196
  constraints (22):
    c: Diameter(g0) = 3.1
    c: Coincident(g1,g2)
    c: Coincident(g2,g3)
    c: Coincident(g3,g4)
    c: Coincident(g4,g5)
    c: Coincident(g5,g6)
    c: Coincident(g6,g7)
    c: Coincident(g7,g8)
    c: Coincident(g8,g1)
    c: Equal(g1, g2-g8) x7
    c: PointOnObject(g1,g9)
    c: PointOnObject(g2,g9)
    c: PointOnObject(g3,g9)
    c: PointOnObject(g4,g9)
    c: PointOnObject(g5,g9)
    c: PointOnObject(g6,g9)
    c: PointOnObject(g7,g9)
    c: PointOnObject(g8,g9)
    c: Coincident(g9,g0)
    c: Vertical(g8)
    c: DistanceY(g6,g1) = 10
    c: Coincident(g0,g-1)
FEATURE [PartDesign::Pad] Pad034
  Direction = (0,0,1)
  Length = 6.5
  Length2 = 10
  Profile = -> Sketch058
  ReferenceAxis = -> Sketch058 [N_Axis]
  Refine = true
  Reversed = true
  SideType = 0
  Suppressed = false
  Type = 0
  Type2 = 0
FEATURE [Sketcher::SketchObject] Sketch059
  ArcFitTolerance = 1e-06
  AttachmentSupport = -> [XY_Plane013]
  ExternalTypes = [0]
  FullyConstrained = true
  MakeInternals = false
  MapMode = 5
  _ExternalGeoVersion = 0
  sketch-geometry (7):
    g0: LineSegment StartX=1.61658 StartY=2.8 StartZ=0 EndX=-1.61658 EndY=2.8 EndZ=0
    g1: LineSegment StartX=-1.61658 StartY=2.8 StartZ=0 EndX=-3.23316 EndY=0 EndZ=0
    g2: LineSegment StartX=-3.23316 StartY=0 StartZ=0 EndX=-1.61658 EndY=-2.8 EndZ=0
    g3: LineSegment StartX=-1.61658 StartY=-2.8 StartZ=0 EndX=1.61658 EndY=-2.8 EndZ=0
    g4: LineSegment StartX=1.61658 StartY=-2.8 StartZ=0 EndX=3.23316 EndY=0 EndZ=0
    g5: LineSegment StartX=3.23316 StartY=0 StartZ=0 EndX=1.61658 EndY=2.8 EndZ=0
    g6: Circle [constr] CenterX=0 CenterY=0 CenterZ=0 NormalX=0 NormalY=0 NormalZ=1 AngleXU=0 Radius=3.23316
  constraints (16):
    c: Coincident(g0,g1)
    c: Coincident(g1,g2)
    c: Coincident(g2,g3)
    c: Coincident(g3,g4)
    c: Coincident(g4,g5)
    c: Coincident(g5,g0)
    c: Equal(g0, g1-g5) x5
    c: PointOnObject(g0,g6)
    c: PointOnObject(g1,g6)
    c: PointOnObject(g2,g6)
    c: PointOnObject(g3,g6)
    c: PointOnObject(g4,g6)
    c: PointOnObject(g5,g6)
    c: Coincident(g6,g-1)
    c: DistanceY(g3,g0) = 5.6
    c: PointOnObject(g4,g-1)
FEATURE [PartDesign::Pocket] Pocket031
  BaseFeature = -> Pad034
  Direction = (0,0,-1)
  Length = 5.5
  Length2 = 5
  Profile = -> Sketch059
  ReferenceAxis = -> Sketch059 [N_Axis]
  Refine = true
  SideType = 0
  Suppressed = false
  Type = 0
  Type2 = 0
FEATURE [PartDesign::Body] Body010  label="SensorThumbScrew"
  AllowCompound = false
  Group = -> [Sketch058,Pad034,Sketch059,Pocket031]
  Origin = -> Origin013
  Tip = -> Pocket031
FEATURE [App::Link] IrSensor  label="IrSensor001"
  LinkedObject = -> Body004
FEATURE [App::FeaturePython] GroundedJoint001  # Assembly grounded joint (typed FeaturePython)
  ObjectToGround = -> IrSensor
FEATURE [App::Link] SensorHolder  label="SensorHolder001"
  LinkPlacement = pos=(-53.55,52.5,1.1e-15) rot=(0,1,0;3.14159rad)
  LinkedObject = -> Body009
  Placement = pos=(-53.55,52.5,1.1e-15) rot=(0,1,0;3.14159rad)
FEATURE [App::Link] SensorHolder001  label="SensorHolder002"
  LinkPlacement = pos=(-75,40.55,-5e-16) rot=(0,0,1;4.71239rad)
  LinkedObject = -> Body009
  Placement = pos=(-75,40.55,-5e-16) rot=(0,0,1;4.71239rad)
FEATURE [App::Link] SensorThumbScrew  label="SensorThumbScrew001"
  LinkPlacement = pos=(-86.5,35.8,0) rot=(-0.57735,0.57735,0.57735;4.18879rad)
  LinkedObject = -> Body010
  Placement = pos=(-86.5,35.8,0) rot=(-0.57735,0.57735,0.57735;4.18879rad)
FEATURE [App::Link] SensorThumbScrew001  label="SensorThumbScrew002"
  LinkPlacement = pos=(-58.3,64,9.5e-15) rot=(0,0.707107,0.707107;3.14159rad)
  LinkedObject = -> Body010
  Placement = pos=(-58.3,64,9.5e-15) rot=(0,0.707107,0.707107;3.14159rad)
FEATURE [App::FeaturePython] Joint008  label="Revolute002"  # Assembly joint (typed FeaturePython)
  Angle = 0
  AngleMax = 0
  AngleMin = 0
  Detach1 = false
  Detach2 = false
  Distance = 0
  Distance2 = 0
  EnableAngleMax = false
  EnableAngleMin = false
  EnableLengthMax = false
  EnableLengthMin = false
  JointType = 1 (Revolute)
  LengthMax = 0
  LengthMin = 0
  Placement1 = pos=(4.75,-5,1.1e-15) rot=(1,0,0;1.5708rad)
  Placement2 = pos=(-58.3,47.5,0) rot=(0,0.707107,0.707107;3.14159rad)
  Reference1 = -> SensorHolder [Edge25,Edge25]
  Reference2 = -> IrSensor [Edge167,Edge167]
  Suppressed = false
FEATURE [App::FeaturePython] Joint009  label="Revolute003"  # Assembly joint (typed FeaturePython)
  Angle = 0
  AngleMax = 0
  AngleMin = 0
  Detach1 = false
  Detach2 = false
  Distance = 0
  Distance2 = 0
  EnableAngleMax = false
  EnableAngleMin = false
  EnableLengthMax = false
  EnableLengthMin = false
  JointType = 1 (Revolute)
  LengthMax = 0
  LengthMin = 0
  Placement1 = pos=(4.75,5,-1.1e-15) rot=(1,0,0;1.5708rad)
  Placement2 = pos=(-70,35.8,0) rot=(-0.57735,0.57735,0.57735;4.18879rad)
  Reference1 = -> SensorHolder001 [Edge5,Edge5]
  Reference2 = -> IrSensor [Edge174,Edge174]
  Suppressed = false
FEATURE [App::FeaturePython] Joint010  label="Revolute004"  # Assembly joint (typed FeaturePython)
  Angle = 0
  AngleMax = 0
  AngleMin = 0
  Detach1 = false
  Detach2 = false
  Distance = 0
  Distance2 = 0
  EnableAngleMax = false
  EnableAngleMin = false
  EnableLengthMax = false
  EnableLengthMin = false
  JointType = 1 (Revolute)
  LengthMax = 0
  LengthMin = 0
  Placement1 = pos=(0,0,-6.5) rot=(0,0,1;0rad)
  Placement2 = pos=(4.75,-5,1.1e-15) rot=(1,0,0;1.5708rad)
  Reference1 = -> SensorThumbScrew [Edge27,Edge27]
  Reference2 = -> SensorHolder001 [Edge25,Edge25]
  Suppressed = false
FEATURE [App::FeaturePython] Joint011  label="Revolute005"  # Assembly joint (typed FeaturePython)
  Angle = 0
  AngleMax = 0
  AngleMin = 0
  Detach1 = false
  Detach2 = false
  Distance = 0
  Distance2 = 0
  EnableAngleMax = false
  EnableAngleMin = false
  EnableLengthMax = false
  EnableLengthMin = false
  JointType = 1 (Revolute)
  LengthMax = 0
  LengthMin = 0
  Placement1 = pos=(0,0,-6.5) rot=(0,0,1;0rad)
  Placement2 = pos=(4.75,5,-1.1e-15) rot=(1,0,0;1.5708rad)
  Reference1 = -> SensorThumbScrew001 [Edge27,Edge27]
  Reference2 = -> SensorHolder [Edge5,Edge5]
  Suppressed = false
FEATURE [Part::FeaturePython] Screw  label="M3x16-Screw"  # WARN: FeaturePython — macro-defined, semantics opaque (R4)
  Diameter = 1
  Invert = false
  LeftHanded = false
  Length = 5
  LengthCustom = 16
  MatchOuter = false
  OffsetAngle = 0
  Thread = false
  Type = 37
FEATURE [Part::FeaturePython] Nut  label="M3-Nut"  # WARN: FeaturePython — macro-defined, semantics opaque (R4)
  Diameter = 4
  Invert = false
  LeftHanded = false
  MatchOuter = false
  OffsetAngle = 0
  Thread = false
  Type = 31
FEATURE [App::DocumentObjectGroup] Group001  label="Fasteners"
  Group = -> [Screw,Nut]
FEATURE [App::Link] M3x16_Screw  label="M3x16-Screw001"
  LinkPlacement = pos=(-83.4,35.8,0) rot=(-0.57735,0.57735,0.57735;4.18879rad)
  LinkedObject = -> Screw
  Placement = pos=(-83.4,35.8,0) rot=(-0.57735,0.57735,0.57735;4.18879rad)
FEATURE [App::Link] M3x16_Screw001  label="M3x16-Screw002"
  LinkPlacement = pos=(-58.3,60.9,8.2e-15) rot=(0,0.707107,0.707107;3.14159rad)
  LinkedObject = -> Screw
  Placement = pos=(-58.3,60.9,8.2e-15) rot=(0,0.707107,0.707107;3.14159rad)
FEATURE [App::Link] M3_Nut  label="M3-Nut001"
  LinkPlacement = pos=(-58.3,58.5,7.1e-15) rot=(0,0.707107,0.707107;3.14159rad)
  LinkedObject = -> Nut
  Placement = pos=(-58.3,58.5,7.1e-15) rot=(0,0.707107,0.707107;3.14159rad)
FEATURE [App::Link] M3_Nut001  label="M3-Nut002"
  LinkPlacement = pos=(-81,35.8,0) rot=(-0.57735,0.57735,0.57735;4.18879rad)
  LinkedObject = -> Nut
  Placement = pos=(-81,35.8,0) rot=(-0.57735,0.57735,0.57735;4.18879rad)
FEATURE [App::FeaturePython] Joint013  label="Fixed007"  # Assembly joint (typed FeaturePython)
  Angle = 0
  AngleMax = 0
  AngleMin = 0
  Detach1 = false
  Detach2 = false
  Distance = 0
  Distance2 = 0
  EnableAngleMax = false
  EnableAngleMin = false
  EnableLengthMax = false
  EnableLengthMin = false
  JointType = 0 (Fixed)
  LengthMax = 0
  LengthMin = 0
  Placement2 = pos=(0,0,-5.5) rot=(0,0,1;0rad)
  Reference1 = -> M3_Nut001 [Edge27,Edge27]
  Reference2 = -> SensorThumbScrew [Edge44,Edge44]
  Suppressed = false
FEATURE [App::FeaturePython] Joint014  label="Fixed008"  # Assembly joint (typed FeaturePython)
  Angle = 0
  AngleMax = 0
  AngleMin = 0
  Detach1 = false
  Detach2 = false
  Distance = 0
  Distance2 = 0
  EnableAngleMax = false
  EnableAngleMin = false
  EnableLengthMax = false
  EnableLengthMin = false
  JointType = 0 (Fixed)
  LengthMax = 0
  LengthMin = 0
  Placement2 = pos=(0,0,2.4) rot=(0,0,1;0rad)
  Reference1 = -> M3x16_Screw [Edge26,Edge26]
  Reference2 = -> M3_Nut001 [Edge7,Edge7]
  Suppressed = false
FEATURE [App::FeaturePython] Joint015  label="Fixed009"  # Assembly joint (typed FeaturePython)
  Angle = 0
  AngleMax = 0
  AngleMin = 0
  Detach1 = false
  Detach2 = false
  Distance = 0
  Distance2 = 0
  EnableAngleMax = false
  EnableAngleMin = false
  EnableLengthMax = false
  EnableLengthMin = false
  JointType = 0 (Fixed)
  LengthMax = 0
  LengthMin = 0
  Placement2 = pos=(0,0,-5.5) rot=(0,0,1;0rad)
  Reference1 = -> M3_Nut [Edge27,Edge27]
  Reference2 = -> SensorThumbScrew001 [Edge44,Edge44]
  Suppressed = false
FEATURE [App::FeaturePython] Joint016  label="Fixed010"  # Assembly joint (typed FeaturePython)
  Angle = 0
  AngleMax = 0
  AngleMin = 0
  Detach1 = false
  Detach2 = false
  Distance = 0
  Distance2 = 0
  EnableAngleMax = false
  EnableAngleMin = false
  EnableLengthMax = false
  EnableLengthMin = false
  JointType = 0 (Fixed)
  LengthMax = 0
  LengthMin = 0
  Placement2 = pos=(0,0,2.4) rot=(0,0,1;0rad)
  Reference1 = -> M3x16_Screw001 [Edge26,Edge26]
  Reference2 = -> M3_Nut [Edge2,Edge2]
  Suppressed = false
FEATURE [App::Link] IrCap  label="IrCap001"
  LinkPlacement = pos=(-7.1e-15,7.1e-15,0) rot=(0,0,1;0rad)
  LinkedObject = -> Body006
  Placement = pos=(-7.1e-15,7.1e-15,0) rot=(0,0,1;0rad)
FEATURE [App::FeaturePython] Joint017  label="Fixed011"  # Assembly joint (typed FeaturePython)
  Angle = 0
  AngleMax = 0
  AngleMin = 0
  Detach1 = false
  Detach2 = false
  Distance = 0
  Distance2 = 0
  EnableAngleMax = false
  EnableAngleMin = false
  EnableLengthMax = false
  EnableLengthMin = false
  JointType = 0 (Fixed)
  LengthMax = 0
  LengthMin = 0
  Offset2 = pos=(0,0,-17) rot=(0,0,1;0rad)
  Placement1 = pos=(55.6066,33.1066,-7) rot=(1,0,0;3.14159rad)
  Placement2 = pos=(55.6066,33.1066,-7) rot=(0,0,1;0rad)
  Reference1 = -> IrSensor [Edge186,Edge186]
  Reference2 = -> IrCap [Edge73,Edge73]
  Suppressed = false
FEATURE [Sketcher::SketchObject] Sketch060
  ArcFitTolerance = 1e-06
  AttachmentSupport = -> [XY_Plane015]
  ExternalTypes = [0]
  FullyConstrained = false
  MakeInternals = false
  MapMode = 5
  _ExternalGeoVersion = 0
  sketch-geometry (26):
    g0: LineSegment StartX=-2.4 StartY=-10.05 StartZ=0 EndX=7.5 EndY=-10.05 EndZ=0
    g1: LineSegment StartX=7.5 StartY=10.05 StartZ=0 EndX=-2.4 EndY=10.05 EndZ=0
    g2: LineSegment StartX=-7.5 StartY=4.95 StartZ=0 EndX=-7.5 EndY=-4.95 EndZ=0
    g3: GeomPoint [constr] X=0 Y=0 Z=0
    g4: LineSegment StartX=-5.15 StartY=-12.8 StartZ=0 EndX=8.5 EndY=-12.8 EndZ=0
    g5: LineSegment StartX=8.5 StartY=12.8 StartZ=0 EndX=-5.15 EndY=12.8 EndZ=0
    g6: LineSegment StartX=-10.25 StartY=7.7 StartZ=0 EndX=-10.25 EndY=-7.7 EndZ=0
    g7: GeomPoint [constr] X=0 Y=0 Z=0
    g8: ArcOfCircle CenterX=7.5 CenterY=4.95 CenterZ=0 NormalX=0 NormalY=0 NormalZ=1 AngleXU=0 Radius=5.1 StartAngle=-1.8e-15 EndAngle=1.5708
    g9: ArcOfCircle CenterX=7.5 CenterY=-4.95 CenterZ=0 NormalX=0 NormalY=0 NormalZ=1 AngleXU=0 Radius=5.1 StartAngle=4.71239 EndAngle=6.28319
    g10: ArcOfCircle CenterX=-2.4 CenterY=4.95 CenterZ=0 NormalX=0 NormalY=0 NormalZ=1 AngleXU=0 Radius=5.1 StartAngle=1.5708 EndAngle=3.14159
    g11: GeomPoint [constr] X=-7.5 Y=10.05 Z=0
    g12: ArcOfCircle CenterX=-2.4 CenterY=-4.95 CenterZ=0 NormalX=0 NormalY=0 NormalZ=1 AngleXU=0 Radius=5.1 StartAngle=3.14159 EndAngle=4.71239
    g13: GeomPoint [constr] X=-7.5 Y=-10.05 Z=0
    g14: ArcOfCircle CenterX=-5.15 CenterY=7.7 CenterZ=0 NormalX=0 NormalY=0 NormalZ=1 AngleXU=0 Radius=5.1 StartAngle=1.5708 EndAngle=3.14159
    g15: GeomPoint [constr] X=-10.25 Y=12.8 Z=0
    g16: ArcOfCircle CenterX=-5.15 CenterY=-7.7 CenterZ=0 NormalX=0 NormalY=0 NormalZ=1 AngleXU=0 Radius=5.1 StartAngle=3.14159 EndAngle=4.71239
    g17: GeomPoint [constr] X=-10.25 Y=-12.8 Z=0
    g18: ArcOfCircle CenterX=8.5 CenterY=7.7 CenterZ=0 NormalX=0 NormalY=0 NormalZ=1 AngleXU=0 Radius=5.1 StartAngle=0 EndAngle=1.5708
    g19: GeomPoint [constr] X=18.2979 Y=12.8 Z=0
    g20: ArcOfCircle CenterX=8.5 CenterY=-7.7 CenterZ=0 NormalX=0 NormalY=0 NormalZ=1 AngleXU=0 Radius=5.1 StartAngle=4.71239 EndAngle=6.28319
    g21: GeomPoint [constr] X=18.2979 Y=-12.8 Z=0
    g22: LineSegment StartX=13.6 StartY=-7.7 StartZ=0 EndX=13.6 EndY=-4.95 EndZ=0
    g23: LineSegment StartX=13.6 StartY=-4.95 StartZ=0 EndX=12.6 EndY=-4.95 EndZ=0
    g24: LineSegment StartX=12.6 StartY=4.95 StartZ=0 EndX=13.6 EndY=4.95 EndZ=0
    g25: LineSegment StartX=13.6 StartY=7.7 StartZ=0 EndX=13.6 EndY=4.95 EndZ=0
  constraints (58):
    c: Horizontal(g0)
    c: Horizontal(g1)
    c: Vertical(g2)
    c: Symmetric(g1,g13,g3)
    c: Coincident(g3,g-1)
    c: Horizontal(g4)
    c: Horizontal(g5)
    c: Vertical(g6)
    c: Coincident(g7,g3)
    c: Tangent(g8,g1) = -1.5708
    c: Tangent(g9,g0) = -1.5708
    c: Radius(g9) = 5.1
    c: PointOnObject(g11,g1)
    c: PointOnObject(g11,g2)
    c: Tangent(g1,g10) = -1.5708
    c: Tangent(g2,g10) = -1.5708
    c: PointOnObject(g13,g0)
    c: PointOnObject(g13,g2)
    c: Tangent(g0,g12) = -1.5708
    c: Tangent(g2,g12) = -1.5708
    c: Equal(g12,g9)
    c: Equal(g8,g10)
    c: PointOnObject(g15,g5)
    c: PointOnObject(g15,g6)
    c: Tangent(g5,g14) = -1.5708
    c: Tangent(g6,g14) = -1.5708
    c: PointOnObject(g17,g4)
    c: PointOnObject(g17,g6)
    c: Tangent(g4,g16) = -1.5708
    c: Tangent(g6,g16) = -1.5708
    c: Equal(g16,g12)
    c: Equal(g10,g14)
    c: DistanceY(g0,g1) = 20.1
    c: PointOnObject(g19,g5)
    c: Tangent(g5,g18) = -1.5708
    c: PointOnObject(g21,g4)
    c: Tangent(g4,g20) = -1.5708
    c: Equal(g20,g9)
    c: Equal(g18,g8)
    c: Vertical(g22)
    c: Coincident(g23,g22)
    c: Coincident(g23,g9)
    c: Coincident(g24,g8)
    c: Horizontal(g24)
    c: Coincident(g25,g24)
    c: Vertical(g25)
    c: Tangent(g25,g18) = 1.5708
    c: Tangent(g22,g20) = -1.5708
    c: Perpendicular(g9,g23)
    c: Perpendicular(g8,g24)
    c: Horizontal(g23)
    c: DistanceX(g23,g23) = 1
    c: Symmetric(g22,g24,g-1)
    c: Equal(g1,g0)
    c: DistanceX(g2,g8) = 20.1
    c: DistanceY(g1,g5) = 2.75
    c: DistanceY(g4,g0) = 2.75
    c: DistanceX(g6,g2) = 2.75
FEATURE [PartDesign::Pad] Pad035
  Direction = (0,0,1)
  Length = 10
  Length2 = 10
  Profile = -> Sketch060
  ReferenceAxis = -> Sketch060 [N_Axis]
  Refine = true
  SideType = 0
  Suppressed = false
  Type = 0
  Type2 = 0
FEATURE [PartDesign::Fillet] Fillet007
  Base = -> Pad035 [Face20,Face19]
  BaseFeature = -> Pad035
  Radius = 0.5
  Refine = true
  SupportTransform = false
  Suppressed = false
  UseAllEdges = false
FEATURE [PartDesign::Body] Body011  label="SensorClip"
  AllowCompound = false
  Group = -> [Sketch060,Pad035,Fillet007]
  Origin = -> Origin015
  Tip = -> Fillet007
FEATURE [App::DocumentObjectGroup] Group  label="Parts"
  Group = -> [Body,Body001,Body008,Body002,Body007,Body003,Body005,Body004,Body006,Body009,Body010,Body011]
FEATURE [App::Link] SensorClip  label="SensorClip001"
  LinkPlacement = pos=(-62.5,4.56131,-7.9e-15) rot=(1,0,0;1.5708rad)
  LinkedObject = -> Body011
  Placement = pos=(-62.5,4.56131,-7.9e-15) rot=(1,0,0;1.5708rad)
FEATURE [App::Link] SensorClip001  label="SensorClip002"
  LinkPlacement = pos=(5.44446,40,-7.7e-15) rot=(0.57735,-0.57735,-0.57735;2.0944rad)
  LinkedObject = -> Body011
  Placement = pos=(5.44446,40,-7.7e-15) rot=(0.57735,-0.57735,-0.57735;2.0944rad)
FEATURE [App::FeaturePython] Joint018  label="Fixed012"  # Assembly joint (typed FeaturePython)
  Angle = 0
  AngleMax = 0
  AngleMin = 0
  Detach1 = false
  Detach2 = false
  Distance = 0
  Distance2 = 0
  EnableAngleMax = false
  EnableAngleMin = false
  EnableLengthMax = false
  EnableLengthMin = false
  JointType = 0 (Fixed)
  LengthMax = 0
  LengthMin = 0
  Offset2 = pos=(0,0,0) rot=(0,0,1;1.5708rad)
  Placement1 = pos=(-7.5,7.2e-15,5) rot=(-0.57735,0.57735,-0.57735;2.0944rad)
  Placement2 = pos=(-70,-0.438691,1e-16) rot=(-0.707107,0,0.707107;3.14159rad)
  Reference1 = -> SensorClip [Face45,Face45]
  Reference2 = -> IrSensor [Face60,Face60]
  Suppressed = false
FEATURE [App::FeaturePython] Joint019  label="Fixed013"  # Assembly joint (typed FeaturePython)
  Angle = 0
  AngleMax = 0
  AngleMin = 0
  Detach1 = false
  Detach2 = false
  Distance = 0
  Distance2 = 0
  EnableAngleMax = false
  EnableAngleMin = false
  EnableLengthMax = false
  EnableLengthMin = false
  JointType = 0 (Fixed)
  LengthMax = 0
  LengthMin = 0
  Offset2 = pos=(0,0,0) rot=(0,0,1;1.5708rad)
  Placement1 = pos=(-7.5,7.1e-15,5) rot=(-0.57735,0.57735,-0.57735;2.0944rad)
  Placement2 = pos=(0.444461,47.5,3e-16) rot=(-0.57735,0.57735,0.57735;2.0944rad)
  Reference1 = -> SensorClip001 [Face45,Face45]
  Reference2 = -> IrSensor [Face57,Face57]
  Suppressed = false
FEATURE [Assembly::JointGroup] Joints001
  Group = -> [GroundedJoint001,Joint008,Joint009,Joint010,Joint011,Joint013,Joint014,Joint015,Joint016,Joint017,Joint018,Joint019]
FEATURE [Assembly::AssemblyObject] Assembly001  label="Sensor"
  Group = -> [Joints001,IrSensor,GroundedJoint001,SensorHolder,SensorHolder001,SensorThumbScrew,SensorThumbScrew001,Joint008,Joint009,Joint010,Joint011,M3x16_Screw,M3x16_Screw001,M3_Nut,M3_Nut001,Joint013,Joint014,Joint015,Joint016,IrCap,Joint017,SensorClip,SensorClip001,Joint018,Joint019]
  Origin = -> Origin014
  Placement = pos=(-150.164,-1.19834,83.8309) rot=(0,-0.969822,-0.243814;5.72653rad)
  Type = Assembly
FEATURE [App::Point] Origin016  label="Origin"
  Role = Origin
FEATURE [App::Point] Origin017  label="Origin"
  Role = Origin
FEATURE [App::Point] Origin018  label="Origin"
  Role = Origin
FEATURE [App::Point] Origin019  label="Origin"
  Role = Origin
FEATURE [App::Point] Origin020  label="Origin"
  Role = Origin
FEATURE [App::Point] Origin021  label="Origin"
  Role = Origin
FEATURE [App::Point] Origin022  label="Origin"
  Role = Origin
FEATURE [App::Point] Origin023  label="Origin"
  Role = Origin
FEATURE [App::Point] Origin024  label="Origin"
  Role = Origin
FEATURE [App::Point] Origin025  label="Origin"
  Role = Origin
FEATURE [App::Point] Origin026  label="Origin"
  Role = Origin
FEATURE [App::Point] Origin027  label="Origin"
  Role = Origin
FEATURE [App::Point] Origin028  label="Origin"
  Role = Origin
FEATURE [App::Point] Origin029  label="Origin"
  Role = Origin
